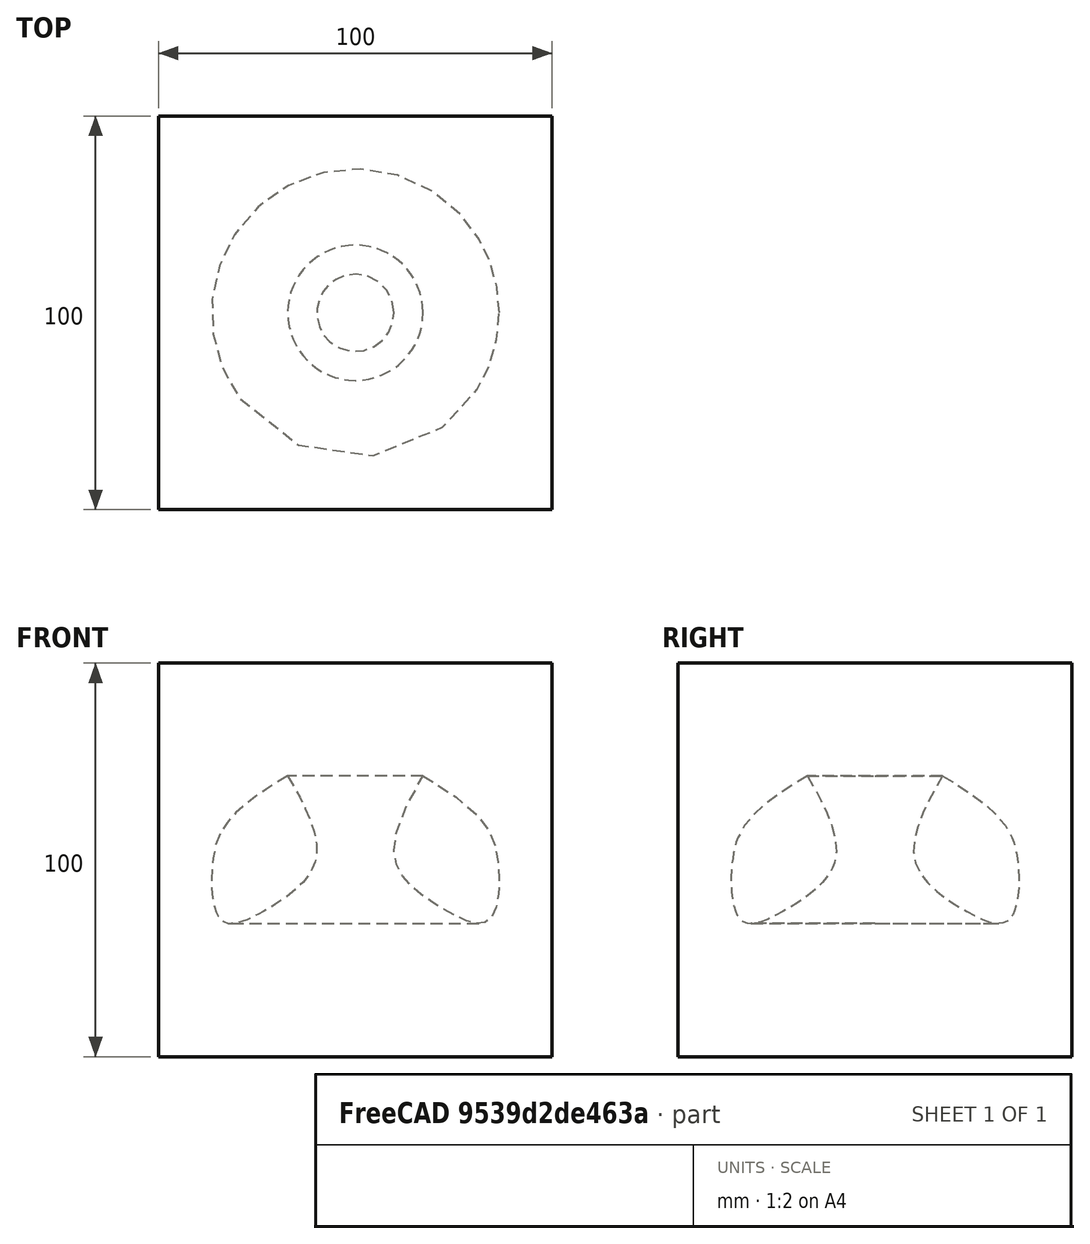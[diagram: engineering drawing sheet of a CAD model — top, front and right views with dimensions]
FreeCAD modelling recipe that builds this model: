
FCSTD DOCUMENT  (FreeCAD 1.0R39109 (Git))
Label: revolveSingleEdge-Bspline
License: All rights reserved
LicenseURL: http://en.wikipedia.org/wiki/All_rights_reserved
objects: App::DocumentObjectGroupPython×1248, App::Part×2, Part::FeaturePython×1, Sketcher::SketchObject×1, Part::Revolution×1
note: 4 computed .brp shape members not serialized (recipe doc carries the construction recipe); baked Part::Feature solids carry a one-line shape summary decoded from their .brp

FEATURE [App::DocumentObjectGroupPython] HALFPI  # scripted group (container) (typed FeaturePython)
  name = HALFPI
  value = pi/2.
FEATURE [App::DocumentObjectGroupPython] PI  # scripted group (container) (typed FeaturePython)
  name = PI
  value = 1.*pi
FEATURE [App::DocumentObjectGroupPython] TWOPI  # scripted group (container) (typed FeaturePython)
  name = TWOPI
  value = 2.*pi
FEATURE [App::DocumentObjectGroupPython] Constants  # scripted group (container) (typed FeaturePython)
  Group = -> [HALFPI,PI,TWOPI]
FEATURE [App::DocumentObjectGroupPython] Variables  # scripted group (container) (typed FeaturePython)
FEATURE [App::DocumentObjectGroupPython] Quantities  # scripted group (container) (typed FeaturePython)
FEATURE [App::DocumentObjectGroupPython] Isotopes  # scripted group (container) (typed FeaturePython)
FEATURE [App::DocumentObjectGroupPython] Elements  # scripted group (container) (typed FeaturePython)
FEATURE [App::DocumentObjectGroupPython] G4Isotopes  # scripted group (container) (typed FeaturePython)
FEATURE [App::DocumentObjectGroupPython] H_element  # scripted group (container) (typed FeaturePython)
  Z = 1
  atom_value = 1.008
  formula = H
  name = H_element
FEATURE [App::DocumentObjectGroupPython] He_element  # scripted group (container) (typed FeaturePython)
  Z = 2
  atom_value = 4.0026
  formula = He
  name = He_element
FEATURE [App::DocumentObjectGroupPython] Li_element  # scripted group (container) (typed FeaturePython)
  Z = 3
  atom_value = 6.94
  formula = Li
  name = Li_element
FEATURE [App::DocumentObjectGroupPython] Be_element  # scripted group (container) (typed FeaturePython)
  Z = 4
  atom_value = 9.01218
  formula = Be
  name = Be_element
FEATURE [App::DocumentObjectGroupPython] B_element  # scripted group (container) (typed FeaturePython)
  Z = 5
  atom_value = 10.81
  formula = B
  name = B_element
FEATURE [App::DocumentObjectGroupPython] C_element  # scripted group (container) (typed FeaturePython)
  Z = 6
  atom_value = 12.011
  formula = C
  name = C_element
FEATURE [App::DocumentObjectGroupPython] N_element  # scripted group (container) (typed FeaturePython)
  Z = 7
  atom_value = 14.007
  formula = N
  name = N_element
FEATURE [App::DocumentObjectGroupPython] O_element  # scripted group (container) (typed FeaturePython)
  Z = 8
  atom_value = 15.999
  formula = O
  name = O_element
FEATURE [App::DocumentObjectGroupPython] F_element  # scripted group (container) (typed FeaturePython)
  Z = 9
  atom_value = 18.9984
  formula = F
  name = F_element
FEATURE [App::DocumentObjectGroupPython] Ne_element  # scripted group (container) (typed FeaturePython)
  Z = 10
  atom_value = 20.1797
  formula = Ne
  name = Ne_element
FEATURE [App::DocumentObjectGroupPython] Na_element  # scripted group (container) (typed FeaturePython)
  Z = 11
  atom_value = 22.9898
  formula = Na
  name = Na_element
FEATURE [App::DocumentObjectGroupPython] Mg_element  # scripted group (container) (typed FeaturePython)
  Z = 12
  atom_value = 24.305
  formula = Mg
  name = Mg_element
FEATURE [App::DocumentObjectGroupPython] Al_element  # scripted group (container) (typed FeaturePython)
  Z = 13
  atom_value = 26.9815
  formula = Al
  name = Al_element
FEATURE [App::DocumentObjectGroupPython] Si_element  # scripted group (container) (typed FeaturePython)
  Z = 14
  atom_value = 28.085
  formula = Si
  name = Si_element
FEATURE [App::DocumentObjectGroupPython] P_element  # scripted group (container) (typed FeaturePython)
  Z = 15
  atom_value = 30.9738
  formula = P
  name = P_element
FEATURE [App::DocumentObjectGroupPython] S_element  # scripted group (container) (typed FeaturePython)
  Z = 16
  atom_value = 32.06
  formula = S
  name = S_element
FEATURE [App::DocumentObjectGroupPython] Cl_element  # scripted group (container) (typed FeaturePython)
  Z = 17
  atom_value = 35.45
  formula = Cl
  name = Cl_element
FEATURE [App::DocumentObjectGroupPython] Ar_element  # scripted group (container) (typed FeaturePython)
  Z = 18
  atom_value = 39.95
  formula = Ar
  name = Ar_element
FEATURE [App::DocumentObjectGroupPython] K_element  # scripted group (container) (typed FeaturePython)
  Z = 19
  atom_value = 39.0983
  formula = K
  name = K_element
FEATURE [App::DocumentObjectGroupPython] Ca_element  # scripted group (container) (typed FeaturePython)
  Z = 20
  atom_value = 40.078
  formula = Ca
  name = Ca_element
FEATURE [App::DocumentObjectGroupPython] Sc_element  # scripted group (container) (typed FeaturePython)
  Z = 21
  atom_value = 44.9559
  formula = Sc
  name = Sc_element
FEATURE [App::DocumentObjectGroupPython] Ti_element  # scripted group (container) (typed FeaturePython)
  Z = 22
  atom_value = 47.867
  formula = Ti
  name = Ti_element
FEATURE [App::DocumentObjectGroupPython] V_element  # scripted group (container) (typed FeaturePython)
  Z = 23
  atom_value = 50.9415
  formula = V
  name = V_element
FEATURE [App::DocumentObjectGroupPython] Cr_element  # scripted group (container) (typed FeaturePython)
  Z = 24
  atom_value = 51.9961
  formula = Cr
  name = Cr_element
FEATURE [App::DocumentObjectGroupPython] Mn_element  # scripted group (container) (typed FeaturePython)
  Z = 25
  atom_value = 54.938
  formula = Mn
  name = Mn_element
FEATURE [App::DocumentObjectGroupPython] Fe_element  # scripted group (container) (typed FeaturePython)
  Z = 26
  atom_value = 55.845
  formula = Fe
  name = Fe_element
FEATURE [App::DocumentObjectGroupPython] Co_element  # scripted group (container) (typed FeaturePython)
  Z = 27
  atom_value = 58.9332
  formula = Co
  name = Co_element
FEATURE [App::DocumentObjectGroupPython] Ni_element  # scripted group (container) (typed FeaturePython)
  Z = 28
  atom_value = 58.6934
  formula = Ni
  name = Ni_element
FEATURE [App::DocumentObjectGroupPython] Cu_element  # scripted group (container) (typed FeaturePython)
  Z = 29
  atom_value = 63.546
  formula = Cu
  name = Cu_element
FEATURE [App::DocumentObjectGroupPython] Zn_element  # scripted group (container) (typed FeaturePython)
  Z = 30
  atom_value = 65.38
  formula = Zn
  name = Zn_element
FEATURE [App::DocumentObjectGroupPython] Ga_element  # scripted group (container) (typed FeaturePython)
  Z = 31
  atom_value = 69.723
  formula = Ga
  name = Ga_element
FEATURE [App::DocumentObjectGroupPython] Ge_element  # scripted group (container) (typed FeaturePython)
  Z = 32
  atom_value = 72.63
  formula = Ge
  name = Ge_element
FEATURE [App::DocumentObjectGroupPython] As_element  # scripted group (container) (typed FeaturePython)
  Z = 33
  atom_value = 74.9216
  formula = As
  name = As_element
FEATURE [App::DocumentObjectGroupPython] Se_element  # scripted group (container) (typed FeaturePython)
  Z = 34
  atom_value = 78.971
  formula = Se
  name = Se_element
FEATURE [App::DocumentObjectGroupPython] Br_element  # scripted group (container) (typed FeaturePython)
  Z = 35
  atom_value = 79.904
  formula = Br
  name = Br_element
FEATURE [App::DocumentObjectGroupPython] Kr_element  # scripted group (container) (typed FeaturePython)
  Z = 36
  atom_value = 83.798
  formula = Kr
  name = Kr_element
FEATURE [App::DocumentObjectGroupPython] Rb_element  # scripted group (container) (typed FeaturePython)
  Z = 37
  atom_value = 85.4678
  formula = Rb
  name = Rb_element
FEATURE [App::DocumentObjectGroupPython] Sr_element  # scripted group (container) (typed FeaturePython)
  Z = 38
  atom_value = 87.62
  formula = Sr
  name = Sr_element
FEATURE [App::DocumentObjectGroupPython] Y_element  # scripted group (container) (typed FeaturePython)
  Z = 39
  atom_value = 88.9058
  formula = Y
  name = Y_element
FEATURE [App::DocumentObjectGroupPython] Zr_element  # scripted group (container) (typed FeaturePython)
  Z = 40
  atom_value = 91.224
  formula = Zr
  name = Zr_element
FEATURE [App::DocumentObjectGroupPython] Nb_element  # scripted group (container) (typed FeaturePython)
  Z = 41
  atom_value = 92.9064
  formula = Nb
  name = Nb_element
FEATURE [App::DocumentObjectGroupPython] Mo_element  # scripted group (container) (typed FeaturePython)
  Z = 42
  atom_value = 95.95
  formula = Mo
  name = Mo_element
FEATURE [App::DocumentObjectGroupPython] Tc_element  # scripted group (container) (typed FeaturePython)
  Z = 43
  atom_value = 97
  formula = Tc
  name = Tc_element
FEATURE [App::DocumentObjectGroupPython] Ru_element  # scripted group (container) (typed FeaturePython)
  Z = 44
  atom_value = 101.07
  formula = Ru
  name = Ru_element
FEATURE [App::DocumentObjectGroupPython] Rh_element  # scripted group (container) (typed FeaturePython)
  Z = 45
  atom_value = 102.905
  formula = Rh
  name = Rh_element
FEATURE [App::DocumentObjectGroupPython] Pd_element  # scripted group (container) (typed FeaturePython)
  Z = 46
  atom_value = 106.42
  formula = Pd
  name = Pd_element
FEATURE [App::DocumentObjectGroupPython] Ag_element  # scripted group (container) (typed FeaturePython)
  Z = 47
  atom_value = 107.868
  formula = Ag
  name = Ag_element
FEATURE [App::DocumentObjectGroupPython] Cd_element  # scripted group (container) (typed FeaturePython)
  Z = 48
  atom_value = 112.414
  formula = Cd
  name = Cd_element
FEATURE [App::DocumentObjectGroupPython] In_element  # scripted group (container) (typed FeaturePython)
  Z = 49
  atom_value = 114.818
  formula = In
  name = In_element
FEATURE [App::DocumentObjectGroupPython] Sn_element  # scripted group (container) (typed FeaturePython)
  Z = 50
  atom_value = 118.71
  formula = Sn
  name = Sn_element
FEATURE [App::DocumentObjectGroupPython] Sb_element  # scripted group (container) (typed FeaturePython)
  Z = 51
  atom_value = 121.76
  formula = Sb
  name = Sb_element
FEATURE [App::DocumentObjectGroupPython] Te_element  # scripted group (container) (typed FeaturePython)
  Z = 52
  atom_value = 127.6
  formula = Te
  name = Te_element
FEATURE [App::DocumentObjectGroupPython] I_element  # scripted group (container) (typed FeaturePython)
  Z = 53
  atom_value = 126.904
  formula = I
  name = I_element
FEATURE [App::DocumentObjectGroupPython] Xe_element  # scripted group (container) (typed FeaturePython)
  Z = 54
  atom_value = 131.293
  formula = Xe
  name = Xe_element
FEATURE [App::DocumentObjectGroupPython] Cs_element  # scripted group (container) (typed FeaturePython)
  Z = 55
  atom_value = 132.905
  formula = Cs
  name = Cs_element
FEATURE [App::DocumentObjectGroupPython] Ba_element  # scripted group (container) (typed FeaturePython)
  Z = 56
  atom_value = 137.327
  formula = Ba
  name = Ba_element
FEATURE [App::DocumentObjectGroupPython] La_element  # scripted group (container) (typed FeaturePython)
  Z = 57
  atom_value = 138.905
  formula = La
  name = La_element
FEATURE [App::DocumentObjectGroupPython] Ce_element  # scripted group (container) (typed FeaturePython)
  Z = 58
  atom_value = 140.116
  formula = Ce
  name = Ce_element
FEATURE [App::DocumentObjectGroupPython] Pr_element  # scripted group (container) (typed FeaturePython)
  Z = 59
  atom_value = 140.908
  formula = Pr
  name = Pr_element
FEATURE [App::DocumentObjectGroupPython] Nd_element  # scripted group (container) (typed FeaturePython)
  Z = 60
  atom_value = 144.242
  formula = Nd
  name = Nd_element
FEATURE [App::DocumentObjectGroupPython] Pm_element  # scripted group (container) (typed FeaturePython)
  Z = 61
  atom_value = 145
  formula = Pm
  name = Pm_element
FEATURE [App::DocumentObjectGroupPython] Sm_element  # scripted group (container) (typed FeaturePython)
  Z = 62
  atom_value = 150.36
  formula = Sm
  name = Sm_element
FEATURE [App::DocumentObjectGroupPython] Eu_element  # scripted group (container) (typed FeaturePython)
  Z = 63
  atom_value = 151.964
  formula = Eu
  name = Eu_element
FEATURE [App::DocumentObjectGroupPython] Gd_element  # scripted group (container) (typed FeaturePython)
  Z = 64
  atom_value = 157.25
  formula = Gd
  name = Gd_element
FEATURE [App::DocumentObjectGroupPython] Tb_element  # scripted group (container) (typed FeaturePython)
  Z = 65
  atom_value = 158.925
  formula = Tb
  name = Tb_element
FEATURE [App::DocumentObjectGroupPython] Dy_element  # scripted group (container) (typed FeaturePython)
  Z = 66
  atom_value = 162.5
  formula = Dy
  name = Dy_element
FEATURE [App::DocumentObjectGroupPython] Ho_element  # scripted group (container) (typed FeaturePython)
  Z = 67
  atom_value = 164.93
  formula = Ho
  name = Ho_element
FEATURE [App::DocumentObjectGroupPython] Er_element  # scripted group (container) (typed FeaturePython)
  Z = 68
  atom_value = 167.259
  formula = Er
  name = Er_element
FEATURE [App::DocumentObjectGroupPython] Tm_element  # scripted group (container) (typed FeaturePython)
  Z = 69
  atom_value = 168.934
  formula = Tm
  name = Tm_element
FEATURE [App::DocumentObjectGroupPython] Yb_element  # scripted group (container) (typed FeaturePython)
  Z = 70
  atom_value = 173.045
  formula = Yb
  name = Yb_element
FEATURE [App::DocumentObjectGroupPython] Lu_element  # scripted group (container) (typed FeaturePython)
  Z = 71
  atom_value = 174.967
  formula = Lu
  name = Lu_element
FEATURE [App::DocumentObjectGroupPython] Hf_element  # scripted group (container) (typed FeaturePython)
  Z = 72
  atom_value = 178.49
  formula = Hf
  name = Hf_element
FEATURE [App::DocumentObjectGroupPython] Ta_element  # scripted group (container) (typed FeaturePython)
  Z = 73
  atom_value = 180.948
  formula = Ta
  name = Ta_element
FEATURE [App::DocumentObjectGroupPython] W_element  # scripted group (container) (typed FeaturePython)
  Z = 74
  atom_value = 183.84
  formula = W
  name = W_element
FEATURE [App::DocumentObjectGroupPython] Re_element  # scripted group (container) (typed FeaturePython)
  Z = 75
  atom_value = 186.207
  formula = Re
  name = Re_element
FEATURE [App::DocumentObjectGroupPython] Os_element  # scripted group (container) (typed FeaturePython)
  Z = 76
  atom_value = 190.23
  formula = Os
  name = Os_element
FEATURE [App::DocumentObjectGroupPython] Ir_element  # scripted group (container) (typed FeaturePython)
  Z = 77
  atom_value = 192.217
  formula = Ir
  name = Ir_element
FEATURE [App::DocumentObjectGroupPython] Pt_element  # scripted group (container) (typed FeaturePython)
  Z = 78
  atom_value = 195.084
  formula = Pt
  name = Pt_element
FEATURE [App::DocumentObjectGroupPython] Au_element  # scripted group (container) (typed FeaturePython)
  Z = 79
  atom_value = 196.967
  formula = Au
  name = Au_element
FEATURE [App::DocumentObjectGroupPython] Hg_element  # scripted group (container) (typed FeaturePython)
  Z = 80
  atom_value = 200.592
  formula = Hg
  name = Hg_element
FEATURE [App::DocumentObjectGroupPython] Tl_element  # scripted group (container) (typed FeaturePython)
  Z = 81
  atom_value = 204.38
  formula = Tl
  name = Tl_element
FEATURE [App::DocumentObjectGroupPython] Pb_element  # scripted group (container) (typed FeaturePython)
  Z = 82
  atom_value = 207.2
  formula = Pb
  name = Pb_element
FEATURE [App::DocumentObjectGroupPython] Bi_element  # scripted group (container) (typed FeaturePython)
  Z = 83
  atom_value = 208.98
  formula = Bi
  name = Bi_element
FEATURE [App::DocumentObjectGroupPython] Po_element  # scripted group (container) (typed FeaturePython)
  Z = 84
  atom_value = 209
  formula = Po
  name = Po_element
FEATURE [App::DocumentObjectGroupPython] At_element  # scripted group (container) (typed FeaturePython)
  Z = 85
  atom_value = 210
  formula = At
  name = At_element
FEATURE [App::DocumentObjectGroupPython] Rn_element  # scripted group (container) (typed FeaturePython)
  Z = 86
  atom_value = 222
  formula = Rn
  name = Rn_element
FEATURE [App::DocumentObjectGroupPython] Fr_element  # scripted group (container) (typed FeaturePython)
  Z = 87
  atom_value = 223
  formula = Fr
  name = Fr_element
FEATURE [App::DocumentObjectGroupPython] Ra_element  # scripted group (container) (typed FeaturePython)
  Z = 88
  atom_value = 226
  formula = Ra
  name = Ra_element
FEATURE [App::DocumentObjectGroupPython] Ac_element  # scripted group (container) (typed FeaturePython)
  Z = 89
  atom_value = 227
  formula = Ac
  name = Ac_element
FEATURE [App::DocumentObjectGroupPython] Th_element  # scripted group (container) (typed FeaturePython)
  Z = 90
  atom_value = 232.038
  formula = Th
  name = Th_element
FEATURE [App::DocumentObjectGroupPython] Pa_element  # scripted group (container) (typed FeaturePython)
  Z = 91
  atom_value = 231.036
  formula = Pa
  name = Pa_element
FEATURE [App::DocumentObjectGroupPython] U_element  # scripted group (container) (typed FeaturePython)
  Z = 92
  atom_value = 238.029
  formula = U
  name = U_element
FEATURE [App::DocumentObjectGroupPython] Np_element  # scripted group (container) (typed FeaturePython)
  Z = 93
  atom_value = 237
  formula = Np
  name = Np_element
FEATURE [App::DocumentObjectGroupPython] Pu_element  # scripted group (container) (typed FeaturePython)
  Z = 94
  atom_value = 244
  formula = Pu
  name = Pu_element
FEATURE [App::DocumentObjectGroupPython] Am_element  # scripted group (container) (typed FeaturePython)
  Z = 95
  atom_value = 243
  formula = Am
  name = Am_element
FEATURE [App::DocumentObjectGroupPython] Cm_element  # scripted group (container) (typed FeaturePython)
  Z = 96
  atom_value = 247
  formula = Cm
  name = Cm_element
FEATURE [App::DocumentObjectGroupPython] Bk_element  # scripted group (container) (typed FeaturePython)
  Z = 97
  atom_value = 247
  formula = Bk
  name = Bk_element
FEATURE [App::DocumentObjectGroupPython] Cf_element  # scripted group (container) (typed FeaturePython)
  Z = 98
  atom_value = 251
  formula = Cf
  name = Cf_element
FEATURE [App::DocumentObjectGroupPython] G4Elements  # scripted group (container) (typed FeaturePython)
  Group = -> [H_element,He_element,Li_element,Be_element,B_element,C_element,N_element,O_element,F_element,Ne_element,Na_element,Mg_element,Al_element,Si_element,P_element,S_element,Cl_element,Ar_element,K_element,Ca_element,Sc_element,Ti_element,V_element,Cr_element,Mn_element,Fe_element,Co_element,Ni_element,Cu_element,Zn_element,Ga_element,Ge_element,As_element,Se_element,Br_element,Kr_element,Rb_element,+61 more]
FEATURE [App::DocumentObjectGroupPython] H_element001  label="H_element : 0.101"  # scripted group (container) (typed FeaturePython)
  n = 0.101327
FEATURE [App::DocumentObjectGroupPython] C_element001  label="C_element : 0.775"  # scripted group (container) (typed FeaturePython)
  n = 0.7755
FEATURE [App::DocumentObjectGroupPython] N_element001  label="N_element : 0.035"  # scripted group (container) (typed FeaturePython)
  n = 0.035057
FEATURE [App::DocumentObjectGroupPython] O_element001  label="O_element : 0.052"  # scripted group (container) (typed FeaturePython)
  n = 0.0523159
FEATURE [App::DocumentObjectGroupPython] F_element001  label="F_element : 0.017"  # scripted group (container) (typed FeaturePython)
  n = 0.017422
FEATURE [App::DocumentObjectGroupPython] Ca_element001  label="Ca_element : 0.018"  # scripted group (container) (typed FeaturePython)
  n = 0.018378
FEATURE [App::DocumentObjectGroupPython] G4_A_150_TISSUE  label="G4_A-150_TISSUE"  # scripted group (container) (typed FeaturePython)
  Dunit = g/cm3
  Dvalue = 1.127
  Group = -> [H_element001,C_element001,N_element001,O_element001,F_element001,Ca_element001]
  conduct = 2
  density = 1
  expand = 3
  formula = G4_A-150_TISSUE
  name = G4_A-150_TISSUE
  specific = 4
FEATURE [App::DocumentObjectGroupPython] C_element002  label="C_element : 3"  # scripted group (container) (typed FeaturePython)
  n = 3
  ref = C_element
FEATURE [App::DocumentObjectGroupPython] H_element002  label="H_element : 6"  # scripted group (container) (typed FeaturePython)
  n = 6
  ref = H_element
FEATURE [App::DocumentObjectGroupPython] O_element002  label="O_element : 1"  # scripted group (container) (typed FeaturePython)
  n = 1
  ref = O_element
FEATURE [App::DocumentObjectGroupPython] G4_ACETONE  # scripted group (container) (typed FeaturePython)
  Dunit = g/cm3
  Dvalue = 0.7899
  Group = -> [C_element002,H_element002,O_element002]
  conduct = 2
  density = 1
  expand = 3
  formula = G4_ACETONE
  name = G4_ACETONE
  specific = 4
FEATURE [App::DocumentObjectGroupPython] C_element003  label="C_element : 2"  # scripted group (container) (typed FeaturePython)
  n = 2
  ref = C_element
FEATURE [App::DocumentObjectGroupPython] H_element003  label="H_element : 2"  # scripted group (container) (typed FeaturePython)
  n = 2
  ref = H_element
FEATURE [App::DocumentObjectGroupPython] G4_ACETYLENE  # scripted group (container) (typed FeaturePython)
  Dunit = g/cm3
  Dvalue = 0.0010967
  Group = -> [C_element003,H_element003]
  conduct = 2
  density = 1
  expand = 3
  formula = G4_ACETYLENE
  name = G4_ACETYLENE
  specific = 4
FEATURE [App::DocumentObjectGroupPython] C_element004  label="C_element : 5"  # scripted group (container) (typed FeaturePython)
  n = 5
  ref = C_element
FEATURE [App::DocumentObjectGroupPython] H_element004  label="H_element : 5"  # scripted group (container) (typed FeaturePython)
  n = 5
  ref = H_element
FEATURE [App::DocumentObjectGroupPython] N_element002  label="N_element : 5"  # scripted group (container) (typed FeaturePython)
  n = 5
  ref = N_element
FEATURE [App::DocumentObjectGroupPython] G4_ADENINE  # scripted group (container) (typed FeaturePython)
  Dunit = g/cm3
  Dvalue = 1.6
  Group = -> [C_element004,H_element004,N_element002]
  conduct = 2
  density = 1
  expand = 3
  formula = G4_ADENINE
  name = G4_ADENINE
  specific = 4
FEATURE [App::DocumentObjectGroupPython] H_element005  label="H_element : 0.114"  # scripted group (container) (typed FeaturePython)
  n = 0.114
FEATURE [App::DocumentObjectGroupPython] C_element005  label="C_element : 0.598"  # scripted group (container) (typed FeaturePython)
  n = 0.598
FEATURE [App::DocumentObjectGroupPython] N_element003  label="N_element : 0.007"  # scripted group (container) (typed FeaturePython)
  n = 0.007
FEATURE [App::DocumentObjectGroupPython] O_element003  label="O_element : 0.278"  # scripted group (container) (typed FeaturePython)
  n = 0.278
FEATURE [App::DocumentObjectGroupPython] Na_element001  label="Na_element : 0.001"  # scripted group (container) (typed FeaturePython)
  n = 0.001
FEATURE [App::DocumentObjectGroupPython] S_element001  label="S_element : 0.001"  # scripted group (container) (typed FeaturePython)
  n = 0.001
FEATURE [App::DocumentObjectGroupPython] Cl_element001  label="Cl_element : 0.001"  # scripted group (container) (typed FeaturePython)
  n = 0.001
FEATURE [App::DocumentObjectGroupPython] G4_ADIPOSE_TISSUE_ICRP  # scripted group (container) (typed FeaturePython)
  Dunit = g/cm3
  Dvalue = 0.95
  Group = -> [H_element005,C_element005,N_element003,O_element003,Na_element001,S_element001,Cl_element001]
  conduct = 2
  density = 1
  expand = 3
  formula = G4_ADIPOSE_TISSUE_ICRP
  name = G4_ADIPOSE_TISSUE_ICRP
  specific = 4
FEATURE [App::DocumentObjectGroupPython] C_element006  label="C_element : 0.000"  # scripted group (container) (typed FeaturePython)
  n = 0.000124
FEATURE [App::DocumentObjectGroupPython] N_element004  label="N_element : 0.755"  # scripted group (container) (typed FeaturePython)
  n = 0.755268
FEATURE [App::DocumentObjectGroupPython] O_element004  label="O_element : 0.232"  # scripted group (container) (typed FeaturePython)
  n = 0.231781
FEATURE [App::DocumentObjectGroupPython] Ar_element001  label="Ar_element : 0.013"  # scripted group (container) (typed FeaturePython)
  n = 0.012827
FEATURE [App::DocumentObjectGroupPython] G4_AIR  # scripted group (container) (typed FeaturePython)
  Dunit = g/cm3
  Dvalue = 0.00120479
  Group = -> [C_element006,N_element004,O_element004,Ar_element001]
  conduct = 2
  density = 1
  expand = 3
  formula = G4_AIR
  name = G4_AIR
  specific = 4
FEATURE [App::DocumentObjectGroupPython] C_element007  label="C_element : 006"  # scripted group (container) (typed FeaturePython)
  n = 3
  ref = C_element
FEATURE [App::DocumentObjectGroupPython] H_element006  label="H_element : 7"  # scripted group (container) (typed FeaturePython)
  n = 7
  ref = H_element
FEATURE [App::DocumentObjectGroupPython] N_element005  label="N_element : 1"  # scripted group (container) (typed FeaturePython)
  n = 1
  ref = N_element
FEATURE [App::DocumentObjectGroupPython] O_element005  label="O_element : 2"  # scripted group (container) (typed FeaturePython)
  n = 2
  ref = O_element
FEATURE [App::DocumentObjectGroupPython] G4_ALANINE  # scripted group (container) (typed FeaturePython)
  Dunit = g/cm3
  Dvalue = 1.42
  Group = -> [C_element007,H_element006,N_element005,O_element005]
  conduct = 2
  density = 1
  expand = 3
  formula = G4_ALANINE
  name = G4_ALANINE
  specific = 4
FEATURE [App::DocumentObjectGroupPython] Al_element001  label="Al_element : 2"  # scripted group (container) (typed FeaturePython)
  n = 2
  ref = Al_element
FEATURE [App::DocumentObjectGroupPython] O_element006  label="O_element : 3"  # scripted group (container) (typed FeaturePython)
  n = 3
  ref = O_element
FEATURE [App::DocumentObjectGroupPython] G4_ALUMINUM_OXIDE  # scripted group (container) (typed FeaturePython)
  Dunit = g/cm3
  Dvalue = 3.97
  Group = -> [Al_element001,O_element006]
  conduct = 2
  density = 1
  expand = 3
  formula = G4_ALUMINUM_OXIDE
  name = G4_ALUMINUM_OXIDE
  specific = 4
FEATURE [App::DocumentObjectGroupPython] H_element007  label="H_element : 0.106"  # scripted group (container) (typed FeaturePython)
  n = 0.10593
FEATURE [App::DocumentObjectGroupPython] C_element008  label="C_element : 0.789"  # scripted group (container) (typed FeaturePython)
  n = 0.788974
FEATURE [App::DocumentObjectGroupPython] O_element007  label="O_element : 0.105"  # scripted group (container) (typed FeaturePython)
  n = 0.105096
FEATURE [App::DocumentObjectGroupPython] G4_AMBER  # scripted group (container) (typed FeaturePython)
  Dunit = g/cm3
  Dvalue = 1.1
  Group = -> [H_element007,C_element008,O_element007]
  conduct = 2
  density = 1
  expand = 3
  formula = G4_AMBER
  name = G4_AMBER
  specific = 4
FEATURE [App::DocumentObjectGroupPython] N_element006  label="N_element : 006"  # scripted group (container) (typed FeaturePython)
  n = 1
  ref = N_element
FEATURE [App::DocumentObjectGroupPython] H_element008  label="H_element : 3"  # scripted group (container) (typed FeaturePython)
  n = 3
  ref = H_element
FEATURE [App::DocumentObjectGroupPython] G4_AMMONIA  # scripted group (container) (typed FeaturePython)
  Dunit = g/cm3
  Dvalue = 0.000826019
  Group = -> [N_element006,H_element008]
  conduct = 2
  density = 1
  expand = 3
  formula = G4_AMMONIA
  name = G4_AMMONIA
  specific = 4
FEATURE [App::DocumentObjectGroupPython] C_element009  label="C_element : 6"  # scripted group (container) (typed FeaturePython)
  n = 6
  ref = C_element
FEATURE [App::DocumentObjectGroupPython] H_element009  label="H_element : 008"  # scripted group (container) (typed FeaturePython)
  n = 7
  ref = H_element
FEATURE [App::DocumentObjectGroupPython] N_element007  label="N_element : 007"  # scripted group (container) (typed FeaturePython)
  n = 1
  ref = N_element
FEATURE [App::DocumentObjectGroupPython] G4_ANILINE  # scripted group (container) (typed FeaturePython)
  Dunit = g/cm3
  Dvalue = 1.0235
  Group = -> [C_element009,H_element009,N_element007]
  conduct = 2
  density = 1
  expand = 3
  formula = G4_ANILINE
  name = G4_ANILINE
  specific = 4
FEATURE [App::DocumentObjectGroupPython] C_element010  label="C_element : 14"  # scripted group (container) (typed FeaturePython)
  n = 14
  ref = C_element
FEATURE [App::DocumentObjectGroupPython] H_element010  label="H_element : 10"  # scripted group (container) (typed FeaturePython)
  n = 10
  ref = H_element
FEATURE [App::DocumentObjectGroupPython] G4_ANTHRACENE  # scripted group (container) (typed FeaturePython)
  Dunit = g/cm3
  Dvalue = 1.283
  Group = -> [C_element010,H_element010]
  conduct = 2
  density = 1
  expand = 3
  formula = G4_ANTHRACENE
  name = G4_ANTHRACENE
  specific = 4
FEATURE [App::DocumentObjectGroupPython] H_element011  label="H_element : 0.065"  # scripted group (container) (typed FeaturePython)
  n = 0.0654709
FEATURE [App::DocumentObjectGroupPython] C_element011  label="C_element : 0.537"  # scripted group (container) (typed FeaturePython)
  n = 0.536944
FEATURE [App::DocumentObjectGroupPython] N_element008  label="N_element : 0.021"  # scripted group (container) (typed FeaturePython)
  n = 0.0215
FEATURE [App::DocumentObjectGroupPython] O_element008  label="O_element : 0.032"  # scripted group (container) (typed FeaturePython)
  n = 0.032085
FEATURE [App::DocumentObjectGroupPython] F_element002  label="F_element : 0.167"  # scripted group (container) (typed FeaturePython)
  n = 0.167411
FEATURE [App::DocumentObjectGroupPython] Ca_element002  label="Ca_element : 0.177"  # scripted group (container) (typed FeaturePython)
  n = 0.176589
FEATURE [App::DocumentObjectGroupPython] G4_B_100_BONE  label="G4_B-100_BONE"  # scripted group (container) (typed FeaturePython)
  Dunit = g/cm3
  Dvalue = 1.45
  Group = -> [H_element011,C_element011,N_element008,O_element008,F_element002,Ca_element002]
  conduct = 2
  density = 1
  expand = 3
  formula = G4_B-100_BONE
  name = G4_B-100_BONE
  specific = 4
FEATURE [App::DocumentObjectGroupPython] H_element012  label="H_element : 0.057"  # scripted group (container) (typed FeaturePython)
  n = 0.057441
FEATURE [App::DocumentObjectGroupPython] C_element012  label="C_element : 0.790"  # scripted group (container) (typed FeaturePython)
  n = 0.774591
FEATURE [App::DocumentObjectGroupPython] O_element009  label="O_element : 0.168"  # scripted group (container) (typed FeaturePython)
  n = 0.167968
FEATURE [App::DocumentObjectGroupPython] G4_BAKELITE  # scripted group (container) (typed FeaturePython)
  Dunit = g/cm3
  Dvalue = 1.25
  Group = -> [H_element012,C_element012,O_element009]
  conduct = 2
  density = 1
  expand = 3
  formula = G4_BAKELITE
  name = G4_BAKELITE
  specific = 4
FEATURE [App::DocumentObjectGroupPython] Ba_element001  label="Ba_element : 1"  # scripted group (container) (typed FeaturePython)
  n = 1
  ref = Ba_element
FEATURE [App::DocumentObjectGroupPython] F_element003  label="F_element : 2"  # scripted group (container) (typed FeaturePython)
  n = 2
  ref = F_element
FEATURE [App::DocumentObjectGroupPython] G4_BARIUM_FLUORIDE  # scripted group (container) (typed FeaturePython)
  Dunit = g/cm3
  Dvalue = 4.89
  Group = -> [Ba_element001,F_element003]
  conduct = 2
  density = 1
  expand = 3
  formula = G4_BARIUM_FLUORIDE
  name = G4_BARIUM_FLUORIDE
  specific = 4
FEATURE [App::DocumentObjectGroupPython] Ba_element002  label="Ba_element : 002"  # scripted group (container) (typed FeaturePython)
  n = 1
  ref = Ba_element
FEATURE [App::DocumentObjectGroupPython] S_element002  label="S_element : 1"  # scripted group (container) (typed FeaturePython)
  n = 1
  ref = S_element
FEATURE [App::DocumentObjectGroupPython] O_element010  label="O_element : 4"  # scripted group (container) (typed FeaturePython)
  n = 4
  ref = O_element
FEATURE [App::DocumentObjectGroupPython] G4_BARIUM_SULFATE  # scripted group (container) (typed FeaturePython)
  Dunit = g/cm3
  Dvalue = 4.5
  Group = -> [Ba_element002,S_element002,O_element010]
  conduct = 2
  density = 1
  expand = 3
  formula = G4_BARIUM_SULFATE
  name = G4_BARIUM_SULFATE
  specific = 4
FEATURE [App::DocumentObjectGroupPython] C_element013  label="C_element : 007"  # scripted group (container) (typed FeaturePython)
  n = 6
  ref = C_element
FEATURE [App::DocumentObjectGroupPython] H_element013  label="H_element : 009"  # scripted group (container) (typed FeaturePython)
  n = 6
  ref = H_element
FEATURE [App::DocumentObjectGroupPython] G4_BENZENE  # scripted group (container) (typed FeaturePython)
  Dunit = g/cm3
  Dvalue = 0.87865
  Group = -> [C_element013,H_element013]
  conduct = 2
  density = 1
  expand = 3
  formula = G4_BENZENE
  name = G4_BENZENE
  specific = 4
FEATURE [App::DocumentObjectGroupPython] Be_element001  label="Be_element : 1"  # scripted group (container) (typed FeaturePython)
  n = 1
  ref = Be_element
FEATURE [App::DocumentObjectGroupPython] O_element011  label="O_element : 005"  # scripted group (container) (typed FeaturePython)
  n = 1
  ref = O_element
FEATURE [App::DocumentObjectGroupPython] G4_BERYLLIUM_OXIDE  # scripted group (container) (typed FeaturePython)
  Dunit = g/cm3
  Dvalue = 3.01
  Group = -> [Be_element001,O_element011]
  conduct = 2
  density = 1
  expand = 3
  formula = G4_BERYLLIUM_OXIDE
  name = G4_BERYLLIUM_OXIDE
  specific = 4
FEATURE [App::DocumentObjectGroupPython] Bi_element001  label="Bi_element : 4"  # scripted group (container) (typed FeaturePython)
  n = 4
  ref = Bi_element
FEATURE [App::DocumentObjectGroupPython] Ge_element001  label="Ge_element : 3"  # scripted group (container) (typed FeaturePython)
  n = 3
  ref = Ge_element
FEATURE [App::DocumentObjectGroupPython] O_element012  label="O_element : 12"  # scripted group (container) (typed FeaturePython)
  n = 12
  ref = O_element
FEATURE [App::DocumentObjectGroupPython] G4_BGO  # scripted group (container) (typed FeaturePython)
  Dunit = g/cm3
  Dvalue = 7.13
  Group = -> [Bi_element001,Ge_element001,O_element012]
  conduct = 2
  density = 1
  expand = 3
  formula = G4_BGO
  name = G4_BGO
  specific = 4
FEATURE [App::DocumentObjectGroupPython] H_element014  label="H_element : 0.102"  # scripted group (container) (typed FeaturePython)
  n = 0.102
FEATURE [App::DocumentObjectGroupPython] C_element014  label="C_element : 0.110"  # scripted group (container) (typed FeaturePython)
  n = 0.11
FEATURE [App::DocumentObjectGroupPython] N_element009  label="N_element : 0.033"  # scripted group (container) (typed FeaturePython)
  n = 0.033
FEATURE [App::DocumentObjectGroupPython] O_element013  label="O_element : 0.745"  # scripted group (container) (typed FeaturePython)
  n = 0.745
FEATURE [App::DocumentObjectGroupPython] Na_element002  label="Na_element : 0.002"  # scripted group (container) (typed FeaturePython)
  n = 0.001
FEATURE [App::DocumentObjectGroupPython] P_element001  label="P_element : 0.001"  # scripted group (container) (typed FeaturePython)
  n = 0.001
FEATURE [App::DocumentObjectGroupPython] S_element003  label="S_element : 0.002"  # scripted group (container) (typed FeaturePython)
  n = 0.002
FEATURE [App::DocumentObjectGroupPython] Cl_element002  label="Cl_element : 0.003"  # scripted group (container) (typed FeaturePython)
  n = 0.003
FEATURE [App::DocumentObjectGroupPython] K_element001  label="K_element : 0.002"  # scripted group (container) (typed FeaturePython)
  n = 0.002
FEATURE [App::DocumentObjectGroupPython] Fe_element001  label="Fe_element : 0.001"  # scripted group (container) (typed FeaturePython)
  n = 0.001
FEATURE [App::DocumentObjectGroupPython] G4_BLOOD_ICRP  # scripted group (container) (typed FeaturePython)
  Dunit = g/cm3
  Dvalue = 1.06
  Group = -> [H_element014,C_element014,N_element009,O_element013,Na_element002,P_element001,S_element003,Cl_element002,K_element001,Fe_element001]
  conduct = 2
  density = 1
  expand = 3
  formula = G4_BLOOD_ICRP
  name = G4_BLOOD_ICRP
  specific = 4
FEATURE [App::DocumentObjectGroupPython] H_element015  label="H_element : 0.064"  # scripted group (container) (typed FeaturePython)
  n = 0.064
FEATURE [App::DocumentObjectGroupPython] C_element015  label="C_element : 0.278"  # scripted group (container) (typed FeaturePython)
  n = 0.278
FEATURE [App::DocumentObjectGroupPython] N_element010  label="N_element : 0.027"  # scripted group (container) (typed FeaturePython)
  n = 0.027
FEATURE [App::DocumentObjectGroupPython] O_element014  label="O_element : 0.410"  # scripted group (container) (typed FeaturePython)
  n = 0.41
FEATURE [App::DocumentObjectGroupPython] Mg_element001  label="Mg_element : 0.002"  # scripted group (container) (typed FeaturePython)
  n = 0.002
FEATURE [App::DocumentObjectGroupPython] P_element002  label="P_element : 0.070"  # scripted group (container) (typed FeaturePython)
  n = 0.07
FEATURE [App::DocumentObjectGroupPython] S_element004  label="S_element : 0.003"  # scripted group (container) (typed FeaturePython)
  n = 0.002
FEATURE [App::DocumentObjectGroupPython] Ca_element003  label="Ca_element : 0.147"  # scripted group (container) (typed FeaturePython)
  n = 0.147
FEATURE [App::DocumentObjectGroupPython] G4_BONE_COMPACT_ICRU  # scripted group (container) (typed FeaturePython)
  Dunit = g/cm3
  Dvalue = 1.85
  Group = -> [H_element015,C_element015,N_element010,O_element014,Mg_element001,P_element002,S_element004,Ca_element003]
  conduct = 2
  density = 1
  expand = 3
  formula = G4_BONE_COMPACT_ICRU
  name = G4_BONE_COMPACT_ICRU
  specific = 4
FEATURE [App::DocumentObjectGroupPython] H_element016  label="H_element : 0.034"  # scripted group (container) (typed FeaturePython)
  n = 0.034
FEATURE [App::DocumentObjectGroupPython] C_element016  label="C_element : 0.155"  # scripted group (container) (typed FeaturePython)
  n = 0.155
FEATURE [App::DocumentObjectGroupPython] N_element011  label="N_element : 0.042"  # scripted group (container) (typed FeaturePython)
  n = 0.042
FEATURE [App::DocumentObjectGroupPython] O_element015  label="O_element : 0.435"  # scripted group (container) (typed FeaturePython)
  n = 0.435
FEATURE [App::DocumentObjectGroupPython] Na_element003  label="Na_element : 0.003"  # scripted group (container) (typed FeaturePython)
  n = 0.001
FEATURE [App::DocumentObjectGroupPython] Mg_element002  label="Mg_element : 0.003"  # scripted group (container) (typed FeaturePython)
  n = 0.002
FEATURE [App::DocumentObjectGroupPython] P_element003  label="P_element : 0.103"  # scripted group (container) (typed FeaturePython)
  n = 0.103
FEATURE [App::DocumentObjectGroupPython] S_element005  label="S_element : 0.004"  # scripted group (container) (typed FeaturePython)
  n = 0.003
FEATURE [App::DocumentObjectGroupPython] Ca_element004  label="Ca_element : 0.225"  # scripted group (container) (typed FeaturePython)
  n = 0.225
FEATURE [App::DocumentObjectGroupPython] G4_BONE_CORTICAL_ICRP  # scripted group (container) (typed FeaturePython)
  Dunit = g/cm3
  Dvalue = 1.92
  Group = -> [H_element016,C_element016,N_element011,O_element015,Na_element003,Mg_element002,P_element003,S_element005,Ca_element004]
  conduct = 2
  density = 1
  expand = 3
  formula = G4_BONE_CORTICAL_ICRP
  name = G4_BONE_CORTICAL_ICRP
  specific = 4
FEATURE [App::DocumentObjectGroupPython] B_element001  label="B_element : 4"  # scripted group (container) (typed FeaturePython)
  n = 4
  ref = B_element
FEATURE [App::DocumentObjectGroupPython] C_element017  label="C_element : 1"  # scripted group (container) (typed FeaturePython)
  n = 1
  ref = C_element
FEATURE [App::DocumentObjectGroupPython] G4_BORON_CARBIDE  # scripted group (container) (typed FeaturePython)
  Dunit = g/cm3
  Dvalue = 2.52
  Group = -> [B_element001,C_element017]
  conduct = 2
  density = 1
  expand = 3
  formula = G4_BORON_CARBIDE
  name = G4_BORON_CARBIDE
  specific = 4
FEATURE [App::DocumentObjectGroupPython] B_element002  label="B_element : 2"  # scripted group (container) (typed FeaturePython)
  n = 2
  ref = B_element
FEATURE [App::DocumentObjectGroupPython] O_element016  label="O_element : 006"  # scripted group (container) (typed FeaturePython)
  n = 3
  ref = O_element
FEATURE [App::DocumentObjectGroupPython] G4_BORON_OXIDE  # scripted group (container) (typed FeaturePython)
  Dunit = g/cm3
  Dvalue = 1.812
  Group = -> [B_element002,O_element016]
  conduct = 2
  density = 1
  expand = 3
  formula = G4_BORON_OXIDE
  name = G4_BORON_OXIDE
  specific = 4
FEATURE [App::DocumentObjectGroupPython] H_element017  label="H_element : 0.107"  # scripted group (container) (typed FeaturePython)
  n = 0.107
FEATURE [App::DocumentObjectGroupPython] C_element018  label="C_element : 0.145"  # scripted group (container) (typed FeaturePython)
  n = 0.145
FEATURE [App::DocumentObjectGroupPython] N_element012  label="N_element : 0.022"  # scripted group (container) (typed FeaturePython)
  n = 0.022
FEATURE [App::DocumentObjectGroupPython] O_element017  label="O_element : 0.712"  # scripted group (container) (typed FeaturePython)
  n = 0.712
FEATURE [App::DocumentObjectGroupPython] Na_element004  label="Na_element : 0.004"  # scripted group (container) (typed FeaturePython)
  n = 0.002
FEATURE [App::DocumentObjectGroupPython] P_element004  label="P_element : 0.004"  # scripted group (container) (typed FeaturePython)
  n = 0.004
FEATURE [App::DocumentObjectGroupPython] S_element006  label="S_element : 0.005"  # scripted group (container) (typed FeaturePython)
  n = 0.002
FEATURE [App::DocumentObjectGroupPython] Cl_element003  label="Cl_element : 0.004"  # scripted group (container) (typed FeaturePython)
  n = 0.003
FEATURE [App::DocumentObjectGroupPython] K_element002  label="K_element : 0.003"  # scripted group (container) (typed FeaturePython)
  n = 0.003
FEATURE [App::DocumentObjectGroupPython] G4_BRAIN_ICRP  # scripted group (container) (typed FeaturePython)
  Dunit = g/cm3
  Dvalue = 1.04
  Group = -> [H_element017,C_element018,N_element012,O_element017,Na_element004,P_element004,S_element006,Cl_element003,K_element002]
  conduct = 2
  density = 1
  expand = 3
  formula = G4_BRAIN_ICRP
  name = G4_BRAIN_ICRP
  specific = 4
FEATURE [App::DocumentObjectGroupPython] C_element019  label="C_element : 4"  # scripted group (container) (typed FeaturePython)
  n = 4
  ref = C_element
FEATURE [App::DocumentObjectGroupPython] H_element018  label="H_element : 010"  # scripted group (container) (typed FeaturePython)
  n = 10
  ref = H_element
FEATURE [App::DocumentObjectGroupPython] G4_BUTANE  # scripted group (container) (typed FeaturePython)
  Dunit = g/cm3
  Dvalue = 0.00249343
  Group = -> [C_element019,H_element018]
  conduct = 2
  density = 1
  expand = 3
  formula = G4_BUTANE
  name = G4_BUTANE
  specific = 4
FEATURE [App::DocumentObjectGroupPython] C_element020  label="C_element : 008"  # scripted group (container) (typed FeaturePython)
  n = 4
  ref = C_element
FEATURE [App::DocumentObjectGroupPython] H_element019  label="H_element : 011"  # scripted group (container) (typed FeaturePython)
  n = 10
  ref = H_element
FEATURE [App::DocumentObjectGroupPython] O_element018  label="O_element : 007"  # scripted group (container) (typed FeaturePython)
  n = 1
  ref = O_element
FEATURE [App::DocumentObjectGroupPython] G4_N_BUTYL_ALCOHOL  label="G4_N-BUTYL_ALCOHOL"  # scripted group (container) (typed FeaturePython)
  Dunit = g/cm3
  Dvalue = 0.8098
  Group = -> [C_element020,H_element019,O_element018]
  conduct = 2
  density = 1
  expand = 3
  formula = G4_N-BUTYL_ALCOHOL
  name = G4_N-BUTYL_ALCOHOL
  specific = 4
FEATURE [App::DocumentObjectGroupPython] H_element020  label="H_element : 0.025"  # scripted group (container) (typed FeaturePython)
  n = 0.02468
FEATURE [App::DocumentObjectGroupPython] C_element021  label="C_element : 0.502"  # scripted group (container) (typed FeaturePython)
  n = 0.501611
FEATURE [App::DocumentObjectGroupPython] O_element019  label="O_element : 0.005"  # scripted group (container) (typed FeaturePython)
  n = 0.004527
FEATURE [App::DocumentObjectGroupPython] F_element004  label="F_element : 0.465"  # scripted group (container) (typed FeaturePython)
  n = 0.465209
FEATURE [App::DocumentObjectGroupPython] Si_element001  label="Si_element : 0.004"  # scripted group (container) (typed FeaturePython)
  n = 0.003973
FEATURE [App::DocumentObjectGroupPython] G4_C_552  label="G4_C-552"  # scripted group (container) (typed FeaturePython)
  Dunit = g/cm3
  Dvalue = 1.76
  Group = -> [H_element020,C_element021,O_element019,F_element004,Si_element001]
  conduct = 2
  density = 1
  expand = 3
  formula = G4_C-552
  name = G4_C-552
  specific = 4
FEATURE [App::DocumentObjectGroupPython] Cd_element001  label="Cd_element : 1"  # scripted group (container) (typed FeaturePython)
  n = 1
  ref = Cd_element
FEATURE [App::DocumentObjectGroupPython] Te_element001  label="Te_element : 1"  # scripted group (container) (typed FeaturePython)
  n = 1
  ref = Te_element
FEATURE [App::DocumentObjectGroupPython] G4_CADMIUM_TELLURIDE  # scripted group (container) (typed FeaturePython)
  Dunit = g/cm3
  Dvalue = 6.2
  Group = -> [Cd_element001,Te_element001]
  conduct = 2
  density = 1
  expand = 3
  formula = G4_CADMIUM_TELLURIDE
  name = G4_CADMIUM_TELLURIDE
  specific = 4
FEATURE [App::DocumentObjectGroupPython] Cd_element002  label="Cd_element : 002"  # scripted group (container) (typed FeaturePython)
  n = 1
  ref = Cd_element
FEATURE [App::DocumentObjectGroupPython] W_element001  label="W_element : 1"  # scripted group (container) (typed FeaturePython)
  n = 1
  ref = W_element
FEATURE [App::DocumentObjectGroupPython] O_element020  label="O_element : 008"  # scripted group (container) (typed FeaturePython)
  n = 4
  ref = O_element
FEATURE [App::DocumentObjectGroupPython] G4_CADMIUM_TUNGSTATE  # scripted group (container) (typed FeaturePython)
  Dunit = g/cm3
  Dvalue = 7.9
  Group = -> [Cd_element002,W_element001,O_element020]
  conduct = 2
  density = 1
  expand = 3
  formula = G4_CADMIUM_TUNGSTATE
  name = G4_CADMIUM_TUNGSTATE
  specific = 4
FEATURE [App::DocumentObjectGroupPython] Ca_element005  label="Ca_element : 1"  # scripted group (container) (typed FeaturePython)
  n = 1
  ref = Ca_element
FEATURE [App::DocumentObjectGroupPython] C_element022  label="C_element : 009"  # scripted group (container) (typed FeaturePython)
  n = 1
  ref = C_element
FEATURE [App::DocumentObjectGroupPython] O_element021  label="O_element : 009"  # scripted group (container) (typed FeaturePython)
  n = 3
  ref = O_element
FEATURE [App::DocumentObjectGroupPython] G4_CALCIUM_CARBONATE  # scripted group (container) (typed FeaturePython)
  Dunit = g/cm3
  Dvalue = 2.8
  Group = -> [Ca_element005,C_element022,O_element021]
  conduct = 2
  density = 1
  expand = 3
  formula = G4_CALCIUM_CARBONATE
  name = G4_CALCIUM_CARBONATE
  specific = 4
FEATURE [App::DocumentObjectGroupPython] Ca_element006  label="Ca_element : 002"  # scripted group (container) (typed FeaturePython)
  n = 1
  ref = Ca_element
FEATURE [App::DocumentObjectGroupPython] F_element005  label="F_element : 003"  # scripted group (container) (typed FeaturePython)
  n = 2
  ref = F_element
FEATURE [App::DocumentObjectGroupPython] G4_CALCIUM_FLUORIDE  # scripted group (container) (typed FeaturePython)
  Dunit = g/cm3
  Dvalue = 3.18
  Group = -> [Ca_element006,F_element005]
  conduct = 2
  density = 1
  expand = 3
  formula = G4_CALCIUM_FLUORIDE
  name = G4_CALCIUM_FLUORIDE
  specific = 4
FEATURE [App::DocumentObjectGroupPython] Ca_element007  label="Ca_element : 003"  # scripted group (container) (typed FeaturePython)
  n = 1
  ref = Ca_element
FEATURE [App::DocumentObjectGroupPython] O_element022  label="O_element : 010"  # scripted group (container) (typed FeaturePython)
  n = 1
  ref = O_element
FEATURE [App::DocumentObjectGroupPython] G4_CALCIUM_OXIDE  # scripted group (container) (typed FeaturePython)
  Dunit = g/cm3
  Dvalue = 3.3
  Group = -> [Ca_element007,O_element022]
  conduct = 2
  density = 1
  expand = 3
  formula = G4_CALCIUM_OXIDE
  name = G4_CALCIUM_OXIDE
  specific = 4
FEATURE [App::DocumentObjectGroupPython] Ca_element008  label="Ca_element : 004"  # scripted group (container) (typed FeaturePython)
  n = 1
  ref = Ca_element
FEATURE [App::DocumentObjectGroupPython] S_element007  label="S_element : 002"  # scripted group (container) (typed FeaturePython)
  n = 1
  ref = S_element
FEATURE [App::DocumentObjectGroupPython] O_element023  label="O_element : 011"  # scripted group (container) (typed FeaturePython)
  n = 4
  ref = O_element
FEATURE [App::DocumentObjectGroupPython] G4_CALCIUM_SULFATE  # scripted group (container) (typed FeaturePython)
  Dunit = g/cm3
  Dvalue = 2.96
  Group = -> [Ca_element008,S_element007,O_element023]
  conduct = 2
  density = 1
  expand = 3
  formula = G4_CALCIUM_SULFATE
  name = G4_CALCIUM_SULFATE
  specific = 4
FEATURE [App::DocumentObjectGroupPython] Ca_element009  label="Ca_element : 005"  # scripted group (container) (typed FeaturePython)
  n = 1
  ref = Ca_element
FEATURE [App::DocumentObjectGroupPython] W_element002  label="W_element : 002"  # scripted group (container) (typed FeaturePython)
  n = 1
  ref = W_element
FEATURE [App::DocumentObjectGroupPython] O_element024  label="O_element : 012"  # scripted group (container) (typed FeaturePython)
  n = 4
  ref = O_element
FEATURE [App::DocumentObjectGroupPython] G4_CALCIUM_TUNGSTATE  # scripted group (container) (typed FeaturePython)
  Dunit = g/cm3
  Dvalue = 6.062
  Group = -> [Ca_element009,W_element002,O_element024]
  conduct = 2
  density = 1
  expand = 3
  formula = G4_CALCIUM_TUNGSTATE
  name = G4_CALCIUM_TUNGSTATE
  specific = 4
FEATURE [App::DocumentObjectGroupPython] C_element023  label="C_element : 010"  # scripted group (container) (typed FeaturePython)
  n = 1
  ref = C_element
FEATURE [App::DocumentObjectGroupPython] O_element025  label="O_element : 013"  # scripted group (container) (typed FeaturePython)
  n = 2
  ref = O_element
FEATURE [App::DocumentObjectGroupPython] G4_CARBON_DIOXIDE  # scripted group (container) (typed FeaturePython)
  Dunit = g/cm3
  Dvalue = 0.00184212
  Group = -> [C_element023,O_element025]
  conduct = 2
  density = 1
  expand = 3
  formula = G4_CARBON_DIOXIDE
  name = G4_CARBON_DIOXIDE
  specific = 4
FEATURE [App::DocumentObjectGroupPython] C_element024  label="C_element : 011"  # scripted group (container) (typed FeaturePython)
  n = 1
  ref = C_element
FEATURE [App::DocumentObjectGroupPython] Cl_element004  label="Cl_element : 4"  # scripted group (container) (typed FeaturePython)
  n = 4
  ref = Cl_element
FEATURE [App::DocumentObjectGroupPython] G4_CARBON_TETRACHLORIDE  # scripted group (container) (typed FeaturePython)
  Dunit = g/cm3
  Dvalue = 1.594
  Group = -> [C_element024,Cl_element004]
  conduct = 2
  density = 1
  expand = 3
  formula = G4_CARBON_TETRACHLORIDE
  name = G4_CARBON_TETRACHLORIDE
  specific = 4
FEATURE [App::DocumentObjectGroupPython] C_element025  label="C_element : 012"  # scripted group (container) (typed FeaturePython)
  n = 6
  ref = C_element
FEATURE [App::DocumentObjectGroupPython] H_element021  label="H_element : 012"  # scripted group (container) (typed FeaturePython)
  n = 10
  ref = H_element
FEATURE [App::DocumentObjectGroupPython] O_element026  label="O_element : 5"  # scripted group (container) (typed FeaturePython)
  n = 5
  ref = O_element
FEATURE [App::DocumentObjectGroupPython] G4_CELLULOSE_CELLOPHANE  # scripted group (container) (typed FeaturePython)
  Dunit = g/cm3
  Dvalue = 1.42
  Group = -> [C_element025,H_element021,O_element026]
  conduct = 2
  density = 1
  expand = 3
  formula = G4_CELLULOSE_CELLOPHANE
  name = G4_CELLULOSE_CELLOPHANE
  specific = 4
FEATURE [App::DocumentObjectGroupPython] H_element022  label="H_element : 0.067"  # scripted group (container) (typed FeaturePython)
  n = 0.067125
FEATURE [App::DocumentObjectGroupPython] C_element026  label="C_element : 0.545"  # scripted group (container) (typed FeaturePython)
  n = 0.545403
FEATURE [App::DocumentObjectGroupPython] O_element027  label="O_element : 0.387"  # scripted group (container) (typed FeaturePython)
  n = 0.387472
FEATURE [App::DocumentObjectGroupPython] G4_CELLULOSE_BUTYRATE  # scripted group (container) (typed FeaturePython)
  Dunit = g/cm3
  Dvalue = 1.2
  Group = -> [H_element022,C_element026,O_element027]
  conduct = 2
  density = 1
  expand = 3
  formula = G4_CELLULOSE_BUTYRATE
  name = G4_CELLULOSE_BUTYRATE
  specific = 4
FEATURE [App::DocumentObjectGroupPython] H_element023  label="H_element : 0.029"  # scripted group (container) (typed FeaturePython)
  n = 0.029216
FEATURE [App::DocumentObjectGroupPython] C_element027  label="C_element : 0.271"  # scripted group (container) (typed FeaturePython)
  n = 0.271296
FEATURE [App::DocumentObjectGroupPython] N_element013  label="N_element : 0.121"  # scripted group (container) (typed FeaturePython)
  n = 0.121276
FEATURE [App::DocumentObjectGroupPython] O_element028  label="O_element : 0.578"  # scripted group (container) (typed FeaturePython)
  n = 0.578212
FEATURE [App::DocumentObjectGroupPython] G4_CELLULOSE_NITRATE  # scripted group (container) (typed FeaturePython)
  Dunit = g/cm3
  Dvalue = 1.49
  Group = -> [H_element023,C_element027,N_element013,O_element028]
  conduct = 2
  density = 1
  expand = 3
  formula = G4_CELLULOSE_NITRATE
  name = G4_CELLULOSE_NITRATE
  specific = 4
FEATURE [App::DocumentObjectGroupPython] H_element024  label="H_element : 0.108"  # scripted group (container) (typed FeaturePython)
  n = 0.107596
FEATURE [App::DocumentObjectGroupPython] N_element014  label="N_element : 0.001"  # scripted group (container) (typed FeaturePython)
  n = 0.0008
FEATURE [App::DocumentObjectGroupPython] O_element029  label="O_element : 0.875"  # scripted group (container) (typed FeaturePython)
  n = 0.874976
FEATURE [App::DocumentObjectGroupPython] S_element008  label="S_element : 0.015"  # scripted group (container) (typed FeaturePython)
  n = 0.014627
FEATURE [App::DocumentObjectGroupPython] Ce_element001  label="Ce_element : 0.002"  # scripted group (container) (typed FeaturePython)
  n = 0.002001
FEATURE [App::DocumentObjectGroupPython] G4_CERIC_SULFATE  # scripted group (container) (typed FeaturePython)
  Dunit = g/cm3
  Dvalue = 1.03
  Group = -> [H_element024,N_element014,O_element029,S_element008,Ce_element001]
  conduct = 2
  density = 1
  expand = 3
  formula = G4_CERIC_SULFATE
  name = G4_CERIC_SULFATE
  specific = 4
FEATURE [App::DocumentObjectGroupPython] Cs_element001  label="Cs_element : 1"  # scripted group (container) (typed FeaturePython)
  n = 1
  ref = Cs_element
FEATURE [App::DocumentObjectGroupPython] F_element006  label="F_element : 1"  # scripted group (container) (typed FeaturePython)
  n = 1
  ref = F_element
FEATURE [App::DocumentObjectGroupPython] G4_CESIUM_FLUORIDE  # scripted group (container) (typed FeaturePython)
  Dunit = g/cm3
  Dvalue = 4.115
  Group = -> [Cs_element001,F_element006]
  conduct = 2
  density = 1
  expand = 3
  formula = G4_CESIUM_FLUORIDE
  name = G4_CESIUM_FLUORIDE
  specific = 4
FEATURE [App::DocumentObjectGroupPython] Cs_element002  label="Cs_element : 002"  # scripted group (container) (typed FeaturePython)
  n = 1
  ref = Cs_element
FEATURE [App::DocumentObjectGroupPython] I_element001  label="I_element : 1"  # scripted group (container) (typed FeaturePython)
  n = 1
  ref = I_element
FEATURE [App::DocumentObjectGroupPython] G4_CESIUM_IODIDE  # scripted group (container) (typed FeaturePython)
  Dunit = g/cm3
  Dvalue = 4.51
  Group = -> [Cs_element002,I_element001]
  conduct = 2
  density = 1
  expand = 3
  formula = G4_CESIUM_IODIDE
  name = G4_CESIUM_IODIDE
  specific = 4
FEATURE [App::DocumentObjectGroupPython] C_element028  label="C_element : 013"  # scripted group (container) (typed FeaturePython)
  n = 6
  ref = C_element
FEATURE [App::DocumentObjectGroupPython] H_element025  label="H_element : 013"  # scripted group (container) (typed FeaturePython)
  n = 5
  ref = H_element
FEATURE [App::DocumentObjectGroupPython] Cl_element005  label="Cl_element : 1"  # scripted group (container) (typed FeaturePython)
  n = 1
  ref = Cl_element
FEATURE [App::DocumentObjectGroupPython] G4_CHLOROBENZENE  # scripted group (container) (typed FeaturePython)
  Dunit = g/cm3
  Dvalue = 1.1058
  Group = -> [C_element028,H_element025,Cl_element005]
  conduct = 2
  density = 1
  expand = 3
  formula = G4_CHLOROBENZENE
  name = G4_CHLOROBENZENE
  specific = 4
FEATURE [App::DocumentObjectGroupPython] C_element029  label="C_element : 014"  # scripted group (container) (typed FeaturePython)
  n = 1
  ref = C_element
FEATURE [App::DocumentObjectGroupPython] H_element026  label="H_element : 1"  # scripted group (container) (typed FeaturePython)
  n = 1
  ref = H_element
FEATURE [App::DocumentObjectGroupPython] Cl_element006  label="Cl_element : 3"  # scripted group (container) (typed FeaturePython)
  n = 3
  ref = Cl_element
FEATURE [App::DocumentObjectGroupPython] G4_CHLOROFORM  # scripted group (container) (typed FeaturePython)
  Dunit = g/cm3
  Dvalue = 1.4832
  Group = -> [C_element029,H_element026,Cl_element006]
  conduct = 2
  density = 1
  expand = 3
  formula = G4_CHLOROFORM
  name = G4_CHLOROFORM
  specific = 4
FEATURE [App::DocumentObjectGroupPython] H_element027  label="H_element : 0.010"  # scripted group (container) (typed FeaturePython)
  n = 0.01
FEATURE [App::DocumentObjectGroupPython] C_element030  label="C_element : 0.001"  # scripted group (container) (typed FeaturePython)
  n = 0.001
FEATURE [App::DocumentObjectGroupPython] O_element030  label="O_element : 0.529"  # scripted group (container) (typed FeaturePython)
  n = 0.529107
FEATURE [App::DocumentObjectGroupPython] Na_element005  label="Na_element : 0.016"  # scripted group (container) (typed FeaturePython)
  n = 0.016
FEATURE [App::DocumentObjectGroupPython] Mg_element003  label="Mg_element : 0.004"  # scripted group (container) (typed FeaturePython)
  n = 0.002
FEATURE [App::DocumentObjectGroupPython] Al_element002  label="Al_element : 0.034"  # scripted group (container) (typed FeaturePython)
  n = 0.033872
FEATURE [App::DocumentObjectGroupPython] Si_element002  label="Si_element : 0.337"  # scripted group (container) (typed FeaturePython)
  n = 0.337021
FEATURE [App::DocumentObjectGroupPython] K_element003  label="K_element : 0.013"  # scripted group (container) (typed FeaturePython)
  n = 0.013
FEATURE [App::DocumentObjectGroupPython] Ca_element010  label="Ca_element : 0.044"  # scripted group (container) (typed FeaturePython)
  n = 0.044
FEATURE [App::DocumentObjectGroupPython] Fe_element002  label="Fe_element : 0.014"  # scripted group (container) (typed FeaturePython)
  n = 0.014
FEATURE [App::DocumentObjectGroupPython] G4_CONCRETE  # scripted group (container) (typed FeaturePython)
  Dunit = g/cm3
  Dvalue = 2.3
  Group = -> [H_element027,C_element030,O_element030,Na_element005,Mg_element003,Al_element002,Si_element002,K_element003,Ca_element010,Fe_element002]
  conduct = 2
  density = 1
  expand = 3
  formula = G4_CONCRETE
  name = G4_CONCRETE
  specific = 4
FEATURE [App::DocumentObjectGroupPython] C_element031  label="C_element : 015"  # scripted group (container) (typed FeaturePython)
  n = 6
  ref = C_element
FEATURE [App::DocumentObjectGroupPython] H_element028  label="H_element : 12"  # scripted group (container) (typed FeaturePython)
  n = 12
  ref = H_element
FEATURE [App::DocumentObjectGroupPython] G4_CYCLOHEXANE  # scripted group (container) (typed FeaturePython)
  Dunit = g/cm3
  Dvalue = 0.779
  Group = -> [C_element031,H_element028]
  conduct = 2
  density = 1
  expand = 3
  formula = G4_CYCLOHEXANE
  name = G4_CYCLOHEXANE
  specific = 4
FEATURE [App::DocumentObjectGroupPython] C_element032  label="C_element : 016"  # scripted group (container) (typed FeaturePython)
  n = 6
  ref = C_element
FEATURE [App::DocumentObjectGroupPython] H_element029  label="H_element : 4"  # scripted group (container) (typed FeaturePython)
  n = 4
  ref = H_element
FEATURE [App::DocumentObjectGroupPython] Cl_element007  label="Cl_element : 2"  # scripted group (container) (typed FeaturePython)
  n = 2
  ref = Cl_element
FEATURE [App::DocumentObjectGroupPython] G4_1_2_DICHLOROBENZENE  label="G4_1.2-DICHLOROBENZENE"  # scripted group (container) (typed FeaturePython)
  Dunit = g/cm3
  Dvalue = 1.3048
  Group = -> [C_element032,H_element029,Cl_element007]
  conduct = 2
  density = 1
  expand = 3
  formula = G4_1.2-DICHLOROBENZENE
  name = G4_1.2-DICHLOROBENZENE
  specific = 4
FEATURE [App::DocumentObjectGroupPython] C_element033  label="C_element : 017"  # scripted group (container) (typed FeaturePython)
  n = 4
  ref = C_element
FEATURE [App::DocumentObjectGroupPython] H_element030  label="H_element : 8"  # scripted group (container) (typed FeaturePython)
  n = 8
  ref = H_element
FEATURE [App::DocumentObjectGroupPython] O_element031  label="O_element : 014"  # scripted group (container) (typed FeaturePython)
  n = 1
  ref = O_element
FEATURE [App::DocumentObjectGroupPython] Cl_element008  label="Cl_element : 005"  # scripted group (container) (typed FeaturePython)
  n = 2
  ref = Cl_element
FEATURE [App::DocumentObjectGroupPython] G4_DICHLORODIETHYL_ETHER  # scripted group (container) (typed FeaturePython)
  Dunit = g/cm3
  Dvalue = 1.2199
  Group = -> [C_element033,H_element030,O_element031,Cl_element008]
  conduct = 2
  density = 1
  expand = 3
  formula = G4_DICHLORODIETHYL_ETHER
  name = G4_DICHLORODIETHYL_ETHER
  specific = 4
FEATURE [App::DocumentObjectGroupPython] C_element034  label="C_element : 018"  # scripted group (container) (typed FeaturePython)
  n = 2
  ref = C_element
FEATURE [App::DocumentObjectGroupPython] H_element031  label="H_element : 014"  # scripted group (container) (typed FeaturePython)
  n = 4
  ref = H_element
FEATURE [App::DocumentObjectGroupPython] Cl_element009  label="Cl_element : 006"  # scripted group (container) (typed FeaturePython)
  n = 2
  ref = Cl_element
FEATURE [App::DocumentObjectGroupPython] G4_1_2_DICHLOROETHANE  label="G4_1.2-DICHLOROETHANE"  # scripted group (container) (typed FeaturePython)
  Dunit = g/cm3
  Dvalue = 1.2351
  Group = -> [C_element034,H_element031,Cl_element009]
  conduct = 2
  density = 1
  expand = 3
  formula = G4_1.2-DICHLOROETHANE
  name = G4_1.2-DICHLOROETHANE
  specific = 4
FEATURE [App::DocumentObjectGroupPython] C_element035  label="C_element : 019"  # scripted group (container) (typed FeaturePython)
  n = 4
  ref = C_element
FEATURE [App::DocumentObjectGroupPython] H_element032  label="H_element : 015"  # scripted group (container) (typed FeaturePython)
  n = 10
  ref = H_element
FEATURE [App::DocumentObjectGroupPython] O_element032  label="O_element : 015"  # scripted group (container) (typed FeaturePython)
  n = 1
  ref = O_element
FEATURE [App::DocumentObjectGroupPython] G4_DIETHYL_ETHER  # scripted group (container) (typed FeaturePython)
  Dunit = g/cm3
  Dvalue = 0.71378
  Group = -> [C_element035,H_element032,O_element032]
  conduct = 2
  density = 1
  expand = 3
  formula = G4_DIETHYL_ETHER
  name = G4_DIETHYL_ETHER
  specific = 4
FEATURE [App::DocumentObjectGroupPython] C_element036  label="C_element : 020"  # scripted group (container) (typed FeaturePython)
  n = 3
  ref = C_element
FEATURE [App::DocumentObjectGroupPython] H_element033  label="H_element : 016"  # scripted group (container) (typed FeaturePython)
  n = 7
  ref = H_element
FEATURE [App::DocumentObjectGroupPython] N_element015  label="N_element : 008"  # scripted group (container) (typed FeaturePython)
  n = 1
  ref = N_element
FEATURE [App::DocumentObjectGroupPython] O_element033  label="O_element : 016"  # scripted group (container) (typed FeaturePython)
  n = 1
  ref = O_element
FEATURE [App::DocumentObjectGroupPython] G4_N_N_DIMETHYL_FORMAMIDE  label="G4_N.N-DIMETHYL_FORMAMIDE"  # scripted group (container) (typed FeaturePython)
  Dunit = g/cm3
  Dvalue = 0.9487
  Group = -> [C_element036,H_element033,N_element015,O_element033]
  conduct = 2
  density = 1
  expand = 3
  formula = G4_N.N-DIMETHYL_FORMAMIDE
  name = G4_N.N-DIMETHYL_FORMAMIDE
  specific = 4
FEATURE [App::DocumentObjectGroupPython] C_element037  label="C_element : 021"  # scripted group (container) (typed FeaturePython)
  n = 2
  ref = C_element
FEATURE [App::DocumentObjectGroupPython] H_element034  label="H_element : 017"  # scripted group (container) (typed FeaturePython)
  n = 6
  ref = H_element
FEATURE [App::DocumentObjectGroupPython] O_element034  label="O_element : 017"  # scripted group (container) (typed FeaturePython)
  n = 1
  ref = O_element
FEATURE [App::DocumentObjectGroupPython] S_element009  label="S_element : 003"  # scripted group (container) (typed FeaturePython)
  n = 1
  ref = S_element
FEATURE [App::DocumentObjectGroupPython] G4_DIMETHYL_SULFOXIDE  # scripted group (container) (typed FeaturePython)
  Dunit = g/cm3
  Dvalue = 1.1014
  Group = -> [C_element037,H_element034,O_element034,S_element009]
  conduct = 2
  density = 1
  expand = 3
  formula = G4_DIMETHYL_SULFOXIDE
  name = G4_DIMETHYL_SULFOXIDE
  specific = 4
FEATURE [App::DocumentObjectGroupPython] C_element038  label="C_element : 022"  # scripted group (container) (typed FeaturePython)
  n = 2
  ref = C_element
FEATURE [App::DocumentObjectGroupPython] H_element035  label="H_element : 018"  # scripted group (container) (typed FeaturePython)
  n = 6
  ref = H_element
FEATURE [App::DocumentObjectGroupPython] G4_ETHANE  # scripted group (container) (typed FeaturePython)
  Dunit = g/cm3
  Dvalue = 0.00125324
  Group = -> [C_element038,H_element035]
  conduct = 2
  density = 1
  expand = 3
  formula = G4_ETHANE
  name = G4_ETHANE
  specific = 4
FEATURE [App::DocumentObjectGroupPython] C_element039  label="C_element : 023"  # scripted group (container) (typed FeaturePython)
  n = 2
  ref = C_element
FEATURE [App::DocumentObjectGroupPython] H_element036  label="H_element : 019"  # scripted group (container) (typed FeaturePython)
  n = 6
  ref = H_element
FEATURE [App::DocumentObjectGroupPython] O_element035  label="O_element : 018"  # scripted group (container) (typed FeaturePython)
  n = 1
  ref = O_element
FEATURE [App::DocumentObjectGroupPython] G4_ETHYL_ALCOHOL  # scripted group (container) (typed FeaturePython)
  Dunit = g/cm3
  Dvalue = 0.7893
  Group = -> [C_element039,H_element036,O_element035]
  conduct = 2
  density = 1
  expand = 3
  formula = G4_ETHYL_ALCOHOL
  name = G4_ETHYL_ALCOHOL
  specific = 4
FEATURE [App::DocumentObjectGroupPython] H_element037  label="H_element : 0.090"  # scripted group (container) (typed FeaturePython)
  n = 0.090027
FEATURE [App::DocumentObjectGroupPython] C_element040  label="C_element : 0.585"  # scripted group (container) (typed FeaturePython)
  n = 0.585182
FEATURE [App::DocumentObjectGroupPython] O_element036  label="O_element : 0.325"  # scripted group (container) (typed FeaturePython)
  n = 0.324791
FEATURE [App::DocumentObjectGroupPython] G4_ETHYL_CELLULOSE  # scripted group (container) (typed FeaturePython)
  Dunit = g/cm3
  Dvalue = 1.13
  Group = -> [H_element037,C_element040,O_element036]
  conduct = 2
  density = 1
  expand = 3
  formula = G4_ETHYL_CELLULOSE
  name = G4_ETHYL_CELLULOSE
  specific = 4
FEATURE [App::DocumentObjectGroupPython] C_element041  label="C_element : 024"  # scripted group (container) (typed FeaturePython)
  n = 2
  ref = C_element
FEATURE [App::DocumentObjectGroupPython] H_element038  label="H_element : 020"  # scripted group (container) (typed FeaturePython)
  n = 4
  ref = H_element
FEATURE [App::DocumentObjectGroupPython] G4_ETHYLENE  # scripted group (container) (typed FeaturePython)
  Dunit = g/cm3
  Dvalue = 0.00117497
  Group = -> [C_element041,H_element038]
  conduct = 2
  density = 1
  expand = 3
  formula = G4_ETHYLENE
  name = G4_ETHYLENE
  specific = 4
FEATURE [App::DocumentObjectGroupPython] H_element039  label="H_element : 0.096"  # scripted group (container) (typed FeaturePython)
  n = 0.096
FEATURE [App::DocumentObjectGroupPython] C_element042  label="C_element : 0.195"  # scripted group (container) (typed FeaturePython)
  n = 0.195
FEATURE [App::DocumentObjectGroupPython] N_element016  label="N_element : 0.057"  # scripted group (container) (typed FeaturePython)
  n = 0.057
FEATURE [App::DocumentObjectGroupPython] O_element037  label="O_element : 0.646"  # scripted group (container) (typed FeaturePython)
  n = 0.646
FEATURE [App::DocumentObjectGroupPython] Na_element006  label="Na_element : 0.017"  # scripted group (container) (typed FeaturePython)
  n = 0.001
FEATURE [App::DocumentObjectGroupPython] P_element005  label="P_element : 0.104"  # scripted group (container) (typed FeaturePython)
  n = 0.001
FEATURE [App::DocumentObjectGroupPython] S_element010  label="S_element : 0.016"  # scripted group (container) (typed FeaturePython)
  n = 0.003
FEATURE [App::DocumentObjectGroupPython] Cl_element010  label="Cl_element : 0.005"  # scripted group (container) (typed FeaturePython)
  n = 0.001
FEATURE [App::DocumentObjectGroupPython] G4_EYE_LENS_ICRP  # scripted group (container) (typed FeaturePython)
  Dunit = g/cm3
  Dvalue = 1.07
  Group = -> [H_element039,C_element042,N_element016,O_element037,Na_element006,P_element005,S_element010,Cl_element010]
  conduct = 2
  density = 1
  expand = 3
  formula = G4_EYE_LENS_ICRP
  name = G4_EYE_LENS_ICRP
  specific = 4
FEATURE [App::DocumentObjectGroupPython] Fe_element003  label="Fe_element : 2"  # scripted group (container) (typed FeaturePython)
  n = 2
  ref = Fe_element
FEATURE [App::DocumentObjectGroupPython] O_element038  label="O_element : 019"  # scripted group (container) (typed FeaturePython)
  n = 3
  ref = O_element
FEATURE [App::DocumentObjectGroupPython] G4_FERRIC_OXIDE  # scripted group (container) (typed FeaturePython)
  Dunit = g/cm3
  Dvalue = 5.2
  Group = -> [Fe_element003,O_element038]
  conduct = 2
  density = 1
  expand = 3
  formula = G4_FERRIC_OXIDE
  name = G4_FERRIC_OXIDE
  specific = 4
FEATURE [App::DocumentObjectGroupPython] Fe_element004  label="Fe_element : 1"  # scripted group (container) (typed FeaturePython)
  n = 1
  ref = Fe_element
FEATURE [App::DocumentObjectGroupPython] B_element003  label="B_element : 1"  # scripted group (container) (typed FeaturePython)
  n = 1
  ref = B_element
FEATURE [App::DocumentObjectGroupPython] G4_FERROBORIDE  # scripted group (container) (typed FeaturePython)
  Dunit = g/cm3
  Dvalue = 7.15
  Group = -> [Fe_element004,B_element003]
  conduct = 2
  density = 1
  expand = 3
  formula = G4_FERROBORIDE
  name = G4_FERROBORIDE
  specific = 4
FEATURE [App::DocumentObjectGroupPython] Fe_element005  label="Fe_element : 003"  # scripted group (container) (typed FeaturePython)
  n = 1
  ref = Fe_element
FEATURE [App::DocumentObjectGroupPython] O_element039  label="O_element : 020"  # scripted group (container) (typed FeaturePython)
  n = 1
  ref = O_element
FEATURE [App::DocumentObjectGroupPython] G4_FERROUS_OXIDE  # scripted group (container) (typed FeaturePython)
  Dunit = g/cm3
  Dvalue = 5.7
  Group = -> [Fe_element005,O_element039]
  conduct = 2
  density = 1
  expand = 3
  formula = G4_FERROUS_OXIDE
  name = G4_FERROUS_OXIDE
  specific = 4
FEATURE [App::DocumentObjectGroupPython] H_element040  label="H_element : 0.115"  # scripted group (container) (typed FeaturePython)
  n = 0.108259
FEATURE [App::DocumentObjectGroupPython] N_element017  label="N_element : 0.000"  # scripted group (container) (typed FeaturePython)
  n = 2.7e-05
FEATURE [App::DocumentObjectGroupPython] O_element040  label="O_element : 0.879"  # scripted group (container) (typed FeaturePython)
  n = 0.878636
FEATURE [App::DocumentObjectGroupPython] Na_element007  label="Na_element : 0.000"  # scripted group (container) (typed FeaturePython)
  n = 2.2e-05
FEATURE [App::DocumentObjectGroupPython] S_element011  label="S_element : 0.013"  # scripted group (container) (typed FeaturePython)
  n = 0.012968
FEATURE [App::DocumentObjectGroupPython] Cl_element011  label="Cl_element : 0.000"  # scripted group (container) (typed FeaturePython)
  n = 3.4e-05
FEATURE [App::DocumentObjectGroupPython] Fe_element006  label="Fe_element : 0.000"  # scripted group (container) (typed FeaturePython)
  n = 5.4e-05
FEATURE [App::DocumentObjectGroupPython] G4_FERROUS_SULFATE  # scripted group (container) (typed FeaturePython)
  Dunit = g/cm3
  Dvalue = 1.024
  Group = -> [H_element040,N_element017,O_element040,Na_element007,S_element011,Cl_element011,Fe_element006]
  conduct = 2
  density = 1
  expand = 3
  formula = G4_FERROUS_SULFATE
  name = G4_FERROUS_SULFATE
  specific = 4
FEATURE [App::DocumentObjectGroupPython] C_element043  label="C_element : 0.099"  # scripted group (container) (typed FeaturePython)
  n = 0.099335
FEATURE [App::DocumentObjectGroupPython] F_element007  label="F_element : 0.314"  # scripted group (container) (typed FeaturePython)
  n = 0.314247
FEATURE [App::DocumentObjectGroupPython] Cl_element012  label="Cl_element : 0.586"  # scripted group (container) (typed FeaturePython)
  n = 0.586418
FEATURE [App::DocumentObjectGroupPython] G4_FREON_12  label="G4_FREON-12"  # scripted group (container) (typed FeaturePython)
  Dunit = g/cm3
  Dvalue = 1.12
  Group = -> [C_element043,F_element007,Cl_element012]
  conduct = 2
  density = 1
  expand = 3
  formula = G4_FREON-12
  name = G4_FREON-12
  specific = 4
FEATURE [App::DocumentObjectGroupPython] C_element044  label="C_element : 0.057"  # scripted group (container) (typed FeaturePython)
  n = 0.057245
FEATURE [App::DocumentObjectGroupPython] F_element008  label="F_element : 0.181"  # scripted group (container) (typed FeaturePython)
  n = 0.181096
FEATURE [App::DocumentObjectGroupPython] Br_element001  label="Br_element : 0.762"  # scripted group (container) (typed FeaturePython)
  n = 0.761659
FEATURE [App::DocumentObjectGroupPython] G4_FREON_12B2  label="G4_FREON-12B2"  # scripted group (container) (typed FeaturePython)
  Dunit = g/cm3
  Dvalue = 1.8
  Group = -> [C_element044,F_element008,Br_element001]
  conduct = 2
  density = 1
  expand = 3
  formula = G4_FREON-12B2
  name = G4_FREON-12B2
  specific = 4
FEATURE [App::DocumentObjectGroupPython] C_element045  label="C_element : 0.115"  # scripted group (container) (typed FeaturePython)
  n = 0.114983
FEATURE [App::DocumentObjectGroupPython] F_element009  label="F_element : 0.546"  # scripted group (container) (typed FeaturePython)
  n = 0.545621
FEATURE [App::DocumentObjectGroupPython] Cl_element013  label="Cl_element : 0.339"  # scripted group (container) (typed FeaturePython)
  n = 0.339396
FEATURE [App::DocumentObjectGroupPython] G4_FREON_13  label="G4_FREON-13"  # scripted group (container) (typed FeaturePython)
  Dunit = g/cm3
  Dvalue = 0.95
  Group = -> [C_element045,F_element009,Cl_element013]
  conduct = 2
  density = 1
  expand = 3
  formula = G4_FREON-13
  name = G4_FREON-13
  specific = 4
FEATURE [App::DocumentObjectGroupPython] C_element046  label="C_element : 025"  # scripted group (container) (typed FeaturePython)
  n = 1
  ref = C_element
FEATURE [App::DocumentObjectGroupPython] F_element010  label="F_element : 3"  # scripted group (container) (typed FeaturePython)
  n = 3
  ref = F_element
FEATURE [App::DocumentObjectGroupPython] Br_element002  label="Br_element : 1"  # scripted group (container) (typed FeaturePython)
  n = 1
  ref = Br_element
FEATURE [App::DocumentObjectGroupPython] G4_FREON_13B1  label="G4_FREON-13B1"  # scripted group (container) (typed FeaturePython)
  Dunit = g/cm3
  Dvalue = 1.5
  Group = -> [C_element046,F_element010,Br_element002]
  conduct = 2
  density = 1
  expand = 3
  formula = G4_FREON-13B1
  name = G4_FREON-13B1
  specific = 4
FEATURE [App::DocumentObjectGroupPython] C_element047  label="C_element : 0.061"  # scripted group (container) (typed FeaturePython)
  n = 0.061309
FEATURE [App::DocumentObjectGroupPython] F_element011  label="F_element : 0.291"  # scripted group (container) (typed FeaturePython)
  n = 0.290924
FEATURE [App::DocumentObjectGroupPython] I_element002  label="I_element : 0.648"  # scripted group (container) (typed FeaturePython)
  n = 0.647767
FEATURE [App::DocumentObjectGroupPython] G4_FREON_13I1  label="G4_FREON-13I1"  # scripted group (container) (typed FeaturePython)
  Dunit = g/cm3
  Dvalue = 1.8
  Group = -> [C_element047,F_element011,I_element002]
  conduct = 2
  density = 1
  expand = 3
  formula = G4_FREON-13I1
  name = G4_FREON-13I1
  specific = 4
FEATURE [App::DocumentObjectGroupPython] Gd_element001  label="Gd_element : 2"  # scripted group (container) (typed FeaturePython)
  n = 2
  ref = Gd_element
FEATURE [App::DocumentObjectGroupPython] O_element041  label="O_element : 021"  # scripted group (container) (typed FeaturePython)
  n = 2
  ref = O_element
FEATURE [App::DocumentObjectGroupPython] S_element012  label="S_element : 004"  # scripted group (container) (typed FeaturePython)
  n = 1
  ref = S_element
FEATURE [App::DocumentObjectGroupPython] G4_GADOLINIUM_OXYSULFIDE  # scripted group (container) (typed FeaturePython)
  Dunit = g/cm3
  Dvalue = 7.44
  Group = -> [Gd_element001,O_element041,S_element012]
  conduct = 2
  density = 1
  expand = 3
  formula = G4_GADOLINIUM_OXYSULFIDE
  name = G4_GADOLINIUM_OXYSULFIDE
  specific = 4
FEATURE [App::DocumentObjectGroupPython] Ga_element001  label="Ga_element : 1"  # scripted group (container) (typed FeaturePython)
  n = 1
  ref = Ga_element
FEATURE [App::DocumentObjectGroupPython] As_element001  label="As_element : 1"  # scripted group (container) (typed FeaturePython)
  n = 1
  ref = As_element
FEATURE [App::DocumentObjectGroupPython] G4_GALLIUM_ARSENIDE  # scripted group (container) (typed FeaturePython)
  Dunit = g/cm3
  Dvalue = 5.31
  Group = -> [Ga_element001,As_element001]
  conduct = 2
  density = 1
  expand = 3
  formula = G4_GALLIUM_ARSENIDE
  name = G4_GALLIUM_ARSENIDE
  specific = 4
FEATURE [App::DocumentObjectGroupPython] H_element041  label="H_element : 0.081"  # scripted group (container) (typed FeaturePython)
  n = 0.08118
FEATURE [App::DocumentObjectGroupPython] C_element048  label="C_element : 0.416"  # scripted group (container) (typed FeaturePython)
  n = 0.41606
FEATURE [App::DocumentObjectGroupPython] N_element018  label="N_element : 0.111"  # scripted group (container) (typed FeaturePython)
  n = 0.11124
FEATURE [App::DocumentObjectGroupPython] O_element042  label="O_element : 0.381"  # scripted group (container) (typed FeaturePython)
  n = 0.38064
FEATURE [App::DocumentObjectGroupPython] S_element013  label="S_element : 0.011"  # scripted group (container) (typed FeaturePython)
  n = 0.01088
FEATURE [App::DocumentObjectGroupPython] G4_GEL_PHOTO_EMULSION  # scripted group (container) (typed FeaturePython)
  Dunit = g/cm3
  Dvalue = 1.2914
  Group = -> [H_element041,C_element048,N_element018,O_element042,S_element013]
  conduct = 2
  density = 1
  expand = 3
  formula = G4_GEL_PHOTO_EMULSION
  name = G4_GEL_PHOTO_EMULSION
  specific = 4
FEATURE [App::DocumentObjectGroupPython] B_element004  label="B_element : 0.040"  # scripted group (container) (typed FeaturePython)
  n = 0.0400639
FEATURE [App::DocumentObjectGroupPython] O_element043  label="O_element : 0.540"  # scripted group (container) (typed FeaturePython)
  n = 0.539561
FEATURE [App::DocumentObjectGroupPython] Na_element008  label="Na_element : 0.028"  # scripted group (container) (typed FeaturePython)
  n = 0.0281909
FEATURE [App::DocumentObjectGroupPython] Al_element003  label="Al_element : 0.012"  # scripted group (container) (typed FeaturePython)
  n = 0.011644
FEATURE [App::DocumentObjectGroupPython] Si_element003  label="Si_element : 0.377"  # scripted group (container) (typed FeaturePython)
  n = 0.377219
FEATURE [App::DocumentObjectGroupPython] K_element004  label="K_element : 0.014"  # scripted group (container) (typed FeaturePython)
  n = 0.00332099
FEATURE [App::DocumentObjectGroupPython] G4_Pyrex_Glass  # scripted group (container) (typed FeaturePython)
  Dunit = g/cm3
  Dvalue = 2.23
  Group = -> [B_element004,O_element043,Na_element008,Al_element003,Si_element003,K_element004]
  conduct = 2
  density = 1
  expand = 3
  formula = G4_Pyrex_Glass
  name = G4_Pyrex_Glass
  specific = 4
FEATURE [App::DocumentObjectGroupPython] O_element044  label="O_element : 0.156"  # scripted group (container) (typed FeaturePython)
  n = 0.156453
FEATURE [App::DocumentObjectGroupPython] Si_element004  label="Si_element : 0.081"  # scripted group (container) (typed FeaturePython)
  n = 0.080866
FEATURE [App::DocumentObjectGroupPython] Ti_element001  label="Ti_element : 0.008"  # scripted group (container) (typed FeaturePython)
  n = 0.008092
FEATURE [App::DocumentObjectGroupPython] As_element002  label="As_element : 0.003"  # scripted group (container) (typed FeaturePython)
  n = 0.002651
FEATURE [App::DocumentObjectGroupPython] Pb_element001  label="Pb_element : 0.752"  # scripted group (container) (typed FeaturePython)
  n = 0.751938
FEATURE [App::DocumentObjectGroupPython] G4_GLASS_LEAD  # scripted group (container) (typed FeaturePython)
  Dunit = g/cm3
  Dvalue = 6.22
  Group = -> [O_element044,Si_element004,Ti_element001,As_element002,Pb_element001]
  conduct = 2
  density = 1
  expand = 3
  formula = G4_GLASS_LEAD
  name = G4_GLASS_LEAD
  specific = 4
FEATURE [App::DocumentObjectGroupPython] O_element045  label="O_element : 0.460"  # scripted group (container) (typed FeaturePython)
  n = 0.4598
FEATURE [App::DocumentObjectGroupPython] Na_element009  label="Na_element : 0.096"  # scripted group (container) (typed FeaturePython)
  n = 0.0964411
FEATURE [App::DocumentObjectGroupPython] Si_element005  label="Si_element : 0.378"  # scripted group (container) (typed FeaturePython)
  n = 0.336553
FEATURE [App::DocumentObjectGroupPython] Ca_element011  label="Ca_element : 0.107"  # scripted group (container) (typed FeaturePython)
  n = 0.107205
FEATURE [App::DocumentObjectGroupPython] G4_GLASS_PLATE  # scripted group (container) (typed FeaturePython)
  Dunit = g/cm3
  Dvalue = 2.4
  Group = -> [O_element045,Na_element009,Si_element005,Ca_element011]
  conduct = 2
  density = 1
  expand = 3
  formula = G4_GLASS_PLATE
  name = G4_GLASS_PLATE
  specific = 4
FEATURE [App::DocumentObjectGroupPython] C_element049  label="C_element : 026"  # scripted group (container) (typed FeaturePython)
  n = 5
  ref = C_element
FEATURE [App::DocumentObjectGroupPython] H_element042  label="H_element : 021"  # scripted group (container) (typed FeaturePython)
  n = 10
  ref = H_element
FEATURE [App::DocumentObjectGroupPython] N_element019  label="N_element : 2"  # scripted group (container) (typed FeaturePython)
  n = 2
  ref = N_element
FEATURE [App::DocumentObjectGroupPython] O_element046  label="O_element : 022"  # scripted group (container) (typed FeaturePython)
  n = 3
  ref = O_element
FEATURE [App::DocumentObjectGroupPython] G4_GLUTAMINE  # scripted group (container) (typed FeaturePython)
  Dunit = g/cm3
  Dvalue = 1.46
  Group = -> [C_element049,H_element042,N_element019,O_element046]
  conduct = 2
  density = 1
  expand = 3
  formula = G4_GLUTAMINE
  name = G4_GLUTAMINE
  specific = 4
FEATURE [App::DocumentObjectGroupPython] C_element050  label="C_element : 027"  # scripted group (container) (typed FeaturePython)
  n = 3
  ref = C_element
FEATURE [App::DocumentObjectGroupPython] H_element043  label="H_element : 022"  # scripted group (container) (typed FeaturePython)
  n = 8
  ref = H_element
FEATURE [App::DocumentObjectGroupPython] O_element047  label="O_element : 023"  # scripted group (container) (typed FeaturePython)
  n = 3
  ref = O_element
FEATURE [App::DocumentObjectGroupPython] G4_GLYCEROL  # scripted group (container) (typed FeaturePython)
  Dunit = g/cm3
  Dvalue = 1.2613
  Group = -> [C_element050,H_element043,O_element047]
  conduct = 2
  density = 1
  expand = 3
  formula = G4_GLYCEROL
  name = G4_GLYCEROL
  specific = 4
FEATURE [App::DocumentObjectGroupPython] C_element051  label="C_element : 028"  # scripted group (container) (typed FeaturePython)
  n = 5
  ref = C_element
FEATURE [App::DocumentObjectGroupPython] H_element044  label="H_element : 023"  # scripted group (container) (typed FeaturePython)
  n = 5
  ref = H_element
FEATURE [App::DocumentObjectGroupPython] N_element020  label="N_element : 009"  # scripted group (container) (typed FeaturePython)
  n = 5
  ref = N_element
FEATURE [App::DocumentObjectGroupPython] O_element048  label="O_element : 024"  # scripted group (container) (typed FeaturePython)
  n = 1
  ref = O_element
FEATURE [App::DocumentObjectGroupPython] G4_GUANINE  # scripted group (container) (typed FeaturePython)
  Dunit = g/cm3
  Dvalue = 2.2
  Group = -> [C_element051,H_element044,N_element020,O_element048]
  conduct = 2
  density = 1
  expand = 3
  formula = G4_GUANINE
  name = G4_GUANINE
  specific = 4
FEATURE [App::DocumentObjectGroupPython] Ca_element012  label="Ca_element : 006"  # scripted group (container) (typed FeaturePython)
  n = 1
  ref = Ca_element
FEATURE [App::DocumentObjectGroupPython] S_element014  label="S_element : 005"  # scripted group (container) (typed FeaturePython)
  n = 1
  ref = S_element
FEATURE [App::DocumentObjectGroupPython] O_element049  label="O_element : 6"  # scripted group (container) (typed FeaturePython)
  n = 6
  ref = O_element
FEATURE [App::DocumentObjectGroupPython] H_element045  label="H_element : 024"  # scripted group (container) (typed FeaturePython)
  n = 4
  ref = H_element
FEATURE [App::DocumentObjectGroupPython] G4_GYPSUM  # scripted group (container) (typed FeaturePython)
  Dunit = g/cm3
  Dvalue = 2.32
  Group = -> [Ca_element012,S_element014,O_element049,H_element045]
  conduct = 2
  density = 1
  expand = 3
  formula = G4_GYPSUM
  name = G4_GYPSUM
  specific = 4
FEATURE [App::DocumentObjectGroupPython] C_element052  label="C_element : 7"  # scripted group (container) (typed FeaturePython)
  n = 7
  ref = C_element
FEATURE [App::DocumentObjectGroupPython] H_element046  label="H_element : 16"  # scripted group (container) (typed FeaturePython)
  n = 16
  ref = H_element
FEATURE [App::DocumentObjectGroupPython] G4_N_HEPTANE  label="G4_N-HEPTANE"  # scripted group (container) (typed FeaturePython)
  Dunit = g/cm3
  Dvalue = 0.68376
  Group = -> [C_element052,H_element046]
  conduct = 2
  density = 1
  expand = 3
  formula = G4_N-HEPTANE
  name = G4_N-HEPTANE
  specific = 4
FEATURE [App::DocumentObjectGroupPython] C_element053  label="C_element : 029"  # scripted group (container) (typed FeaturePython)
  n = 6
  ref = C_element
FEATURE [App::DocumentObjectGroupPython] H_element047  label="H_element : 14"  # scripted group (container) (typed FeaturePython)
  n = 14
  ref = H_element
FEATURE [App::DocumentObjectGroupPython] G4_N_HEXANE  label="G4_N-HEXANE"  # scripted group (container) (typed FeaturePython)
  Dunit = g/cm3
  Dvalue = 0.6603
  Group = -> [C_element053,H_element047]
  conduct = 2
  density = 1
  expand = 3
  formula = G4_N-HEXANE
  name = G4_N-HEXANE
  specific = 4
FEATURE [App::DocumentObjectGroupPython] C_element054  label="C_element : 22"  # scripted group (container) (typed FeaturePython)
  n = 22
  ref = C_element
FEATURE [App::DocumentObjectGroupPython] H_element048  label="H_element : 025"  # scripted group (container) (typed FeaturePython)
  n = 10
  ref = H_element
FEATURE [App::DocumentObjectGroupPython] N_element021  label="N_element : 010"  # scripted group (container) (typed FeaturePython)
  n = 2
  ref = N_element
FEATURE [App::DocumentObjectGroupPython] O_element050  label="O_element : 025"  # scripted group (container) (typed FeaturePython)
  n = 5
  ref = O_element
FEATURE [App::DocumentObjectGroupPython] G4_KAPTON  # scripted group (container) (typed FeaturePython)
  Dunit = g/cm3
  Dvalue = 1.42
  Group = -> [C_element054,H_element048,N_element021,O_element050]
  conduct = 2
  density = 1
  expand = 3
  formula = G4_KAPTON
  name = G4_KAPTON
  specific = 4
FEATURE [App::DocumentObjectGroupPython] La_element001  label="La_element : 1"  # scripted group (container) (typed FeaturePython)
  n = 1
  ref = La_element
FEATURE [App::DocumentObjectGroupPython] Br_element003  label="Br_element : 002"  # scripted group (container) (typed FeaturePython)
  n = 1
  ref = Br_element
FEATURE [App::DocumentObjectGroupPython] O_element051  label="O_element : 026"  # scripted group (container) (typed FeaturePython)
  n = 1
  ref = O_element
FEATURE [App::DocumentObjectGroupPython] G4_LANTHANUM_OXYBROMIDE  # scripted group (container) (typed FeaturePython)
  Dunit = g/cm3
  Dvalue = 6.28
  Group = -> [La_element001,Br_element003,O_element051]
  conduct = 2
  density = 1
  expand = 3
  formula = G4_LANTHANUM_OXYBROMIDE
  name = G4_LANTHANUM_OXYBROMIDE
  specific = 4
FEATURE [App::DocumentObjectGroupPython] La_element002  label="La_element : 2"  # scripted group (container) (typed FeaturePython)
  n = 2
  ref = La_element
FEATURE [App::DocumentObjectGroupPython] O_element052  label="O_element : 027"  # scripted group (container) (typed FeaturePython)
  n = 2
  ref = O_element
FEATURE [App::DocumentObjectGroupPython] S_element015  label="S_element : 006"  # scripted group (container) (typed FeaturePython)
  n = 1
  ref = S_element
FEATURE [App::DocumentObjectGroupPython] G4_LANTHANUM_OXYSULFIDE  # scripted group (container) (typed FeaturePython)
  Dunit = g/cm3
  Dvalue = 5.86
  Group = -> [La_element002,O_element052,S_element015]
  conduct = 2
  density = 1
  expand = 3
  formula = G4_LANTHANUM_OXYSULFIDE
  name = G4_LANTHANUM_OXYSULFIDE
  specific = 4
FEATURE [App::DocumentObjectGroupPython] O_element053  label="O_element : 0.072"  # scripted group (container) (typed FeaturePython)
  n = 0.071682
FEATURE [App::DocumentObjectGroupPython] Pb_element002  label="Pb_element : 0.928"  # scripted group (container) (typed FeaturePython)
  n = 0.928318
FEATURE [App::DocumentObjectGroupPython] G4_LEAD_OXIDE  # scripted group (container) (typed FeaturePython)
  Dunit = g/cm3
  Dvalue = 9.53
  Group = -> [O_element053,Pb_element002]
  conduct = 2
  density = 1
  expand = 3
  formula = G4_LEAD_OXIDE
  name = G4_LEAD_OXIDE
  specific = 4
FEATURE [App::DocumentObjectGroupPython] Li_element001  label="Li_element : 1"  # scripted group (container) (typed FeaturePython)
  n = 1
  ref = Li_element
FEATURE [App::DocumentObjectGroupPython] N_element022  label="N_element : 011"  # scripted group (container) (typed FeaturePython)
  n = 1
  ref = N_element
FEATURE [App::DocumentObjectGroupPython] H_element049  label="H_element : 026"  # scripted group (container) (typed FeaturePython)
  n = 2
  ref = H_element
FEATURE [App::DocumentObjectGroupPython] G4_LITHIUM_AMIDE  # scripted group (container) (typed FeaturePython)
  Dunit = g/cm3
  Dvalue = 1.178
  Group = -> [Li_element001,N_element022,H_element049]
  conduct = 2
  density = 1
  expand = 3
  formula = G4_LITHIUM_AMIDE
  name = G4_LITHIUM_AMIDE
  specific = 4
FEATURE [App::DocumentObjectGroupPython] Li_element002  label="Li_element : 2"  # scripted group (container) (typed FeaturePython)
  n = 2
  ref = Li_element
FEATURE [App::DocumentObjectGroupPython] C_element055  label="C_element : 030"  # scripted group (container) (typed FeaturePython)
  n = 1
  ref = C_element
FEATURE [App::DocumentObjectGroupPython] O_element054  label="O_element : 028"  # scripted group (container) (typed FeaturePython)
  n = 3
  ref = O_element
FEATURE [App::DocumentObjectGroupPython] G4_LITHIUM_CARBONATE  # scripted group (container) (typed FeaturePython)
  Dunit = g/cm3
  Dvalue = 2.11
  Group = -> [Li_element002,C_element055,O_element054]
  conduct = 2
  density = 1
  expand = 3
  formula = G4_LITHIUM_CARBONATE
  name = G4_LITHIUM_CARBONATE
  specific = 4
FEATURE [App::DocumentObjectGroupPython] Li_element003  label="Li_element : 003"  # scripted group (container) (typed FeaturePython)
  n = 1
  ref = Li_element
FEATURE [App::DocumentObjectGroupPython] F_element012  label="F_element : 004"  # scripted group (container) (typed FeaturePython)
  n = 1
  ref = F_element
FEATURE [App::DocumentObjectGroupPython] G4_LITHIUM_FLUORIDE  # scripted group (container) (typed FeaturePython)
  Dunit = g/cm3
  Dvalue = 2.635
  Group = -> [Li_element003,F_element012]
  conduct = 2
  density = 1
  expand = 3
  formula = G4_LITHIUM_FLUORIDE
  name = G4_LITHIUM_FLUORIDE
  specific = 4
FEATURE [App::DocumentObjectGroupPython] Li_element004  label="Li_element : 004"  # scripted group (container) (typed FeaturePython)
  n = 1
  ref = Li_element
FEATURE [App::DocumentObjectGroupPython] H_element050  label="H_element : 027"  # scripted group (container) (typed FeaturePython)
  n = 1
  ref = H_element
FEATURE [App::DocumentObjectGroupPython] G4_LITHIUM_HYDRIDE  # scripted group (container) (typed FeaturePython)
  Dunit = g/cm3
  Dvalue = 0.82
  Group = -> [Li_element004,H_element050]
  conduct = 2
  density = 1
  expand = 3
  formula = G4_LITHIUM_HYDRIDE
  name = G4_LITHIUM_HYDRIDE
  specific = 4
FEATURE [App::DocumentObjectGroupPython] Li_element005  label="Li_element : 005"  # scripted group (container) (typed FeaturePython)
  n = 1
  ref = Li_element
FEATURE [App::DocumentObjectGroupPython] I_element003  label="I_element : 002"  # scripted group (container) (typed FeaturePython)
  n = 1
  ref = I_element
FEATURE [App::DocumentObjectGroupPython] G4_LITHIUM_IODIDE  # scripted group (container) (typed FeaturePython)
  Dunit = g/cm3
  Dvalue = 3.494
  Group = -> [Li_element005,I_element003]
  conduct = 2
  density = 1
  expand = 3
  formula = G4_LITHIUM_IODIDE
  name = G4_LITHIUM_IODIDE
  specific = 4
FEATURE [App::DocumentObjectGroupPython] Li_element006  label="Li_element : 006"  # scripted group (container) (typed FeaturePython)
  n = 2
  ref = Li_element
FEATURE [App::DocumentObjectGroupPython] O_element055  label="O_element : 029"  # scripted group (container) (typed FeaturePython)
  n = 1
  ref = O_element
FEATURE [App::DocumentObjectGroupPython] G4_LITHIUM_OXIDE  # scripted group (container) (typed FeaturePython)
  Dunit = g/cm3
  Dvalue = 2.013
  Group = -> [Li_element006,O_element055]
  conduct = 2
  density = 1
  expand = 3
  formula = G4_LITHIUM_OXIDE
  name = G4_LITHIUM_OXIDE
  specific = 4
FEATURE [App::DocumentObjectGroupPython] Li_element007  label="Li_element : 007"  # scripted group (container) (typed FeaturePython)
  n = 2
  ref = Li_element
FEATURE [App::DocumentObjectGroupPython] B_element005  label="B_element : 005"  # scripted group (container) (typed FeaturePython)
  n = 4
  ref = B_element
FEATURE [App::DocumentObjectGroupPython] O_element056  label="O_element : 7"  # scripted group (container) (typed FeaturePython)
  n = 7
  ref = O_element
FEATURE [App::DocumentObjectGroupPython] G4_LITHIUM_TETRABORATE  # scripted group (container) (typed FeaturePython)
  Dunit = g/cm3
  Dvalue = 2.44
  Group = -> [Li_element007,B_element005,O_element056]
  conduct = 2
  density = 1
  expand = 3
  formula = G4_LITHIUM_TETRABORATE
  name = G4_LITHIUM_TETRABORATE
  specific = 4
FEATURE [App::DocumentObjectGroupPython] H_element051  label="H_element : 0.105"  # scripted group (container) (typed FeaturePython)
  n = 0.105
FEATURE [App::DocumentObjectGroupPython] C_element056  label="C_element : 0.083"  # scripted group (container) (typed FeaturePython)
  n = 0.083
FEATURE [App::DocumentObjectGroupPython] N_element023  label="N_element : 0.023"  # scripted group (container) (typed FeaturePython)
  n = 0.023
FEATURE [App::DocumentObjectGroupPython] O_element057  label="O_element : 0.779"  # scripted group (container) (typed FeaturePython)
  n = 0.779
FEATURE [App::DocumentObjectGroupPython] Na_element010  label="Na_element : 0.097"  # scripted group (container) (typed FeaturePython)
  n = 0.002
FEATURE [App::DocumentObjectGroupPython] P_element006  label="P_element : 0.105"  # scripted group (container) (typed FeaturePython)
  n = 0.001
FEATURE [App::DocumentObjectGroupPython] S_element016  label="S_element : 0.017"  # scripted group (container) (typed FeaturePython)
  n = 0.002
FEATURE [App::DocumentObjectGroupPython] Cl_element014  label="Cl_element : 0.587"  # scripted group (container) (typed FeaturePython)
  n = 0.003
FEATURE [App::DocumentObjectGroupPython] K_element005  label="K_element : 0.015"  # scripted group (container) (typed FeaturePython)
  n = 0.002
FEATURE [App::DocumentObjectGroupPython] G4_LUNG_ICRP  # scripted group (container) (typed FeaturePython)
  Dunit = g/cm3
  Dvalue = 1.04
  Group = -> [H_element051,C_element056,N_element023,O_element057,Na_element010,P_element006,S_element016,Cl_element014,K_element005]
  conduct = 2
  density = 1
  expand = 3
  formula = G4_LUNG_ICRP
  name = G4_LUNG_ICRP
  specific = 4
FEATURE [App::DocumentObjectGroupPython] H_element052  label="H_element : 0.116"  # scripted group (container) (typed FeaturePython)
  n = 0.114318
FEATURE [App::DocumentObjectGroupPython] C_element057  label="C_element : 0.656"  # scripted group (container) (typed FeaturePython)
  n = 0.655824
FEATURE [App::DocumentObjectGroupPython] O_element058  label="O_element : 0.092"  # scripted group (container) (typed FeaturePython)
  n = 0.0921831
FEATURE [App::DocumentObjectGroupPython] Mg_element004  label="Mg_element : 0.135"  # scripted group (container) (typed FeaturePython)
  n = 0.134792
FEATURE [App::DocumentObjectGroupPython] Ca_element013  label="Ca_element : 0.003"  # scripted group (container) (typed FeaturePython)
  n = 0.002883
FEATURE [App::DocumentObjectGroupPython] G4_M3_WAX  # scripted group (container) (typed FeaturePython)
  Dunit = g/cm3
  Dvalue = 1.05
  Group = -> [H_element052,C_element057,O_element058,Mg_element004,Ca_element013]
  conduct = 2
  density = 1
  expand = 3
  formula = G4_M3_WAX
  name = G4_M3_WAX
  specific = 4
FEATURE [App::DocumentObjectGroupPython] Mg_element005  label="Mg_element : 1"  # scripted group (container) (typed FeaturePython)
  n = 1
  ref = Mg_element
FEATURE [App::DocumentObjectGroupPython] C_element058  label="C_element : 031"  # scripted group (container) (typed FeaturePython)
  n = 1
  ref = C_element
FEATURE [App::DocumentObjectGroupPython] O_element059  label="O_element : 030"  # scripted group (container) (typed FeaturePython)
  n = 3
  ref = O_element
FEATURE [App::DocumentObjectGroupPython] G4_MAGNESIUM_CARBONATE  # scripted group (container) (typed FeaturePython)
  Dunit = g/cm3
  Dvalue = 2.958
  Group = -> [Mg_element005,C_element058,O_element059]
  conduct = 2
  density = 1
  expand = 3
  formula = G4_MAGNESIUM_CARBONATE
  name = G4_MAGNESIUM_CARBONATE
  specific = 4
FEATURE [App::DocumentObjectGroupPython] Mg_element006  label="Mg_element : 002"  # scripted group (container) (typed FeaturePython)
  n = 1
  ref = Mg_element
FEATURE [App::DocumentObjectGroupPython] F_element013  label="F_element : 005"  # scripted group (container) (typed FeaturePython)
  n = 2
  ref = F_element
FEATURE [App::DocumentObjectGroupPython] G4_MAGNESIUM_FLUORIDE  # scripted group (container) (typed FeaturePython)
  Dunit = g/cm3
  Dvalue = 3
  Group = -> [Mg_element006,F_element013]
  conduct = 2
  density = 1
  expand = 3
  formula = G4_MAGNESIUM_FLUORIDE
  name = G4_MAGNESIUM_FLUORIDE
  specific = 4
FEATURE [App::DocumentObjectGroupPython] Mg_element007  label="Mg_element : 003"  # scripted group (container) (typed FeaturePython)
  n = 1
  ref = Mg_element
FEATURE [App::DocumentObjectGroupPython] O_element060  label="O_element : 031"  # scripted group (container) (typed FeaturePython)
  n = 1
  ref = O_element
FEATURE [App::DocumentObjectGroupPython] G4_MAGNESIUM_OXIDE  # scripted group (container) (typed FeaturePython)
  Dunit = g/cm3
  Dvalue = 3.58
  Group = -> [Mg_element007,O_element060]
  conduct = 2
  density = 1
  expand = 3
  formula = G4_MAGNESIUM_OXIDE
  name = G4_MAGNESIUM_OXIDE
  specific = 4
FEATURE [App::DocumentObjectGroupPython] Mg_element008  label="Mg_element : 004"  # scripted group (container) (typed FeaturePython)
  n = 1
  ref = Mg_element
FEATURE [App::DocumentObjectGroupPython] B_element006  label="B_element : 006"  # scripted group (container) (typed FeaturePython)
  n = 4
  ref = B_element
FEATURE [App::DocumentObjectGroupPython] O_element061  label="O_element : 032"  # scripted group (container) (typed FeaturePython)
  n = 7
  ref = O_element
FEATURE [App::DocumentObjectGroupPython] G4_MAGNESIUM_TETRABORATE  # scripted group (container) (typed FeaturePython)
  Dunit = g/cm3
  Dvalue = 2.53
  Group = -> [Mg_element008,B_element006,O_element061]
  conduct = 2
  density = 1
  expand = 3
  formula = G4_MAGNESIUM_TETRABORATE
  name = G4_MAGNESIUM_TETRABORATE
  specific = 4
FEATURE [App::DocumentObjectGroupPython] Hg_element001  label="Hg_element : 1"  # scripted group (container) (typed FeaturePython)
  n = 1
  ref = Hg_element
FEATURE [App::DocumentObjectGroupPython] I_element004  label="I_element : 2"  # scripted group (container) (typed FeaturePython)
  n = 2
  ref = I_element
FEATURE [App::DocumentObjectGroupPython] G4_MERCURIC_IODIDE  # scripted group (container) (typed FeaturePython)
  Dunit = g/cm3
  Dvalue = 6.36
  Group = -> [Hg_element001,I_element004]
  conduct = 2
  density = 1
  expand = 3
  formula = G4_MERCURIC_IODIDE
  name = G4_MERCURIC_IODIDE
  specific = 4
FEATURE [App::DocumentObjectGroupPython] C_element059  label="C_element : 032"  # scripted group (container) (typed FeaturePython)
  n = 1
  ref = C_element
FEATURE [App::DocumentObjectGroupPython] H_element053  label="H_element : 028"  # scripted group (container) (typed FeaturePython)
  n = 4
  ref = H_element
FEATURE [App::DocumentObjectGroupPython] G4_METHANE  # scripted group (container) (typed FeaturePython)
  Dunit = g/cm3
  Dvalue = 0.000667151
  Group = -> [C_element059,H_element053]
  conduct = 2
  density = 1
  expand = 3
  formula = G4_METHANE
  name = G4_METHANE
  specific = 4
FEATURE [App::DocumentObjectGroupPython] C_element060  label="C_element : 033"  # scripted group (container) (typed FeaturePython)
  n = 1
  ref = C_element
FEATURE [App::DocumentObjectGroupPython] H_element054  label="H_element : 029"  # scripted group (container) (typed FeaturePython)
  n = 4
  ref = H_element
FEATURE [App::DocumentObjectGroupPython] O_element062  label="O_element : 033"  # scripted group (container) (typed FeaturePython)
  n = 1
  ref = O_element
FEATURE [App::DocumentObjectGroupPython] G4_METHANOL  # scripted group (container) (typed FeaturePython)
  Dunit = g/cm3
  Dvalue = 0.7914
  Group = -> [C_element060,H_element054,O_element062]
  conduct = 2
  density = 1
  expand = 3
  formula = G4_METHANOL
  name = G4_METHANOL
  specific = 4
FEATURE [App::DocumentObjectGroupPython] H_element055  label="H_element : 0.134"  # scripted group (container) (typed FeaturePython)
  n = 0.13404
FEATURE [App::DocumentObjectGroupPython] C_element061  label="C_element : 0.778"  # scripted group (container) (typed FeaturePython)
  n = 0.77796
FEATURE [App::DocumentObjectGroupPython] O_element063  label="O_element : 0.035"  # scripted group (container) (typed FeaturePython)
  n = 0.03502
FEATURE [App::DocumentObjectGroupPython] Mg_element009  label="Mg_element : 0.039"  # scripted group (container) (typed FeaturePython)
  n = 0.038594
FEATURE [App::DocumentObjectGroupPython] Ti_element002  label="Ti_element : 0.014"  # scripted group (container) (typed FeaturePython)
  n = 0.014386
FEATURE [App::DocumentObjectGroupPython] G4_MIX_D_WAX  # scripted group (container) (typed FeaturePython)
  Dunit = g/cm3
  Dvalue = 0.99
  Group = -> [H_element055,C_element061,O_element063,Mg_element009,Ti_element002]
  conduct = 2
  density = 1
  expand = 3
  formula = G4_MIX_D_WAX
  name = G4_MIX_D_WAX
  specific = 4
FEATURE [App::DocumentObjectGroupPython] H_element056  label="H_element : 0.135"  # scripted group (container) (typed FeaturePython)
  n = 0.081192
FEATURE [App::DocumentObjectGroupPython] C_element062  label="C_element : 0.583"  # scripted group (container) (typed FeaturePython)
  n = 0.583442
FEATURE [App::DocumentObjectGroupPython] N_element024  label="N_element : 0.018"  # scripted group (container) (typed FeaturePython)
  n = 0.017798
FEATURE [App::DocumentObjectGroupPython] O_element064  label="O_element : 0.186"  # scripted group (container) (typed FeaturePython)
  n = 0.186381
FEATURE [App::DocumentObjectGroupPython] Mg_element010  label="Mg_element : 0.130"  # scripted group (container) (typed FeaturePython)
  n = 0.130287
FEATURE [App::DocumentObjectGroupPython] Cl_element015  label="Cl_element : 0.588"  # scripted group (container) (typed FeaturePython)
  n = 0.0009
FEATURE [App::DocumentObjectGroupPython] G4_MS20_TISSUE  # scripted group (container) (typed FeaturePython)
  Dunit = g/cm3
  Dvalue = 1
  Group = -> [H_element056,C_element062,N_element024,O_element064,Mg_element010,Cl_element015]
  conduct = 2
  density = 1
  expand = 3
  formula = G4_MS20_TISSUE
  name = G4_MS20_TISSUE
  specific = 4
FEATURE [App::DocumentObjectGroupPython] H_element057  label="H_element : 0.136"  # scripted group (container) (typed FeaturePython)
  n = 0.102
FEATURE [App::DocumentObjectGroupPython] C_element063  label="C_element : 0.143"  # scripted group (container) (typed FeaturePython)
  n = 0.143
FEATURE [App::DocumentObjectGroupPython] N_element025  label="N_element : 0.034"  # scripted group (container) (typed FeaturePython)
  n = 0.034
FEATURE [App::DocumentObjectGroupPython] O_element065  label="O_element : 0.710"  # scripted group (container) (typed FeaturePython)
  n = 0.71
FEATURE [App::DocumentObjectGroupPython] Na_element011  label="Na_element : 0.098"  # scripted group (container) (typed FeaturePython)
  n = 0.001
FEATURE [App::DocumentObjectGroupPython] P_element007  label="P_element : 0.002"  # scripted group (container) (typed FeaturePython)
  n = 0.002
FEATURE [App::DocumentObjectGroupPython] S_element017  label="S_element : 0.018"  # scripted group (container) (typed FeaturePython)
  n = 0.003
FEATURE [App::DocumentObjectGroupPython] Cl_element016  label="Cl_element : 0.589"  # scripted group (container) (typed FeaturePython)
  n = 0.001
FEATURE [App::DocumentObjectGroupPython] K_element006  label="K_element : 0.004"  # scripted group (container) (typed FeaturePython)
  n = 0.004
FEATURE [App::DocumentObjectGroupPython] G4_MUSCLE_SKELETAL_ICRP  # scripted group (container) (typed FeaturePython)
  Dunit = g/cm3
  Dvalue = 1.05
  Group = -> [H_element057,C_element063,N_element025,O_element065,Na_element011,P_element007,S_element017,Cl_element016,K_element006]
  conduct = 2
  density = 1
  expand = 3
  formula = G4_MUSCLE_SKELETAL_ICRP
  name = G4_MUSCLE_SKELETAL_ICRP
  specific = 4
FEATURE [App::DocumentObjectGroupPython] H_element058  label="H_element : 0.137"  # scripted group (container) (typed FeaturePython)
  n = 0.102102
FEATURE [App::DocumentObjectGroupPython] C_element064  label="C_element : 0.123"  # scripted group (container) (typed FeaturePython)
  n = 0.123123
FEATURE [App::DocumentObjectGroupPython] N_element026  label="N_element : 0.756"  # scripted group (container) (typed FeaturePython)
  n = 0.035035
FEATURE [App::DocumentObjectGroupPython] O_element066  label="O_element : 0.730"  # scripted group (container) (typed FeaturePython)
  n = 0.72973
FEATURE [App::DocumentObjectGroupPython] Na_element012  label="Na_element : 0.099"  # scripted group (container) (typed FeaturePython)
  n = 0.001001
FEATURE [App::DocumentObjectGroupPython] P_element008  label="P_element : 0.106"  # scripted group (container) (typed FeaturePython)
  n = 0.002002
FEATURE [App::DocumentObjectGroupPython] S_element018  label="S_element : 0.019"  # scripted group (container) (typed FeaturePython)
  n = 0.004004
FEATURE [App::DocumentObjectGroupPython] K_element007  label="K_element : 0.016"  # scripted group (container) (typed FeaturePython)
  n = 0.003003
FEATURE [App::DocumentObjectGroupPython] G4_MUSCLE_STRIATED_ICRU  # scripted group (container) (typed FeaturePython)
  Dunit = g/cm3
  Dvalue = 1.04
  Group = -> [H_element058,C_element064,N_element026,O_element066,Na_element012,P_element008,S_element018,K_element007]
  conduct = 2
  density = 1
  expand = 3
  formula = G4_MUSCLE_STRIATED_ICRU
  name = G4_MUSCLE_STRIATED_ICRU
  specific = 4
FEATURE [App::DocumentObjectGroupPython] H_element059  label="H_element : 0.098"  # scripted group (container) (typed FeaturePython)
  n = 0.0982341
FEATURE [App::DocumentObjectGroupPython] C_element065  label="C_element : 0.156"  # scripted group (container) (typed FeaturePython)
  n = 0.156214
FEATURE [App::DocumentObjectGroupPython] N_element027  label="N_element : 0.757"  # scripted group (container) (typed FeaturePython)
  n = 0.035451
FEATURE [App::DocumentObjectGroupPython] O_element067  label="O_element : 0.880"  # scripted group (container) (typed FeaturePython)
  n = 0.710101
FEATURE [App::DocumentObjectGroupPython] G4_MUSCLE_WITH_SUCROSE  # scripted group (container) (typed FeaturePython)
  Dunit = g/cm3
  Dvalue = 1.11
  Group = -> [H_element059,C_element065,N_element027,O_element067]
  conduct = 2
  density = 1
  expand = 3
  formula = G4_MUSCLE_WITH_SUCROSE
  name = G4_MUSCLE_WITH_SUCROSE
  specific = 4
FEATURE [App::DocumentObjectGroupPython] H_element060  label="H_element : 0.138"  # scripted group (container) (typed FeaturePython)
  n = 0.101969
FEATURE [App::DocumentObjectGroupPython] C_element066  label="C_element : 0.120"  # scripted group (container) (typed FeaturePython)
  n = 0.120058
FEATURE [App::DocumentObjectGroupPython] N_element028  label="N_element : 0.758"  # scripted group (container) (typed FeaturePython)
  n = 0.035451
FEATURE [App::DocumentObjectGroupPython] O_element068  label="O_element : 0.743"  # scripted group (container) (typed FeaturePython)
  n = 0.742522
FEATURE [App::DocumentObjectGroupPython] G4_MUSCLE_WITHOUT_SUCROSE  # scripted group (container) (typed FeaturePython)
  Dunit = g/cm3
  Dvalue = 1.07
  Group = -> [H_element060,C_element066,N_element028,O_element068]
  conduct = 2
  density = 1
  expand = 3
  formula = G4_MUSCLE_WITHOUT_SUCROSE
  name = G4_MUSCLE_WITHOUT_SUCROSE
  specific = 4
FEATURE [App::DocumentObjectGroupPython] C_element067  label="C_element : 10"  # scripted group (container) (typed FeaturePython)
  n = 10
  ref = C_element
FEATURE [App::DocumentObjectGroupPython] H_element061  label="H_element : 030"  # scripted group (container) (typed FeaturePython)
  n = 8
  ref = H_element
FEATURE [App::DocumentObjectGroupPython] G4_NAPHTHALENE  # scripted group (container) (typed FeaturePython)
  Dunit = g/cm3
  Dvalue = 1.145
  Group = -> [C_element067,H_element061]
  conduct = 2
  density = 1
  expand = 3
  formula = G4_NAPHTHALENE
  name = G4_NAPHTHALENE
  specific = 4
FEATURE [App::DocumentObjectGroupPython] C_element068  label="C_element : 034"  # scripted group (container) (typed FeaturePython)
  n = 6
  ref = C_element
FEATURE [App::DocumentObjectGroupPython] H_element062  label="H_element : 031"  # scripted group (container) (typed FeaturePython)
  n = 5
  ref = H_element
FEATURE [App::DocumentObjectGroupPython] N_element029  label="N_element : 012"  # scripted group (container) (typed FeaturePython)
  n = 1
  ref = N_element
FEATURE [App::DocumentObjectGroupPython] O_element069  label="O_element : 034"  # scripted group (container) (typed FeaturePython)
  n = 2
  ref = O_element
FEATURE [App::DocumentObjectGroupPython] G4_NITROBENZENE  # scripted group (container) (typed FeaturePython)
  Dunit = g/cm3
  Dvalue = 1.19867
  Group = -> [C_element068,H_element062,N_element029,O_element069]
  conduct = 2
  density = 1
  expand = 3
  formula = G4_NITROBENZENE
  name = G4_NITROBENZENE
  specific = 4
FEATURE [App::DocumentObjectGroupPython] N_element030  label="N_element : 013"  # scripted group (container) (typed FeaturePython)
  n = 2
  ref = N_element
FEATURE [App::DocumentObjectGroupPython] O_element070  label="O_element : 035"  # scripted group (container) (typed FeaturePython)
  n = 1
  ref = O_element
FEATURE [App::DocumentObjectGroupPython] G4_NITROUS_OXIDE  # scripted group (container) (typed FeaturePython)
  Dunit = g/cm3
  Dvalue = 0.00183094
  Group = -> [N_element030,O_element070]
  conduct = 2
  density = 1
  expand = 3
  formula = G4_NITROUS_OXIDE
  name = G4_NITROUS_OXIDE
  specific = 4
FEATURE [App::DocumentObjectGroupPython] H_element063  label="H_element : 0.104"  # scripted group (container) (typed FeaturePython)
  n = 0.103509
FEATURE [App::DocumentObjectGroupPython] C_element069  label="C_element : 0.648"  # scripted group (container) (typed FeaturePython)
  n = 0.648416
FEATURE [App::DocumentObjectGroupPython] N_element031  label="N_element : 0.100"  # scripted group (container) (typed FeaturePython)
  n = 0.0995361
FEATURE [App::DocumentObjectGroupPython] O_element071  label="O_element : 0.149"  # scripted group (container) (typed FeaturePython)
  n = 0.148539
FEATURE [App::DocumentObjectGroupPython] G4_NYLON_8062  label="G4_NYLON-8062"  # scripted group (container) (typed FeaturePython)
  Dunit = g/cm3
  Dvalue = 1.08
  Group = -> [H_element063,C_element069,N_element031,O_element071]
  conduct = 2
  density = 1
  expand = 3
  formula = G4_NYLON-8062
  name = G4_NYLON-8062
  specific = 4
FEATURE [App::DocumentObjectGroupPython] C_element070  label="C_element : 035"  # scripted group (container) (typed FeaturePython)
  n = 6
  ref = C_element
FEATURE [App::DocumentObjectGroupPython] H_element064  label="H_element : 11"  # scripted group (container) (typed FeaturePython)
  n = 11
  ref = H_element
FEATURE [App::DocumentObjectGroupPython] N_element032  label="N_element : 014"  # scripted group (container) (typed FeaturePython)
  n = 1
  ref = N_element
FEATURE [App::DocumentObjectGroupPython] O_element072  label="O_element : 036"  # scripted group (container) (typed FeaturePython)
  n = 1
  ref = O_element
FEATURE [App::DocumentObjectGroupPython] G4_NYLON_6_6  label="G4_NYLON-6-6"  # scripted group (container) (typed FeaturePython)
  Dunit = g/cm3
  Dvalue = 1.14
  Group = -> [C_element070,H_element064,N_element032,O_element072]
  conduct = 2
  density = 1
  expand = 3
  formula = G4_NYLON-6-6
  name = G4_NYLON-6-6
  specific = 4
FEATURE [App::DocumentObjectGroupPython] H_element065  label="H_element : 0.139"  # scripted group (container) (typed FeaturePython)
  n = 0.107062
FEATURE [App::DocumentObjectGroupPython] C_element071  label="C_element : 0.680"  # scripted group (container) (typed FeaturePython)
  n = 0.680449
FEATURE [App::DocumentObjectGroupPython] N_element033  label="N_element : 0.099"  # scripted group (container) (typed FeaturePython)
  n = 0.099189
FEATURE [App::DocumentObjectGroupPython] O_element073  label="O_element : 0.113"  # scripted group (container) (typed FeaturePython)
  n = 0.1133
FEATURE [App::DocumentObjectGroupPython] G4_NYLON_6_10  label="G4_NYLON-6-10"  # scripted group (container) (typed FeaturePython)
  Dunit = g/cm3
  Dvalue = 1.14
  Group = -> [H_element065,C_element071,N_element033,O_element073]
  conduct = 2
  density = 1
  expand = 3
  formula = G4_NYLON-6-10
  name = G4_NYLON-6-10
  specific = 4
FEATURE [App::DocumentObjectGroupPython] H_element066  label="H_element : 0.140"  # scripted group (container) (typed FeaturePython)
  n = 0.115476
FEATURE [App::DocumentObjectGroupPython] C_element072  label="C_element : 0.721"  # scripted group (container) (typed FeaturePython)
  n = 0.720818
FEATURE [App::DocumentObjectGroupPython] N_element034  label="N_element : 0.076"  # scripted group (container) (typed FeaturePython)
  n = 0.0764169
FEATURE [App::DocumentObjectGroupPython] O_element074  label="O_element : 0.087"  # scripted group (container) (typed FeaturePython)
  n = 0.0872889
FEATURE [App::DocumentObjectGroupPython] G4_NYLON_11_RILSAN  label="G4_NYLON-11_RILSAN"  # scripted group (container) (typed FeaturePython)
  Dunit = g/cm3
  Dvalue = 1.425
  Group = -> [H_element066,C_element072,N_element034,O_element074]
  conduct = 2
  density = 1
  expand = 3
  formula = G4_NYLON-11_RILSAN
  name = G4_NYLON-11_RILSAN
  specific = 4
FEATURE [App::DocumentObjectGroupPython] C_element073  label="C_element : 8"  # scripted group (container) (typed FeaturePython)
  n = 8
  ref = C_element
FEATURE [App::DocumentObjectGroupPython] H_element067  label="H_element : 18"  # scripted group (container) (typed FeaturePython)
  n = 18
  ref = H_element
FEATURE [App::DocumentObjectGroupPython] G4_OCTANE  # scripted group (container) (typed FeaturePython)
  Dunit = g/cm3
  Dvalue = 0.7026
  Group = -> [C_element073,H_element067]
  conduct = 2
  density = 1
  expand = 3
  formula = G4_OCTANE
  name = G4_OCTANE
  specific = 4
FEATURE [App::DocumentObjectGroupPython] C_element074  label="C_element : 25"  # scripted group (container) (typed FeaturePython)
  n = 25
  ref = C_element
FEATURE [App::DocumentObjectGroupPython] H_element068  label="H_element : 52"  # scripted group (container) (typed FeaturePython)
  n = 52
  ref = H_element
FEATURE [App::DocumentObjectGroupPython] G4_PARAFFIN  # scripted group (container) (typed FeaturePython)
  Dunit = g/cm3
  Dvalue = 0.93
  Group = -> [C_element074,H_element068]
  conduct = 2
  density = 1
  expand = 3
  formula = G4_PARAFFIN
  name = G4_PARAFFIN
  specific = 4
FEATURE [App::DocumentObjectGroupPython] C_element075  label="C_element : 036"  # scripted group (container) (typed FeaturePython)
  n = 5
  ref = C_element
FEATURE [App::DocumentObjectGroupPython] H_element069  label="H_element : 032"  # scripted group (container) (typed FeaturePython)
  n = 12
  ref = H_element
FEATURE [App::DocumentObjectGroupPython] G4_N_PENTANE  label="G4_N-PENTANE"  # scripted group (container) (typed FeaturePython)
  Dunit = g/cm3
  Dvalue = 0.6262
  Group = -> [C_element075,H_element069]
  conduct = 2
  density = 1
  expand = 3
  formula = G4_N-PENTANE
  name = G4_N-PENTANE
  specific = 4
FEATURE [App::DocumentObjectGroupPython] H_element070  label="H_element : 0.014"  # scripted group (container) (typed FeaturePython)
  n = 0.0141
FEATURE [App::DocumentObjectGroupPython] C_element076  label="C_element : 0.072"  # scripted group (container) (typed FeaturePython)
  n = 0.072261
FEATURE [App::DocumentObjectGroupPython] N_element035  label="N_element : 0.019"  # scripted group (container) (typed FeaturePython)
  n = 0.01932
FEATURE [App::DocumentObjectGroupPython] O_element075  label="O_element : 0.066"  # scripted group (container) (typed FeaturePython)
  n = 0.066101
FEATURE [App::DocumentObjectGroupPython] S_element019  label="S_element : 0.020"  # scripted group (container) (typed FeaturePython)
  n = 0.00189
FEATURE [App::DocumentObjectGroupPython] Br_element004  label="Br_element : 0.349"  # scripted group (container) (typed FeaturePython)
  n = 0.349103
FEATURE [App::DocumentObjectGroupPython] Ag_element001  label="Ag_element : 0.474"  # scripted group (container) (typed FeaturePython)
  n = 0.474105
FEATURE [App::DocumentObjectGroupPython] I_element005  label="I_element : 0.003"  # scripted group (container) (typed FeaturePython)
  n = 0.00312
FEATURE [App::DocumentObjectGroupPython] G4_PHOTO_EMULSION  # scripted group (container) (typed FeaturePython)
  Dunit = g/cm3
  Dvalue = 3.815
  Group = -> [H_element070,C_element076,N_element035,O_element075,S_element019,Br_element004,Ag_element001,I_element005]
  conduct = 2
  density = 1
  expand = 3
  formula = G4_PHOTO_EMULSION
  name = G4_PHOTO_EMULSION
  specific = 4
FEATURE [App::DocumentObjectGroupPython] C_element077  label="C_element : 9"  # scripted group (container) (typed FeaturePython)
  n = 9
  ref = C_element
FEATURE [App::DocumentObjectGroupPython] H_element071  label="H_element : 033"  # scripted group (container) (typed FeaturePython)
  n = 10
  ref = H_element
FEATURE [App::DocumentObjectGroupPython] G4_PLASTIC_SC_VINYLTOLUENE  # scripted group (container) (typed FeaturePython)
  Dunit = g/cm3
  Dvalue = 1.032
  Group = -> [C_element077,H_element071]
  conduct = 2
  density = 1
  expand = 3
  formula = G4_PLASTIC_SC_VINYLTOLUENE
  name = G4_PLASTIC_SC_VINYLTOLUENE
  specific = 4
FEATURE [App::DocumentObjectGroupPython] Pu_element001  label="Pu_element : 1"  # scripted group (container) (typed FeaturePython)
  n = 1
  ref = Pu_element
FEATURE [App::DocumentObjectGroupPython] O_element076  label="O_element : 037"  # scripted group (container) (typed FeaturePython)
  n = 2
  ref = O_element
FEATURE [App::DocumentObjectGroupPython] G4_PLUTONIUM_DIOXIDE  # scripted group (container) (typed FeaturePython)
  Dunit = g/cm3
  Dvalue = 11.46
  Group = -> [Pu_element001,O_element076]
  conduct = 2
  density = 1
  expand = 3
  formula = G4_PLUTONIUM_DIOXIDE
  name = G4_PLUTONIUM_DIOXIDE
  specific = 4
FEATURE [App::DocumentObjectGroupPython] C_element078  label="C_element : 037"  # scripted group (container) (typed FeaturePython)
  n = 3
  ref = C_element
FEATURE [App::DocumentObjectGroupPython] H_element072  label="H_element : 034"  # scripted group (container) (typed FeaturePython)
  n = 3
  ref = H_element
FEATURE [App::DocumentObjectGroupPython] N_element036  label="N_element : 015"  # scripted group (container) (typed FeaturePython)
  n = 1
  ref = N_element
FEATURE [App::DocumentObjectGroupPython] G4_POLYACRYLONITRILE  # scripted group (container) (typed FeaturePython)
  Dunit = g/cm3
  Dvalue = 1.17
  Group = -> [C_element078,H_element072,N_element036]
  conduct = 2
  density = 1
  expand = 3
  formula = G4_POLYACRYLONITRILE
  name = G4_POLYACRYLONITRILE
  specific = 4
FEATURE [App::DocumentObjectGroupPython] C_element079  label="C_element : 16"  # scripted group (container) (typed FeaturePython)
  n = 16
  ref = C_element
FEATURE [App::DocumentObjectGroupPython] H_element073  label="H_element : 035"  # scripted group (container) (typed FeaturePython)
  n = 14
  ref = H_element
FEATURE [App::DocumentObjectGroupPython] O_element077  label="O_element : 038"  # scripted group (container) (typed FeaturePython)
  n = 3
  ref = O_element
FEATURE [App::DocumentObjectGroupPython] G4_POLYCARBONATE  # scripted group (container) (typed FeaturePython)
  Dunit = g/cm3
  Dvalue = 1.2
  Group = -> [C_element079,H_element073,O_element077]
  conduct = 2
  density = 1
  expand = 3
  formula = G4_POLYCARBONATE
  name = G4_POLYCARBONATE
  specific = 4
FEATURE [App::DocumentObjectGroupPython] C_element080  label="C_element : 038"  # scripted group (container) (typed FeaturePython)
  n = 8
  ref = C_element
FEATURE [App::DocumentObjectGroupPython] H_element074  label="H_element : 036"  # scripted group (container) (typed FeaturePython)
  n = 7
  ref = H_element
FEATURE [App::DocumentObjectGroupPython] Cl_element017  label="Cl_element : 007"  # scripted group (container) (typed FeaturePython)
  n = 1
  ref = Cl_element
FEATURE [App::DocumentObjectGroupPython] G4_POLYCHLOROSTYRENE  # scripted group (container) (typed FeaturePython)
  Dunit = g/cm3
  Dvalue = 1.3
  Group = -> [C_element080,H_element074,Cl_element017]
  conduct = 2
  density = 1
  expand = 3
  formula = G4_POLYCHLOROSTYRENE
  name = G4_POLYCHLOROSTYRENE
  specific = 4
FEATURE [App::DocumentObjectGroupPython] C_element081  label="C_element : 039"  # scripted group (container) (typed FeaturePython)
  n = 1
  ref = C_element
FEATURE [App::DocumentObjectGroupPython] H_element075  label="H_element : 037"  # scripted group (container) (typed FeaturePython)
  n = 2
  ref = H_element
FEATURE [App::DocumentObjectGroupPython] G4_POLYETHYLENE  # scripted group (container) (typed FeaturePython)
  Dunit = g/cm3
  Dvalue = 0.94
  Group = -> [C_element081,H_element075]
  conduct = 2
  density = 1
  expand = 3
  formula = G4_POLYETHYLENE
  name = G4_POLYETHYLENE
  specific = 4
FEATURE [App::DocumentObjectGroupPython] C_element082  label="C_element : 040"  # scripted group (container) (typed FeaturePython)
  n = 10
  ref = C_element
FEATURE [App::DocumentObjectGroupPython] H_element076  label="H_element : 038"  # scripted group (container) (typed FeaturePython)
  n = 8
  ref = H_element
FEATURE [App::DocumentObjectGroupPython] O_element078  label="O_element : 039"  # scripted group (container) (typed FeaturePython)
  n = 4
  ref = O_element
FEATURE [App::DocumentObjectGroupPython] G4_MYLAR  # scripted group (container) (typed FeaturePython)
  Dunit = g/cm3
  Dvalue = 1.4
  Group = -> [C_element082,H_element076,O_element078]
  conduct = 2
  density = 1
  expand = 3
  formula = G4_MYLAR
  name = G4_MYLAR
  specific = 4
FEATURE [App::DocumentObjectGroupPython] C_element083  label="C_element : 041"  # scripted group (container) (typed FeaturePython)
  n = 5
  ref = C_element
FEATURE [App::DocumentObjectGroupPython] H_element077  label="H_element : 039"  # scripted group (container) (typed FeaturePython)
  n = 8
  ref = H_element
FEATURE [App::DocumentObjectGroupPython] O_element079  label="O_element : 040"  # scripted group (container) (typed FeaturePython)
  n = 2
  ref = O_element
FEATURE [App::DocumentObjectGroupPython] G4_PLEXIGLASS  # scripted group (container) (typed FeaturePython)
  Dunit = g/cm3
  Dvalue = 1.19
  Group = -> [C_element083,H_element077,O_element079]
  conduct = 2
  density = 1
  expand = 3
  formula = G4_PLEXIGLASS
  name = G4_PLEXIGLASS
  specific = 4
FEATURE [App::DocumentObjectGroupPython] C_element084  label="C_element : 042"  # scripted group (container) (typed FeaturePython)
  n = 1
  ref = C_element
FEATURE [App::DocumentObjectGroupPython] H_element078  label="H_element : 040"  # scripted group (container) (typed FeaturePython)
  n = 2
  ref = H_element
FEATURE [App::DocumentObjectGroupPython] O_element080  label="O_element : 041"  # scripted group (container) (typed FeaturePython)
  n = 1
  ref = O_element
FEATURE [App::DocumentObjectGroupPython] G4_POLYOXYMETHYLENE  # scripted group (container) (typed FeaturePython)
  Dunit = g/cm3
  Dvalue = 1.425
  Group = -> [C_element084,H_element078,O_element080]
  conduct = 2
  density = 1
  expand = 3
  formula = G4_POLYOXYMETHYLENE
  name = G4_POLYOXYMETHYLENE
  specific = 4
FEATURE [App::DocumentObjectGroupPython] C_element085  label="C_element : 043"  # scripted group (container) (typed FeaturePython)
  n = 2
  ref = C_element
FEATURE [App::DocumentObjectGroupPython] H_element079  label="H_element : 041"  # scripted group (container) (typed FeaturePython)
  n = 4
  ref = H_element
FEATURE [App::DocumentObjectGroupPython] G4_POLYPROPYLENE  # scripted group (container) (typed FeaturePython)
  Dunit = g/cm3
  Dvalue = 0.9
  Group = -> [C_element085,H_element079]
  conduct = 2
  density = 1
  expand = 3
  formula = G4_POLYPROPYLENE
  name = G4_POLYPROPYLENE
  specific = 4
FEATURE [App::DocumentObjectGroupPython] C_element086  label="C_element : 044"  # scripted group (container) (typed FeaturePython)
  n = 8
  ref = C_element
FEATURE [App::DocumentObjectGroupPython] H_element080  label="H_element : 042"  # scripted group (container) (typed FeaturePython)
  n = 8
  ref = H_element
FEATURE [App::DocumentObjectGroupPython] G4_POLYSTYRENE  # scripted group (container) (typed FeaturePython)
  Dunit = g/cm3
  Dvalue = 1.06
  Group = -> [C_element086,H_element080]
  conduct = 2
  density = 1
  expand = 3
  formula = G4_POLYSTYRENE
  name = G4_POLYSTYRENE
  specific = 4
FEATURE [App::DocumentObjectGroupPython] C_element087  label="C_element : 045"  # scripted group (container) (typed FeaturePython)
  n = 2
  ref = C_element
FEATURE [App::DocumentObjectGroupPython] F_element014  label="F_element : 4"  # scripted group (container) (typed FeaturePython)
  n = 4
  ref = F_element
FEATURE [App::DocumentObjectGroupPython] G4_TEFLON  # scripted group (container) (typed FeaturePython)
  Dunit = g/cm3
  Dvalue = 2.2
  Group = -> [C_element087,F_element014]
  conduct = 2
  density = 1
  expand = 3
  formula = G4_TEFLON
  name = G4_TEFLON
  specific = 4
FEATURE [App::DocumentObjectGroupPython] C_element088  label="C_element : 046"  # scripted group (container) (typed FeaturePython)
  n = 2
  ref = C_element
FEATURE [App::DocumentObjectGroupPython] F_element015  label="F_element : 006"  # scripted group (container) (typed FeaturePython)
  n = 3
  ref = F_element
FEATURE [App::DocumentObjectGroupPython] Cl_element018  label="Cl_element : 008"  # scripted group (container) (typed FeaturePython)
  n = 1
  ref = Cl_element
FEATURE [App::DocumentObjectGroupPython] G4_POLYTRIFLUOROCHLOROETHYLENE  # scripted group (container) (typed FeaturePython)
  Dunit = g/cm3
  Dvalue = 2.1
  Group = -> [C_element088,F_element015,Cl_element018]
  conduct = 2
  density = 1
  expand = 3
  formula = G4_POLYTRIFLUOROCHLOROETHYLENE
  name = G4_POLYTRIFLUOROCHLOROETHYLENE
  specific = 4
FEATURE [App::DocumentObjectGroupPython] C_element089  label="C_element : 047"  # scripted group (container) (typed FeaturePython)
  n = 4
  ref = C_element
FEATURE [App::DocumentObjectGroupPython] H_element081  label="H_element : 043"  # scripted group (container) (typed FeaturePython)
  n = 6
  ref = H_element
FEATURE [App::DocumentObjectGroupPython] O_element081  label="O_element : 042"  # scripted group (container) (typed FeaturePython)
  n = 2
  ref = O_element
FEATURE [App::DocumentObjectGroupPython] G4_POLYVINYL_ACETATE  # scripted group (container) (typed FeaturePython)
  Dunit = g/cm3
  Dvalue = 1.19
  Group = -> [C_element089,H_element081,O_element081]
  conduct = 2
  density = 1
  expand = 3
  formula = G4_POLYVINYL_ACETATE
  name = G4_POLYVINYL_ACETATE
  specific = 4
FEATURE [App::DocumentObjectGroupPython] C_element090  label="C_element : 048"  # scripted group (container) (typed FeaturePython)
  n = 2
  ref = C_element
FEATURE [App::DocumentObjectGroupPython] H_element082  label="H_element : 044"  # scripted group (container) (typed FeaturePython)
  n = 4
  ref = H_element
FEATURE [App::DocumentObjectGroupPython] O_element082  label="O_element : 043"  # scripted group (container) (typed FeaturePython)
  n = 1
  ref = O_element
FEATURE [App::DocumentObjectGroupPython] G4_POLYVINYL_ALCOHOL  # scripted group (container) (typed FeaturePython)
  Dunit = g/cm3
  Dvalue = 1.3
  Group = -> [C_element090,H_element082,O_element082]
  conduct = 2
  density = 1
  expand = 3
  formula = G4_POLYVINYL_ALCOHOL
  name = G4_POLYVINYL_ALCOHOL
  specific = 4
FEATURE [App::DocumentObjectGroupPython] C_element091  label="C_element : 049"  # scripted group (container) (typed FeaturePython)
  n = 8
  ref = C_element
FEATURE [App::DocumentObjectGroupPython] H_element083  label="H_element : 045"  # scripted group (container) (typed FeaturePython)
  n = 14
  ref = H_element
FEATURE [App::DocumentObjectGroupPython] O_element083  label="O_element : 044"  # scripted group (container) (typed FeaturePython)
  n = 2
  ref = O_element
FEATURE [App::DocumentObjectGroupPython] G4_POLYVINYL_BUTYRAL  # scripted group (container) (typed FeaturePython)
  Dunit = g/cm3
  Dvalue = 1.12
  Group = -> [C_element091,H_element083,O_element083]
  conduct = 2
  density = 1
  expand = 3
  formula = G4_POLYVINYL_BUTYRAL
  name = G4_POLYVINYL_BUTYRAL
  specific = 4
FEATURE [App::DocumentObjectGroupPython] C_element092  label="C_element : 050"  # scripted group (container) (typed FeaturePython)
  n = 2
  ref = C_element
FEATURE [App::DocumentObjectGroupPython] H_element084  label="H_element : 046"  # scripted group (container) (typed FeaturePython)
  n = 3
  ref = H_element
FEATURE [App::DocumentObjectGroupPython] Cl_element019  label="Cl_element : 009"  # scripted group (container) (typed FeaturePython)
  n = 1
  ref = Cl_element
FEATURE [App::DocumentObjectGroupPython] G4_POLYVINYL_CHLORIDE  # scripted group (container) (typed FeaturePython)
  Dunit = g/cm3
  Dvalue = 1.3
  Group = -> [C_element092,H_element084,Cl_element019]
  conduct = 2
  density = 1
  expand = 3
  formula = G4_POLYVINYL_CHLORIDE
  name = G4_POLYVINYL_CHLORIDE
  specific = 4
FEATURE [App::DocumentObjectGroupPython] C_element093  label="C_element : 051"  # scripted group (container) (typed FeaturePython)
  n = 2
  ref = C_element
FEATURE [App::DocumentObjectGroupPython] H_element085  label="H_element : 047"  # scripted group (container) (typed FeaturePython)
  n = 2
  ref = H_element
FEATURE [App::DocumentObjectGroupPython] Cl_element020  label="Cl_element : 010"  # scripted group (container) (typed FeaturePython)
  n = 2
  ref = Cl_element
FEATURE [App::DocumentObjectGroupPython] G4_POLYVINYLIDENE_CHLORIDE  # scripted group (container) (typed FeaturePython)
  Dunit = g/cm3
  Dvalue = 1.7
  Group = -> [C_element093,H_element085,Cl_element020]
  conduct = 2
  density = 1
  expand = 3
  formula = G4_POLYVINYLIDENE_CHLORIDE
  name = G4_POLYVINYLIDENE_CHLORIDE
  specific = 4
FEATURE [App::DocumentObjectGroupPython] C_element094  label="C_element : 052"  # scripted group (container) (typed FeaturePython)
  n = 2
  ref = C_element
FEATURE [App::DocumentObjectGroupPython] H_element086  label="H_element : 048"  # scripted group (container) (typed FeaturePython)
  n = 2
  ref = H_element
FEATURE [App::DocumentObjectGroupPython] F_element016  label="F_element : 007"  # scripted group (container) (typed FeaturePython)
  n = 2
  ref = F_element
FEATURE [App::DocumentObjectGroupPython] G4_POLYVINYLIDENE_FLUORIDE  # scripted group (container) (typed FeaturePython)
  Dunit = g/cm3
  Dvalue = 1.76
  Group = -> [C_element094,H_element086,F_element016]
  conduct = 2
  density = 1
  expand = 3
  formula = G4_POLYVINYLIDENE_FLUORIDE
  name = G4_POLYVINYLIDENE_FLUORIDE
  specific = 4
FEATURE [App::DocumentObjectGroupPython] C_element095  label="C_element : 053"  # scripted group (container) (typed FeaturePython)
  n = 6
  ref = C_element
FEATURE [App::DocumentObjectGroupPython] H_element087  label="H_element : 9"  # scripted group (container) (typed FeaturePython)
  n = 9
  ref = H_element
FEATURE [App::DocumentObjectGroupPython] N_element037  label="N_element : 016"  # scripted group (container) (typed FeaturePython)
  n = 1
  ref = N_element
FEATURE [App::DocumentObjectGroupPython] O_element084  label="O_element : 045"  # scripted group (container) (typed FeaturePython)
  n = 1
  ref = O_element
FEATURE [App::DocumentObjectGroupPython] G4_POLYVINYL_PYRROLIDONE  # scripted group (container) (typed FeaturePython)
  Dunit = g/cm3
  Dvalue = 1.25
  Group = -> [C_element095,H_element087,N_element037,O_element084]
  conduct = 2
  density = 1
  expand = 3
  formula = G4_POLYVINYL_PYRROLIDONE
  name = G4_POLYVINYL_PYRROLIDONE
  specific = 4
FEATURE [App::DocumentObjectGroupPython] K_element008  label="K_element : 1"  # scripted group (container) (typed FeaturePython)
  n = 1
  ref = K_element
FEATURE [App::DocumentObjectGroupPython] I_element006  label="I_element : 003"  # scripted group (container) (typed FeaturePython)
  n = 1
  ref = I_element
FEATURE [App::DocumentObjectGroupPython] G4_POTASSIUM_IODIDE  # scripted group (container) (typed FeaturePython)
  Dunit = g/cm3
  Dvalue = 3.13
  Group = -> [K_element008,I_element006]
  conduct = 2
  density = 1
  expand = 3
  formula = G4_POTASSIUM_IODIDE
  name = G4_POTASSIUM_IODIDE
  specific = 4
FEATURE [App::DocumentObjectGroupPython] K_element009  label="K_element : 2"  # scripted group (container) (typed FeaturePython)
  n = 2
  ref = K_element
FEATURE [App::DocumentObjectGroupPython] O_element085  label="O_element : 046"  # scripted group (container) (typed FeaturePython)
  n = 1
  ref = O_element
FEATURE [App::DocumentObjectGroupPython] G4_POTASSIUM_OXIDE  # scripted group (container) (typed FeaturePython)
  Dunit = g/cm3
  Dvalue = 2.32
  Group = -> [K_element009,O_element085]
  conduct = 2
  density = 1
  expand = 3
  formula = G4_POTASSIUM_OXIDE
  name = G4_POTASSIUM_OXIDE
  specific = 4
FEATURE [App::DocumentObjectGroupPython] C_element096  label="C_element : 054"  # scripted group (container) (typed FeaturePython)
  n = 3
  ref = C_element
FEATURE [App::DocumentObjectGroupPython] H_element088  label="H_element : 049"  # scripted group (container) (typed FeaturePython)
  n = 8
  ref = H_element
FEATURE [App::DocumentObjectGroupPython] G4_PROPANE  # scripted group (container) (typed FeaturePython)
  Dunit = g/cm3
  Dvalue = 0.00187939
  Group = -> [C_element096,H_element088]
  conduct = 2
  density = 1
  expand = 3
  formula = G4_PROPANE
  name = G4_PROPANE
  specific = 4
FEATURE [App::DocumentObjectGroupPython] C_element097  label="C_element : 055"  # scripted group (container) (typed FeaturePython)
  n = 3
  ref = C_element
FEATURE [App::DocumentObjectGroupPython] H_element089  label="H_element : 050"  # scripted group (container) (typed FeaturePython)
  n = 8
  ref = H_element
FEATURE [App::DocumentObjectGroupPython] G4_lPROPANE  # scripted group (container) (typed FeaturePython)
  Dunit = g/cm3
  Dvalue = 0.43
  Group = -> [C_element097,H_element089]
  conduct = 2
  density = 1
  expand = 3
  formula = G4_lPROPANE
  name = G4_lPROPANE
  specific = 4
FEATURE [App::DocumentObjectGroupPython] C_element098  label="C_element : 056"  # scripted group (container) (typed FeaturePython)
  n = 3
  ref = C_element
FEATURE [App::DocumentObjectGroupPython] H_element090  label="H_element : 051"  # scripted group (container) (typed FeaturePython)
  n = 8
  ref = H_element
FEATURE [App::DocumentObjectGroupPython] O_element086  label="O_element : 047"  # scripted group (container) (typed FeaturePython)
  n = 1
  ref = O_element
FEATURE [App::DocumentObjectGroupPython] G4_N_PROPYL_ALCOHOL  label="G4_N-PROPYL_ALCOHOL"  # scripted group (container) (typed FeaturePython)
  Dunit = g/cm3
  Dvalue = 0.8035
  Group = -> [C_element098,H_element090,O_element086]
  conduct = 2
  density = 1
  expand = 3
  formula = G4_N-PROPYL_ALCOHOL
  name = G4_N-PROPYL_ALCOHOL
  specific = 4
FEATURE [App::DocumentObjectGroupPython] C_element099  label="C_element : 057"  # scripted group (container) (typed FeaturePython)
  n = 5
  ref = C_element
FEATURE [App::DocumentObjectGroupPython] H_element091  label="H_element : 052"  # scripted group (container) (typed FeaturePython)
  n = 5
  ref = H_element
FEATURE [App::DocumentObjectGroupPython] N_element038  label="N_element : 017"  # scripted group (container) (typed FeaturePython)
  n = 1
  ref = N_element
FEATURE [App::DocumentObjectGroupPython] G4_PYRIDINE  # scripted group (container) (typed FeaturePython)
  Dunit = g/cm3
  Dvalue = 0.9819
  Group = -> [C_element099,H_element091,N_element038]
  conduct = 2
  density = 1
  expand = 3
  formula = G4_PYRIDINE
  name = G4_PYRIDINE
  specific = 4
FEATURE [App::DocumentObjectGroupPython] H_element092  label="H_element : 0.144"  # scripted group (container) (typed FeaturePython)
  n = 0.143711
FEATURE [App::DocumentObjectGroupPython] C_element100  label="C_element : 0.856"  # scripted group (container) (typed FeaturePython)
  n = 0.856289
FEATURE [App::DocumentObjectGroupPython] G4_RUBBER_BUTYL  # scripted group (container) (typed FeaturePython)
  Dunit = g/cm3
  Dvalue = 0.92
  Group = -> [H_element092,C_element100]
  conduct = 2
  density = 1
  expand = 3
  formula = G4_RUBBER_BUTYL
  name = G4_RUBBER_BUTYL
  specific = 4
FEATURE [App::DocumentObjectGroupPython] H_element093  label="H_element : 0.118"  # scripted group (container) (typed FeaturePython)
  n = 0.118371
FEATURE [App::DocumentObjectGroupPython] C_element101  label="C_element : 0.882"  # scripted group (container) (typed FeaturePython)
  n = 0.881629
FEATURE [App::DocumentObjectGroupPython] G4_RUBBER_NATURAL  # scripted group (container) (typed FeaturePython)
  Dunit = g/cm3
  Dvalue = 0.92
  Group = -> [H_element093,C_element101]
  conduct = 2
  density = 1
  expand = 3
  formula = G4_RUBBER_NATURAL
  name = G4_RUBBER_NATURAL
  specific = 4
FEATURE [App::DocumentObjectGroupPython] H_element094  label="H_element : 0.145"  # scripted group (container) (typed FeaturePython)
  n = 0.05692
FEATURE [App::DocumentObjectGroupPython] C_element102  label="C_element : 0.543"  # scripted group (container) (typed FeaturePython)
  n = 0.542646
FEATURE [App::DocumentObjectGroupPython] Cl_element021  label="Cl_element : 0.400"  # scripted group (container) (typed FeaturePython)
  n = 0.400434
FEATURE [App::DocumentObjectGroupPython] G4_RUBBER_NEOPRENE  # scripted group (container) (typed FeaturePython)
  Dunit = g/cm3
  Dvalue = 1.23
  Group = -> [H_element094,C_element102,Cl_element021]
  conduct = 2
  density = 1
  expand = 3
  formula = G4_RUBBER_NEOPRENE
  name = G4_RUBBER_NEOPRENE
  specific = 4
FEATURE [App::DocumentObjectGroupPython] Si_element006  label="Si_element : 1"  # scripted group (container) (typed FeaturePython)
  n = 1
  ref = Si_element
FEATURE [App::DocumentObjectGroupPython] O_element087  label="O_element : 048"  # scripted group (container) (typed FeaturePython)
  n = 2
  ref = O_element
FEATURE [App::DocumentObjectGroupPython] G4_SILICON_DIOXIDE  # scripted group (container) (typed FeaturePython)
  Dunit = g/cm3
  Dvalue = 2.32
  Group = -> [Si_element006,O_element087]
  conduct = 2
  density = 1
  expand = 3
  formula = G4_SILICON_DIOXIDE
  name = G4_SILICON_DIOXIDE
  specific = 4
FEATURE [App::DocumentObjectGroupPython] Ag_element002  label="Ag_element : 1"  # scripted group (container) (typed FeaturePython)
  n = 1
  ref = Ag_element
FEATURE [App::DocumentObjectGroupPython] Br_element005  label="Br_element : 003"  # scripted group (container) (typed FeaturePython)
  n = 1
  ref = Br_element
FEATURE [App::DocumentObjectGroupPython] G4_SILVER_BROMIDE  # scripted group (container) (typed FeaturePython)
  Dunit = g/cm3
  Dvalue = 6.473
  Group = -> [Ag_element002,Br_element005]
  conduct = 2
  density = 1
  expand = 3
  formula = G4_SILVER_BROMIDE
  name = G4_SILVER_BROMIDE
  specific = 4
FEATURE [App::DocumentObjectGroupPython] Ag_element003  label="Ag_element : 002"  # scripted group (container) (typed FeaturePython)
  n = 1
  ref = Ag_element
FEATURE [App::DocumentObjectGroupPython] Cl_element022  label="Cl_element : 011"  # scripted group (container) (typed FeaturePython)
  n = 1
  ref = Cl_element
FEATURE [App::DocumentObjectGroupPython] G4_SILVER_CHLORIDE  # scripted group (container) (typed FeaturePython)
  Dunit = g/cm3
  Dvalue = 5.56
  Group = -> [Ag_element003,Cl_element022]
  conduct = 2
  density = 1
  expand = 3
  formula = G4_SILVER_CHLORIDE
  name = G4_SILVER_CHLORIDE
  specific = 4
FEATURE [App::DocumentObjectGroupPython] Br_element006  label="Br_element : 0.423"  # scripted group (container) (typed FeaturePython)
  n = 0.422895
FEATURE [App::DocumentObjectGroupPython] Ag_element004  label="Ag_element : 0.574"  # scripted group (container) (typed FeaturePython)
  n = 0.573748
FEATURE [App::DocumentObjectGroupPython] I_element007  label="I_element : 0.649"  # scripted group (container) (typed FeaturePython)
  n = 0.003357
FEATURE [App::DocumentObjectGroupPython] G4_SILVER_HALIDES  # scripted group (container) (typed FeaturePython)
  Dunit = g/cm3
  Dvalue = 6.47
  Group = -> [Br_element006,Ag_element004,I_element007]
  conduct = 2
  density = 1
  expand = 3
  formula = G4_SILVER_HALIDES
  name = G4_SILVER_HALIDES
  specific = 4
FEATURE [App::DocumentObjectGroupPython] Ag_element005  label="Ag_element : 003"  # scripted group (container) (typed FeaturePython)
  n = 1
  ref = Ag_element
FEATURE [App::DocumentObjectGroupPython] I_element008  label="I_element : 004"  # scripted group (container) (typed FeaturePython)
  n = 1
  ref = I_element
FEATURE [App::DocumentObjectGroupPython] G4_SILVER_IODIDE  # scripted group (container) (typed FeaturePython)
  Dunit = g/cm3
  Dvalue = 6.01
  Group = -> [Ag_element005,I_element008]
  conduct = 2
  density = 1
  expand = 3
  formula = G4_SILVER_IODIDE
  name = G4_SILVER_IODIDE
  specific = 4
FEATURE [App::DocumentObjectGroupPython] H_element095  label="H_element : 0.100"  # scripted group (container) (typed FeaturePython)
  n = 0.1
FEATURE [App::DocumentObjectGroupPython] C_element103  label="C_element : 0.204"  # scripted group (container) (typed FeaturePython)
  n = 0.204
FEATURE [App::DocumentObjectGroupPython] N_element039  label="N_element : 0.759"  # scripted group (container) (typed FeaturePython)
  n = 0.042
FEATURE [App::DocumentObjectGroupPython] O_element088  label="O_element : 0.645"  # scripted group (container) (typed FeaturePython)
  n = 0.645
FEATURE [App::DocumentObjectGroupPython] Na_element013  label="Na_element : 0.100"  # scripted group (container) (typed FeaturePython)
  n = 0.002
FEATURE [App::DocumentObjectGroupPython] P_element009  label="P_element : 0.107"  # scripted group (container) (typed FeaturePython)
  n = 0.001
FEATURE [App::DocumentObjectGroupPython] S_element020  label="S_element : 0.021"  # scripted group (container) (typed FeaturePython)
  n = 0.002
FEATURE [App::DocumentObjectGroupPython] Cl_element023  label="Cl_element : 0.590"  # scripted group (container) (typed FeaturePython)
  n = 0.003
FEATURE [App::DocumentObjectGroupPython] K_element010  label="K_element : 0.001"  # scripted group (container) (typed FeaturePython)
  n = 0.001
FEATURE [App::DocumentObjectGroupPython] G4_SKIN_ICRP  # scripted group (container) (typed FeaturePython)
  Dunit = g/cm3
  Dvalue = 1.09
  Group = -> [H_element095,C_element103,N_element039,O_element088,Na_element013,P_element009,S_element020,Cl_element023,K_element010]
  conduct = 2
  density = 1
  expand = 3
  formula = G4_SKIN_ICRP
  name = G4_SKIN_ICRP
  specific = 4
FEATURE [App::DocumentObjectGroupPython] Na_element014  label="Na_element : 2"  # scripted group (container) (typed FeaturePython)
  n = 2
  ref = Na_element
FEATURE [App::DocumentObjectGroupPython] C_element104  label="C_element : 058"  # scripted group (container) (typed FeaturePython)
  n = 1
  ref = C_element
FEATURE [App::DocumentObjectGroupPython] O_element089  label="O_element : 049"  # scripted group (container) (typed FeaturePython)
  n = 3
  ref = O_element
FEATURE [App::DocumentObjectGroupPython] G4_SODIUM_CARBONATE  # scripted group (container) (typed FeaturePython)
  Dunit = g/cm3
  Dvalue = 2.532
  Group = -> [Na_element014,C_element104,O_element089]
  conduct = 2
  density = 1
  expand = 3
  formula = G4_SODIUM_CARBONATE
  name = G4_SODIUM_CARBONATE
  specific = 4
FEATURE [App::DocumentObjectGroupPython] Na_element015  label="Na_element : 1"  # scripted group (container) (typed FeaturePython)
  n = 1
  ref = Na_element
FEATURE [App::DocumentObjectGroupPython] I_element009  label="I_element : 005"  # scripted group (container) (typed FeaturePython)
  n = 1
  ref = I_element
FEATURE [App::DocumentObjectGroupPython] G4_SODIUM_IODIDE  # scripted group (container) (typed FeaturePython)
  Dunit = g/cm3
  Dvalue = 3.667
  Group = -> [Na_element015,I_element009]
  conduct = 2
  density = 1
  expand = 3
  formula = G4_SODIUM_IODIDE
  name = G4_SODIUM_IODIDE
  specific = 4
FEATURE [App::DocumentObjectGroupPython] Na_element016  label="Na_element : 003"  # scripted group (container) (typed FeaturePython)
  n = 2
  ref = Na_element
FEATURE [App::DocumentObjectGroupPython] O_element090  label="O_element : 050"  # scripted group (container) (typed FeaturePython)
  n = 1
  ref = O_element
FEATURE [App::DocumentObjectGroupPython] G4_SODIUM_MONOXIDE  # scripted group (container) (typed FeaturePython)
  Dunit = g/cm3
  Dvalue = 2.27
  Group = -> [Na_element016,O_element090]
  conduct = 2
  density = 1
  expand = 3
  formula = G4_SODIUM_MONOXIDE
  name = G4_SODIUM_MONOXIDE
  specific = 4
FEATURE [App::DocumentObjectGroupPython] Na_element017  label="Na_element : 004"  # scripted group (container) (typed FeaturePython)
  n = 1
  ref = Na_element
FEATURE [App::DocumentObjectGroupPython] N_element040  label="N_element : 018"  # scripted group (container) (typed FeaturePython)
  n = 1
  ref = N_element
FEATURE [App::DocumentObjectGroupPython] O_element091  label="O_element : 051"  # scripted group (container) (typed FeaturePython)
  n = 3
  ref = O_element
FEATURE [App::DocumentObjectGroupPython] G4_SODIUM_NITRATE  # scripted group (container) (typed FeaturePython)
  Dunit = g/cm3
  Dvalue = 2.261
  Group = -> [Na_element017,N_element040,O_element091]
  conduct = 2
  density = 1
  expand = 3
  formula = G4_SODIUM_NITRATE
  name = G4_SODIUM_NITRATE
  specific = 4
FEATURE [App::DocumentObjectGroupPython] C_element105  label="C_element : 059"  # scripted group (container) (typed FeaturePython)
  n = 14
  ref = C_element
FEATURE [App::DocumentObjectGroupPython] H_element096  label="H_element : 053"  # scripted group (container) (typed FeaturePython)
  n = 12
  ref = H_element
FEATURE [App::DocumentObjectGroupPython] G4_STILBENE  # scripted group (container) (typed FeaturePython)
  Dunit = g/cm3
  Dvalue = 0.9707
  Group = -> [C_element105,H_element096]
  conduct = 2
  density = 1
  expand = 3
  formula = G4_STILBENE
  name = G4_STILBENE
  specific = 4
FEATURE [App::DocumentObjectGroupPython] C_element106  label="C_element : 12"  # scripted group (container) (typed FeaturePython)
  n = 12
  ref = C_element
FEATURE [App::DocumentObjectGroupPython] H_element097  label="H_element : 22"  # scripted group (container) (typed FeaturePython)
  n = 22
  ref = H_element
FEATURE [App::DocumentObjectGroupPython] O_element092  label="O_element : 11"  # scripted group (container) (typed FeaturePython)
  n = 11
  ref = O_element
FEATURE [App::DocumentObjectGroupPython] G4_SUCROSE  # scripted group (container) (typed FeaturePython)
  Dunit = g/cm3
  Dvalue = 1.5805
  Group = -> [C_element106,H_element097,O_element092]
  conduct = 2
  density = 1
  expand = 3
  formula = G4_SUCROSE
  name = G4_SUCROSE
  specific = 4
FEATURE [App::DocumentObjectGroupPython] C_element107  label="C_element : 18"  # scripted group (container) (typed FeaturePython)
  n = 18
  ref = C_element
FEATURE [App::DocumentObjectGroupPython] H_element098  label="H_element : 054"  # scripted group (container) (typed FeaturePython)
  n = 14
  ref = H_element
FEATURE [App::DocumentObjectGroupPython] G4_TERPHENYL  # scripted group (container) (typed FeaturePython)
  Dunit = g/cm3
  Dvalue = 1.24
  Group = -> [C_element107,H_element098]
  conduct = 2
  density = 1
  expand = 3
  formula = G4_TERPHENYL
  name = G4_TERPHENYL
  specific = 4
FEATURE [App::DocumentObjectGroupPython] H_element099  label="H_element : 0.146"  # scripted group (container) (typed FeaturePython)
  n = 0.106
FEATURE [App::DocumentObjectGroupPython] C_element108  label="C_element : 0.883"  # scripted group (container) (typed FeaturePython)
  n = 0.099
FEATURE [App::DocumentObjectGroupPython] N_element041  label="N_element : 0.020"  # scripted group (container) (typed FeaturePython)
  n = 0.02
FEATURE [App::DocumentObjectGroupPython] O_element093  label="O_element : 0.766"  # scripted group (container) (typed FeaturePython)
  n = 0.766
FEATURE [App::DocumentObjectGroupPython] Na_element018  label="Na_element : 0.101"  # scripted group (container) (typed FeaturePython)
  n = 0.002
FEATURE [App::DocumentObjectGroupPython] P_element010  label="P_element : 0.108"  # scripted group (container) (typed FeaturePython)
  n = 0.001
FEATURE [App::DocumentObjectGroupPython] S_element021  label="S_element : 0.022"  # scripted group (container) (typed FeaturePython)
  n = 0.002
FEATURE [App::DocumentObjectGroupPython] Cl_element024  label="Cl_element : 0.002"  # scripted group (container) (typed FeaturePython)
  n = 0.002
FEATURE [App::DocumentObjectGroupPython] K_element011  label="K_element : 0.017"  # scripted group (container) (typed FeaturePython)
  n = 0.002
FEATURE [App::DocumentObjectGroupPython] G4_TESTIS_ICRP  # scripted group (container) (typed FeaturePython)
  Dunit = g/cm3
  Dvalue = 1.04
  Group = -> [H_element099,C_element108,N_element041,O_element093,Na_element018,P_element010,S_element021,Cl_element024,K_element011]
  conduct = 2
  density = 1
  expand = 3
  formula = G4_TESTIS_ICRP
  name = G4_TESTIS_ICRP
  specific = 4
FEATURE [App::DocumentObjectGroupPython] C_element109  label="C_element : 060"  # scripted group (container) (typed FeaturePython)
  n = 2
  ref = C_element
FEATURE [App::DocumentObjectGroupPython] Cl_element025  label="Cl_element : 012"  # scripted group (container) (typed FeaturePython)
  n = 4
  ref = Cl_element
FEATURE [App::DocumentObjectGroupPython] G4_TETRACHLOROETHYLENE  # scripted group (container) (typed FeaturePython)
  Dunit = g/cm3
  Dvalue = 1.625
  Group = -> [C_element109,Cl_element025]
  conduct = 2
  density = 1
  expand = 3
  formula = G4_TETRACHLOROETHYLENE
  name = G4_TETRACHLOROETHYLENE
  specific = 4
FEATURE [App::DocumentObjectGroupPython] Tl_element001  label="Tl_element : 1"  # scripted group (container) (typed FeaturePython)
  n = 1
  ref = Tl_element
FEATURE [App::DocumentObjectGroupPython] Cl_element026  label="Cl_element : 013"  # scripted group (container) (typed FeaturePython)
  n = 1
  ref = Cl_element
FEATURE [App::DocumentObjectGroupPython] G4_THALLIUM_CHLORIDE  # scripted group (container) (typed FeaturePython)
  Dunit = g/cm3
  Dvalue = 7.004
  Group = -> [Tl_element001,Cl_element026]
  conduct = 2
  density = 1
  expand = 3
  formula = G4_THALLIUM_CHLORIDE
  name = G4_THALLIUM_CHLORIDE
  specific = 4
FEATURE [App::DocumentObjectGroupPython] H_element100  label="H_element : 0.147"  # scripted group (container) (typed FeaturePython)
  n = 0.105
FEATURE [App::DocumentObjectGroupPython] C_element110  label="C_element : 0.256"  # scripted group (container) (typed FeaturePython)
  n = 0.256
FEATURE [App::DocumentObjectGroupPython] N_element042  label="N_element : 0.760"  # scripted group (container) (typed FeaturePython)
  n = 0.027
FEATURE [App::DocumentObjectGroupPython] O_element094  label="O_element : 0.602"  # scripted group (container) (typed FeaturePython)
  n = 0.602
FEATURE [App::DocumentObjectGroupPython] Na_element019  label="Na_element : 0.102"  # scripted group (container) (typed FeaturePython)
  n = 0.001
FEATURE [App::DocumentObjectGroupPython] P_element011  label="P_element : 0.109"  # scripted group (container) (typed FeaturePython)
  n = 0.002
FEATURE [App::DocumentObjectGroupPython] S_element022  label="S_element : 0.023"  # scripted group (container) (typed FeaturePython)
  n = 0.003
FEATURE [App::DocumentObjectGroupPython] Cl_element027  label="Cl_element : 0.591"  # scripted group (container) (typed FeaturePython)
  n = 0.002
FEATURE [App::DocumentObjectGroupPython] K_element012  label="K_element : 0.018"  # scripted group (container) (typed FeaturePython)
  n = 0.002
FEATURE [App::DocumentObjectGroupPython] G4_TISSUE_SOFT_ICRP  # scripted group (container) (typed FeaturePython)
  Dunit = g/cm3
  Dvalue = 1.03
  Group = -> [H_element100,C_element110,N_element042,O_element094,Na_element019,P_element011,S_element022,Cl_element027,K_element012]
  conduct = 2
  density = 1
  expand = 3
  formula = G4_TISSUE_SOFT_ICRP
  name = G4_TISSUE_SOFT_ICRP
  specific = 4
FEATURE [App::DocumentObjectGroupPython] H_element101  label="H_element : 0.148"  # scripted group (container) (typed FeaturePython)
  n = 0.101
FEATURE [App::DocumentObjectGroupPython] C_element111  label="C_element : 0.111"  # scripted group (container) (typed FeaturePython)
  n = 0.111
FEATURE [App::DocumentObjectGroupPython] N_element043  label="N_element : 0.026"  # scripted group (container) (typed FeaturePython)
  n = 0.026
FEATURE [App::DocumentObjectGroupPython] O_element095  label="O_element : 0.762"  # scripted group (container) (typed FeaturePython)
  n = 0.762
FEATURE [App::DocumentObjectGroupPython] G4_TISSUE_SOFT_ICRU_4  label="G4_TISSUE_SOFT_ICRU-4"  # scripted group (container) (typed FeaturePython)
  Dunit = g/cm3
  Dvalue = 1
  Group = -> [H_element101,C_element111,N_element043,O_element095]
  conduct = 2
  density = 1
  expand = 3
  formula = G4_TISSUE_SOFT_ICRU-4
  name = G4_TISSUE_SOFT_ICRU-4
  specific = 4
FEATURE [App::DocumentObjectGroupPython] H_element102  label="H_element : 0.149"  # scripted group (container) (typed FeaturePython)
  n = 0.101869
FEATURE [App::DocumentObjectGroupPython] C_element112  label="C_element : 0.456"  # scripted group (container) (typed FeaturePython)
  n = 0.456179
FEATURE [App::DocumentObjectGroupPython] N_element044  label="N_element : 0.761"  # scripted group (container) (typed FeaturePython)
  n = 0.035172
FEATURE [App::DocumentObjectGroupPython] O_element096  label="O_element : 0.407"  # scripted group (container) (typed FeaturePython)
  n = 0.40678
FEATURE [App::DocumentObjectGroupPython] G4_TISSUE_METHANE  label="G4_TISSUE-METHANE"  # scripted group (container) (typed FeaturePython)
  Dunit = g/cm3
  Dvalue = 0.00106409
  Group = -> [H_element102,C_element112,N_element044,O_element096]
  conduct = 2
  density = 1
  expand = 3
  formula = G4_TISSUE-METHANE
  name = G4_TISSUE-METHANE
  specific = 4
FEATURE [App::DocumentObjectGroupPython] H_element103  label="H_element : 0.103"  # scripted group (container) (typed FeaturePython)
  n = 0.102672
FEATURE [App::DocumentObjectGroupPython] C_element113  label="C_element : 0.569"  # scripted group (container) (typed FeaturePython)
  n = 0.56894
FEATURE [App::DocumentObjectGroupPython] N_element045  label="N_element : 0.762"  # scripted group (container) (typed FeaturePython)
  n = 0.035022
FEATURE [App::DocumentObjectGroupPython] O_element097  label="O_element : 0.293"  # scripted group (container) (typed FeaturePython)
  n = 0.293366
FEATURE [App::DocumentObjectGroupPython] G4_TISSUE_PROPANE  label="G4_TISSUE-PROPANE"  # scripted group (container) (typed FeaturePython)
  Dunit = g/cm3
  Dvalue = 0.00182628
  Group = -> [H_element103,C_element113,N_element045,O_element097]
  conduct = 2
  density = 1
  expand = 3
  formula = G4_TISSUE-PROPANE
  name = G4_TISSUE-PROPANE
  specific = 4
FEATURE [App::DocumentObjectGroupPython] Ti_element003  label="Ti_element : 1"  # scripted group (container) (typed FeaturePython)
  n = 1
  ref = Ti_element
FEATURE [App::DocumentObjectGroupPython] O_element098  label="O_element : 052"  # scripted group (container) (typed FeaturePython)
  n = 2
  ref = O_element
FEATURE [App::DocumentObjectGroupPython] G4_TITANIUM_DIOXIDE  # scripted group (container) (typed FeaturePython)
  Dunit = g/cm3
  Dvalue = 4.26
  Group = -> [Ti_element003,O_element098]
  conduct = 2
  density = 1
  expand = 3
  formula = G4_TITANIUM_DIOXIDE
  name = G4_TITANIUM_DIOXIDE
  specific = 4
FEATURE [App::DocumentObjectGroupPython] C_element114  label="C_element : 061"  # scripted group (container) (typed FeaturePython)
  n = 7
  ref = C_element
FEATURE [App::DocumentObjectGroupPython] H_element104  label="H_element : 055"  # scripted group (container) (typed FeaturePython)
  n = 8
  ref = H_element
FEATURE [App::DocumentObjectGroupPython] G4_TOLUENE  # scripted group (container) (typed FeaturePython)
  Dunit = g/cm3
  Dvalue = 0.8669
  Group = -> [C_element114,H_element104]
  conduct = 2
  density = 1
  expand = 3
  formula = G4_TOLUENE
  name = G4_TOLUENE
  specific = 4
FEATURE [App::DocumentObjectGroupPython] C_element115  label="C_element : 062"  # scripted group (container) (typed FeaturePython)
  n = 2
  ref = C_element
FEATURE [App::DocumentObjectGroupPython] H_element105  label="H_element : 056"  # scripted group (container) (typed FeaturePython)
  n = 1
  ref = H_element
FEATURE [App::DocumentObjectGroupPython] Cl_element028  label="Cl_element : 014"  # scripted group (container) (typed FeaturePython)
  n = 3
  ref = Cl_element
FEATURE [App::DocumentObjectGroupPython] G4_TRICHLOROETHYLENE  # scripted group (container) (typed FeaturePython)
  Dunit = g/cm3
  Dvalue = 1.46
  Group = -> [C_element115,H_element105,Cl_element028]
  conduct = 2
  density = 1
  expand = 3
  formula = G4_TRICHLOROETHYLENE
  name = G4_TRICHLOROETHYLENE
  specific = 4
FEATURE [App::DocumentObjectGroupPython] C_element116  label="C_element : 063"  # scripted group (container) (typed FeaturePython)
  n = 6
  ref = C_element
FEATURE [App::DocumentObjectGroupPython] H_element106  label="H_element : 15"  # scripted group (container) (typed FeaturePython)
  n = 15
  ref = H_element
FEATURE [App::DocumentObjectGroupPython] O_element099  label="O_element : 053"  # scripted group (container) (typed FeaturePython)
  n = 4
  ref = O_element
FEATURE [App::DocumentObjectGroupPython] P_element012  label="P_element : 1"  # scripted group (container) (typed FeaturePython)
  n = 1
  ref = P_element
FEATURE [App::DocumentObjectGroupPython] G4_TRIETHYL_PHOSPHATE  # scripted group (container) (typed FeaturePython)
  Dunit = g/cm3
  Dvalue = 1.07
  Group = -> [C_element116,H_element106,O_element099,P_element012]
  conduct = 2
  density = 1
  expand = 3
  formula = G4_TRIETHYL_PHOSPHATE
  name = G4_TRIETHYL_PHOSPHATE
  specific = 4
FEATURE [App::DocumentObjectGroupPython] W_element003  label="W_element : 003"  # scripted group (container) (typed FeaturePython)
  n = 1
  ref = W_element
FEATURE [App::DocumentObjectGroupPython] F_element017  label="F_element : 6"  # scripted group (container) (typed FeaturePython)
  n = 6
  ref = F_element
FEATURE [App::DocumentObjectGroupPython] G4_TUNGSTEN_HEXAFLUORIDE  # scripted group (container) (typed FeaturePython)
  Dunit = g/cm3
  Dvalue = 2.4
  Group = -> [W_element003,F_element017]
  conduct = 2
  density = 1
  expand = 3
  formula = G4_TUNGSTEN_HEXAFLUORIDE
  name = G4_TUNGSTEN_HEXAFLUORIDE
  specific = 4
FEATURE [App::DocumentObjectGroupPython] U_element001  label="U_element : 1"  # scripted group (container) (typed FeaturePython)
  n = 1
  ref = U_element
FEATURE [App::DocumentObjectGroupPython] C_element117  label="C_element : 064"  # scripted group (container) (typed FeaturePython)
  n = 2
  ref = C_element
FEATURE [App::DocumentObjectGroupPython] G4_URANIUM_DICARBIDE  # scripted group (container) (typed FeaturePython)
  Dunit = g/cm3
  Dvalue = 11.28
  Group = -> [U_element001,C_element117]
  conduct = 2
  density = 1
  expand = 3
  formula = G4_URANIUM_DICARBIDE
  name = G4_URANIUM_DICARBIDE
  specific = 4
FEATURE [App::DocumentObjectGroupPython] U_element002  label="U_element : 002"  # scripted group (container) (typed FeaturePython)
  n = 1
  ref = U_element
FEATURE [App::DocumentObjectGroupPython] C_element118  label="C_element : 065"  # scripted group (container) (typed FeaturePython)
  n = 1
  ref = C_element
FEATURE [App::DocumentObjectGroupPython] G4_URANIUM_MONOCARBIDE  # scripted group (container) (typed FeaturePython)
  Dunit = g/cm3
  Dvalue = 13.63
  Group = -> [U_element002,C_element118]
  conduct = 2
  density = 1
  expand = 3
  formula = G4_URANIUM_MONOCARBIDE
  name = G4_URANIUM_MONOCARBIDE
  specific = 4
FEATURE [App::DocumentObjectGroupPython] U_element003  label="U_element : 003"  # scripted group (container) (typed FeaturePython)
  n = 1
  ref = U_element
FEATURE [App::DocumentObjectGroupPython] O_element100  label="O_element : 054"  # scripted group (container) (typed FeaturePython)
  n = 2
  ref = O_element
FEATURE [App::DocumentObjectGroupPython] G4_URANIUM_OXIDE  # scripted group (container) (typed FeaturePython)
  Dunit = g/cm3
  Dvalue = 10.96
  Group = -> [U_element003,O_element100]
  conduct = 2
  density = 1
  expand = 3
  formula = G4_URANIUM_OXIDE
  name = G4_URANIUM_OXIDE
  specific = 4
FEATURE [App::DocumentObjectGroupPython] C_element119  label="C_element : 066"  # scripted group (container) (typed FeaturePython)
  n = 1
  ref = C_element
FEATURE [App::DocumentObjectGroupPython] H_element107  label="H_element : 057"  # scripted group (container) (typed FeaturePython)
  n = 4
  ref = H_element
FEATURE [App::DocumentObjectGroupPython] N_element046  label="N_element : 019"  # scripted group (container) (typed FeaturePython)
  n = 2
  ref = N_element
FEATURE [App::DocumentObjectGroupPython] O_element101  label="O_element : 055"  # scripted group (container) (typed FeaturePython)
  n = 1
  ref = O_element
FEATURE [App::DocumentObjectGroupPython] G4_UREA  # scripted group (container) (typed FeaturePython)
  Dunit = g/cm3
  Dvalue = 1.323
  Group = -> [C_element119,H_element107,N_element046,O_element101]
  conduct = 2
  density = 1
  expand = 3
  formula = G4_UREA
  name = G4_UREA
  specific = 4
FEATURE [App::DocumentObjectGroupPython] C_element120  label="C_element : 067"  # scripted group (container) (typed FeaturePython)
  n = 5
  ref = C_element
FEATURE [App::DocumentObjectGroupPython] H_element108  label="H_element : 058"  # scripted group (container) (typed FeaturePython)
  n = 11
  ref = H_element
FEATURE [App::DocumentObjectGroupPython] N_element047  label="N_element : 020"  # scripted group (container) (typed FeaturePython)
  n = 1
  ref = N_element
FEATURE [App::DocumentObjectGroupPython] O_element102  label="O_element : 056"  # scripted group (container) (typed FeaturePython)
  n = 2
  ref = O_element
FEATURE [App::DocumentObjectGroupPython] G4_VALINE  # scripted group (container) (typed FeaturePython)
  Dunit = g/cm3
  Dvalue = 1.23
  Group = -> [C_element120,H_element108,N_element047,O_element102]
  conduct = 2
  density = 1
  expand = 3
  formula = G4_VALINE
  name = G4_VALINE
  specific = 4
FEATURE [App::DocumentObjectGroupPython] H_element109  label="H_element : 0.009"  # scripted group (container) (typed FeaturePython)
  n = 0.009417
FEATURE [App::DocumentObjectGroupPython] C_element121  label="C_element : 0.281"  # scripted group (container) (typed FeaturePython)
  n = 0.280555
FEATURE [App::DocumentObjectGroupPython] F_element018  label="F_element : 0.710"  # scripted group (container) (typed FeaturePython)
  n = 0.710028
FEATURE [App::DocumentObjectGroupPython] G4_VITON  # scripted group (container) (typed FeaturePython)
  Dunit = g/cm3
  Dvalue = 1.8
  Group = -> [H_element109,C_element121,F_element018]
  conduct = 2
  density = 1
  expand = 3
  formula = G4_VITON
  name = G4_VITON
  specific = 4
FEATURE [App::DocumentObjectGroupPython] H_element110  label="H_element : 059"  # scripted group (container) (typed FeaturePython)
  n = 2
  ref = H_element
FEATURE [App::DocumentObjectGroupPython] O_element103  label="O_element : 057"  # scripted group (container) (typed FeaturePython)
  n = 1
  ref = O_element
FEATURE [App::DocumentObjectGroupPython] G4_WATER  # scripted group (container) (typed FeaturePython)
  Dunit = g/cm3
  Dvalue = 1
  Group = -> [H_element110,O_element103]
  conduct = 2
  density = 1
  expand = 3
  formula = G4_WATER
  name = G4_WATER
  specific = 4
FEATURE [App::DocumentObjectGroupPython] H_element111  label="H_element : 060"  # scripted group (container) (typed FeaturePython)
  n = 2
  ref = H_element
FEATURE [App::DocumentObjectGroupPython] O_element104  label="O_element : 058"  # scripted group (container) (typed FeaturePython)
  n = 1
  ref = O_element
FEATURE [App::DocumentObjectGroupPython] G4_WATER_VAPOR  # scripted group (container) (typed FeaturePython)
  Dunit = g/cm3
  Dvalue = 0.000756182
  Group = -> [H_element111,O_element104]
  conduct = 2
  density = 1
  expand = 3
  formula = G4_WATER_VAPOR
  name = G4_WATER_VAPOR
  specific = 4
FEATURE [App::DocumentObjectGroupPython] C_element122  label="C_element : 068"  # scripted group (container) (typed FeaturePython)
  n = 8
  ref = C_element
FEATURE [App::DocumentObjectGroupPython] H_element112  label="H_element : 061"  # scripted group (container) (typed FeaturePython)
  n = 10
  ref = H_element
FEATURE [App::DocumentObjectGroupPython] G4_XYLENE  # scripted group (container) (typed FeaturePython)
  Dunit = g/cm3
  Dvalue = 0.87
  Group = -> [C_element122,H_element112]
  conduct = 2
  density = 1
  expand = 3
  formula = G4_XYLENE
  name = G4_XYLENE
  specific = 4
FEATURE [App::DocumentObjectGroupPython] C_element123  label="C_element : 069"  # scripted group (container) (typed FeaturePython)
  n = 1
  ref = C_element
FEATURE [App::DocumentObjectGroupPython] G4_GRAPHITE  # scripted group (container) (typed FeaturePython)
  Dunit = g/cm3
  Dvalue = 2.21
  Group = -> [C_element123]
  conduct = 2
  density = 1
  expand = 3
  formula = G4_GRAPHITE
  name = G4_GRAPHITE
  specific = 4
FEATURE [App::DocumentObjectGroupPython] NIST  # scripted group (container) (typed FeaturePython)
  Group = -> [G4_A_150_TISSUE,G4_ACETONE,G4_ACETYLENE,G4_ADENINE,G4_ADIPOSE_TISSUE_ICRP,G4_AIR,G4_ALANINE,G4_ALUMINUM_OXIDE,G4_AMBER,G4_AMMONIA,G4_ANILINE,G4_ANTHRACENE,G4_B_100_BONE,G4_BAKELITE,G4_BARIUM_FLUORIDE,G4_BARIUM_SULFATE,G4_BENZENE,G4_BERYLLIUM_OXIDE,G4_BGO,G4_BLOOD_ICRP,G4_BONE_COMPACT_ICRU,G4_BONE_CORTICAL_ICRP,G4_BORON_CARBIDE,G4_BORON_OXIDE,G4_BRAIN_ICRP,G4_BUTANE,G4_N_BUTYL_ALCOHOL,G4_C_552,+152 more]
FEATURE [App::DocumentObjectGroupPython] H_element113  label="H_element : 062"  # scripted group (container) (typed FeaturePython)
  n = 1
  ref = H_element
FEATURE [App::DocumentObjectGroupPython] G4_H  # scripted group (container) (typed FeaturePython)
  Dunit = g/cm3
  Dvalue = 8.3748e-05
  Group = -> [H_element113]
  conduct = 2
  density = 1
  expand = 3
  formula = H
  name = G4_H
  specific = 4
FEATURE [App::DocumentObjectGroupPython] He_element001  label="He_element : 1"  # scripted group (container) (typed FeaturePython)
  n = 1
  ref = He_element
FEATURE [App::DocumentObjectGroupPython] G4_He  # scripted group (container) (typed FeaturePython)
  Dunit = g/cm3
  Dvalue = 0.000166322
  Group = -> [He_element001]
  conduct = 2
  density = 1
  expand = 3
  formula = He
  name = G4_He
  specific = 4
FEATURE [App::DocumentObjectGroupPython] Li_element008  label="Li_element : 008"  # scripted group (container) (typed FeaturePython)
  n = 1
  ref = Li_element
FEATURE [App::DocumentObjectGroupPython] G4_Li  # scripted group (container) (typed FeaturePython)
  Dunit = g/cm3
  Dvalue = 0.534
  Group = -> [Li_element008]
  conduct = 2
  density = 1
  expand = 3
  formula = Li
  name = G4_Li
  specific = 4
FEATURE [App::DocumentObjectGroupPython] Be_element002  label="Be_element : 002"  # scripted group (container) (typed FeaturePython)
  n = 1
  ref = Be_element
FEATURE [App::DocumentObjectGroupPython] G4_Be  # scripted group (container) (typed FeaturePython)
  Dunit = g/cm3
  Dvalue = 1.848
  Group = -> [Be_element002]
  conduct = 2
  density = 1
  expand = 3
  formula = Be
  name = G4_Be
  specific = 4
FEATURE [App::DocumentObjectGroupPython] B_element007  label="B_element : 007"  # scripted group (container) (typed FeaturePython)
  n = 1
  ref = B_element
FEATURE [App::DocumentObjectGroupPython] G4_B  # scripted group (container) (typed FeaturePython)
  Dunit = g/cm3
  Dvalue = 2.37
  Group = -> [B_element007]
  conduct = 2
  density = 1
  expand = 3
  formula = B
  name = G4_B
  specific = 4
FEATURE [App::DocumentObjectGroupPython] C_element124  label="C_element : 070"  # scripted group (container) (typed FeaturePython)
  n = 1
  ref = C_element
FEATURE [App::DocumentObjectGroupPython] G4_C  # scripted group (container) (typed FeaturePython)
  Dunit = g/cm3
  Dvalue = 2
  Group = -> [C_element124]
  conduct = 2
  density = 1
  expand = 3
  formula = C
  name = G4_C
  specific = 4
FEATURE [App::DocumentObjectGroupPython] N_element048  label="N_element : 021"  # scripted group (container) (typed FeaturePython)
  n = 1
  ref = N_element
FEATURE [App::DocumentObjectGroupPython] G4_N  # scripted group (container) (typed FeaturePython)
  Dunit = g/cm3
  Dvalue = 0.0011652
  Group = -> [N_element048]
  conduct = 2
  density = 1
  expand = 3
  formula = N
  name = G4_N
  specific = 4
FEATURE [App::DocumentObjectGroupPython] O_element105  label="O_element : 059"  # scripted group (container) (typed FeaturePython)
  n = 1
  ref = O_element
FEATURE [App::DocumentObjectGroupPython] G4_O  # scripted group (container) (typed FeaturePython)
  Dunit = g/cm3
  Dvalue = 0.00133151
  Group = -> [O_element105]
  conduct = 2
  density = 1
  expand = 3
  formula = O
  name = G4_O
  specific = 4
FEATURE [App::DocumentObjectGroupPython] F_element019  label="F_element : 008"  # scripted group (container) (typed FeaturePython)
  n = 1
  ref = F_element
FEATURE [App::DocumentObjectGroupPython] G4_F  # scripted group (container) (typed FeaturePython)
  Dunit = g/cm3
  Dvalue = 0.00158029
  Group = -> [F_element019]
  conduct = 2
  density = 1
  expand = 3
  formula = F
  name = G4_F
  specific = 4
FEATURE [App::DocumentObjectGroupPython] Ne_element001  label="Ne_element : 1"  # scripted group (container) (typed FeaturePython)
  n = 1
  ref = Ne_element
FEATURE [App::DocumentObjectGroupPython] G4_Ne  # scripted group (container) (typed FeaturePython)
  Dunit = g/cm3
  Dvalue = 0.000838505
  Group = -> [Ne_element001]
  conduct = 2
  density = 1
  expand = 3
  formula = Ne
  name = G4_Ne
  specific = 4
FEATURE [App::DocumentObjectGroupPython] Na_element020  label="Na_element : 005"  # scripted group (container) (typed FeaturePython)
  n = 1
  ref = Na_element
FEATURE [App::DocumentObjectGroupPython] G4_Na  # scripted group (container) (typed FeaturePython)
  Dunit = g/cm3
  Dvalue = 0.971
  Group = -> [Na_element020]
  conduct = 2
  density = 1
  expand = 3
  formula = Na
  name = G4_Na
  specific = 4
FEATURE [App::DocumentObjectGroupPython] Mg_element011  label="Mg_element : 005"  # scripted group (container) (typed FeaturePython)
  n = 1
  ref = Mg_element
FEATURE [App::DocumentObjectGroupPython] G4_Mg  # scripted group (container) (typed FeaturePython)
  Dunit = g/cm3
  Dvalue = 1.74
  Group = -> [Mg_element011]
  conduct = 2
  density = 1
  expand = 3
  formula = Mg
  name = G4_Mg
  specific = 4
FEATURE [App::DocumentObjectGroupPython] Al_element004  label="Al_element : 1"  # scripted group (container) (typed FeaturePython)
  n = 1
  ref = Al_element
FEATURE [App::DocumentObjectGroupPython] G4_Al  # scripted group (container) (typed FeaturePython)
  Dunit = g/cm3
  Dvalue = 2.699
  Group = -> [Al_element004]
  conduct = 2
  density = 1
  expand = 3
  formula = Al
  name = G4_Al
  specific = 4
FEATURE [App::DocumentObjectGroupPython] Si_element007  label="Si_element : 002"  # scripted group (container) (typed FeaturePython)
  n = 1
  ref = Si_element
FEATURE [App::DocumentObjectGroupPython] G4_Si  # scripted group (container) (typed FeaturePython)
  Dunit = g/cm3
  Dvalue = 2.33
  Group = -> [Si_element007]
  conduct = 2
  density = 1
  expand = 3
  formula = Si
  name = G4_Si
  specific = 4
FEATURE [App::DocumentObjectGroupPython] P_element013  label="P_element : 002"  # scripted group (container) (typed FeaturePython)
  n = 1
  ref = P_element
FEATURE [App::DocumentObjectGroupPython] G4_P  # scripted group (container) (typed FeaturePython)
  Dunit = g/cm3
  Dvalue = 2.2
  Group = -> [P_element013]
  conduct = 2
  density = 1
  expand = 3
  formula = P
  name = G4_P
  specific = 4
FEATURE [App::DocumentObjectGroupPython] S_element023  label="S_element : 007"  # scripted group (container) (typed FeaturePython)
  n = 1
  ref = S_element
FEATURE [App::DocumentObjectGroupPython] G4_S  # scripted group (container) (typed FeaturePython)
  Dunit = g/cm3
  Dvalue = 2
  Group = -> [S_element023]
  conduct = 2
  density = 1
  expand = 3
  formula = S
  name = G4_S
  specific = 4
FEATURE [App::DocumentObjectGroupPython] Cl_element029  label="Cl_element : 015"  # scripted group (container) (typed FeaturePython)
  n = 1
  ref = Cl_element
FEATURE [App::DocumentObjectGroupPython] G4_Cl  # scripted group (container) (typed FeaturePython)
  Dunit = g/cm3
  Dvalue = 0.00299473
  Group = -> [Cl_element029]
  conduct = 2
  density = 1
  expand = 3
  formula = Cl
  name = G4_Cl
  specific = 4
FEATURE [App::DocumentObjectGroupPython] Ar_element002  label="Ar_element : 1"  # scripted group (container) (typed FeaturePython)
  n = 1
  ref = Ar_element
FEATURE [App::DocumentObjectGroupPython] G4_Ar  # scripted group (container) (typed FeaturePython)
  Dunit = g/cm3
  Dvalue = 0.00166201
  Group = -> [Ar_element002]
  conduct = 2
  density = 1
  expand = 3
  formula = Ar
  name = G4_Ar
  specific = 4
FEATURE [App::DocumentObjectGroupPython] K_element013  label="K_element : 003"  # scripted group (container) (typed FeaturePython)
  n = 1
  ref = K_element
FEATURE [App::DocumentObjectGroupPython] G4_K  # scripted group (container) (typed FeaturePython)
  Dunit = g/cm3
  Dvalue = 0.862
  Group = -> [K_element013]
  conduct = 2
  density = 1
  expand = 3
  formula = K
  name = G4_K
  specific = 4
FEATURE [App::DocumentObjectGroupPython] Ca_element014  label="Ca_element : 007"  # scripted group (container) (typed FeaturePython)
  n = 1
  ref = Ca_element
FEATURE [App::DocumentObjectGroupPython] G4_Ca  # scripted group (container) (typed FeaturePython)
  Dunit = g/cm3
  Dvalue = 1.55
  Group = -> [Ca_element014]
  conduct = 2
  density = 1
  expand = 3
  formula = Ca
  name = G4_Ca
  specific = 4
FEATURE [App::DocumentObjectGroupPython] Sc_element001  label="Sc_element : 1"  # scripted group (container) (typed FeaturePython)
  n = 1
  ref = Sc_element
FEATURE [App::DocumentObjectGroupPython] G4_Sc  # scripted group (container) (typed FeaturePython)
  Dunit = g/cm3
  Dvalue = 2.989
  Group = -> [Sc_element001]
  conduct = 2
  density = 1
  expand = 3
  formula = Sc
  name = G4_Sc
  specific = 4
FEATURE [App::DocumentObjectGroupPython] Ti_element004  label="Ti_element : 002"  # scripted group (container) (typed FeaturePython)
  n = 1
  ref = Ti_element
FEATURE [App::DocumentObjectGroupPython] G4_Ti  # scripted group (container) (typed FeaturePython)
  Dunit = g/cm3
  Dvalue = 4.54
  Group = -> [Ti_element004]
  conduct = 2
  density = 1
  expand = 3
  formula = Ti
  name = G4_Ti
  specific = 4
FEATURE [App::DocumentObjectGroupPython] V_element001  label="V_element : 1"  # scripted group (container) (typed FeaturePython)
  n = 1
  ref = V_element
FEATURE [App::DocumentObjectGroupPython] G4_V  # scripted group (container) (typed FeaturePython)
  Dunit = g/cm3
  Dvalue = 6.11
  Group = -> [V_element001]
  conduct = 2
  density = 1
  expand = 3
  formula = V
  name = G4_V
  specific = 4
FEATURE [App::DocumentObjectGroupPython] Cr_element001  label="Cr_element : 1"  # scripted group (container) (typed FeaturePython)
  n = 1
  ref = Cr_element
FEATURE [App::DocumentObjectGroupPython] G4_Cr  # scripted group (container) (typed FeaturePython)
  Dunit = g/cm3
  Dvalue = 7.18
  Group = -> [Cr_element001]
  conduct = 2
  density = 1
  expand = 3
  formula = Cr
  name = G4_Cr
  specific = 4
FEATURE [App::DocumentObjectGroupPython] Mn_element001  label="Mn_element : 1"  # scripted group (container) (typed FeaturePython)
  n = 1
  ref = Mn_element
FEATURE [App::DocumentObjectGroupPython] G4_Mn  # scripted group (container) (typed FeaturePython)
  Dunit = g/cm3
  Dvalue = 7.44
  Group = -> [Mn_element001]
  conduct = 2
  density = 1
  expand = 3
  formula = Mn
  name = G4_Mn
  specific = 4
FEATURE [App::DocumentObjectGroupPython] Fe_element007  label="Fe_element : 004"  # scripted group (container) (typed FeaturePython)
  n = 1
  ref = Fe_element
FEATURE [App::DocumentObjectGroupPython] G4_Fe  # scripted group (container) (typed FeaturePython)
  Dunit = g/cm3
  Dvalue = 7.874
  Group = -> [Fe_element007]
  conduct = 2
  density = 1
  expand = 3
  formula = Fe
  name = G4_Fe
  specific = 4
FEATURE [App::DocumentObjectGroupPython] Co_element001  label="Co_element : 1"  # scripted group (container) (typed FeaturePython)
  n = 1
  ref = Co_element
FEATURE [App::DocumentObjectGroupPython] G4_Co  # scripted group (container) (typed FeaturePython)
  Dunit = g/cm3
  Dvalue = 8.9
  Group = -> [Co_element001]
  conduct = 2
  density = 1
  expand = 3
  formula = Co
  name = G4_Co
  specific = 4
FEATURE [App::DocumentObjectGroupPython] Ni_element001  label="Ni_element : 1"  # scripted group (container) (typed FeaturePython)
  n = 1
  ref = Ni_element
FEATURE [App::DocumentObjectGroupPython] G4_Ni  # scripted group (container) (typed FeaturePython)
  Dunit = g/cm3
  Dvalue = 8.902
  Group = -> [Ni_element001]
  conduct = 2
  density = 1
  expand = 3
  formula = Ni
  name = G4_Ni
  specific = 4
FEATURE [App::DocumentObjectGroupPython] Cu_element001  label="Cu_element : 1"  # scripted group (container) (typed FeaturePython)
  n = 1
  ref = Cu_element
FEATURE [App::DocumentObjectGroupPython] G4_Cu  # scripted group (container) (typed FeaturePython)
  Dunit = g/cm3
  Dvalue = 8.96
  Group = -> [Cu_element001]
  conduct = 2
  density = 1
  expand = 3
  formula = Cu
  name = G4_Cu
  specific = 4
FEATURE [App::DocumentObjectGroupPython] Zn_element001  label="Zn_element : 1"  # scripted group (container) (typed FeaturePython)
  n = 1
  ref = Zn_element
FEATURE [App::DocumentObjectGroupPython] G4_Zn  # scripted group (container) (typed FeaturePython)
  Dunit = g/cm3
  Dvalue = 7.133
  Group = -> [Zn_element001]
  conduct = 2
  density = 1
  expand = 3
  formula = Zn
  name = G4_Zn
  specific = 4
FEATURE [App::DocumentObjectGroupPython] Ga_element002  label="Ga_element : 002"  # scripted group (container) (typed FeaturePython)
  n = 1
  ref = Ga_element
FEATURE [App::DocumentObjectGroupPython] G4_Ga  # scripted group (container) (typed FeaturePython)
  Dunit = g/cm3
  Dvalue = 5.904
  Group = -> [Ga_element002]
  conduct = 2
  density = 1
  expand = 3
  formula = Ga
  name = G4_Ga
  specific = 4
FEATURE [App::DocumentObjectGroupPython] Ge_element002  label="Ge_element : 1"  # scripted group (container) (typed FeaturePython)
  n = 1
  ref = Ge_element
FEATURE [App::DocumentObjectGroupPython] G4_Ge  # scripted group (container) (typed FeaturePython)
  Dunit = g/cm3
  Dvalue = 5.323
  Group = -> [Ge_element002]
  conduct = 2
  density = 1
  expand = 3
  formula = Ge
  name = G4_Ge
  specific = 4
FEATURE [App::DocumentObjectGroupPython] As_element003  label="As_element : 002"  # scripted group (container) (typed FeaturePython)
  n = 1
  ref = As_element
FEATURE [App::DocumentObjectGroupPython] G4_As  # scripted group (container) (typed FeaturePython)
  Dunit = g/cm3
  Dvalue = 5.73
  Group = -> [As_element003]
  conduct = 2
  density = 1
  expand = 3
  formula = As
  name = G4_As
  specific = 4
FEATURE [App::DocumentObjectGroupPython] Se_element001  label="Se_element : 1"  # scripted group (container) (typed FeaturePython)
  n = 1
  ref = Se_element
FEATURE [App::DocumentObjectGroupPython] G4_Se  # scripted group (container) (typed FeaturePython)
  Dunit = g/cm3
  Dvalue = 4.5
  Group = -> [Se_element001]
  conduct = 2
  density = 1
  expand = 3
  formula = Se
  name = G4_Se
  specific = 4
FEATURE [App::DocumentObjectGroupPython] Br_element007  label="Br_element : 004"  # scripted group (container) (typed FeaturePython)
  n = 1
  ref = Br_element
FEATURE [App::DocumentObjectGroupPython] G4_Br  # scripted group (container) (typed FeaturePython)
  Dunit = g/cm3
  Dvalue = 0.0070721
  Group = -> [Br_element007]
  conduct = 2
  density = 1
  expand = 3
  formula = Br
  name = G4_Br
  specific = 4
FEATURE [App::DocumentObjectGroupPython] Kr_element001  label="Kr_element : 1"  # scripted group (container) (typed FeaturePython)
  n = 1
  ref = Kr_element
FEATURE [App::DocumentObjectGroupPython] G4_Kr  # scripted group (container) (typed FeaturePython)
  Dunit = g/cm3
  Dvalue = 0.00347832
  Group = -> [Kr_element001]
  conduct = 2
  density = 1
  expand = 3
  formula = Kr
  name = G4_Kr
  specific = 4
FEATURE [App::DocumentObjectGroupPython] Rb_element001  label="Rb_element : 1"  # scripted group (container) (typed FeaturePython)
  n = 1
  ref = Rb_element
FEATURE [App::DocumentObjectGroupPython] G4_Rb  # scripted group (container) (typed FeaturePython)
  Dunit = g/cm3
  Dvalue = 1.532
  Group = -> [Rb_element001]
  conduct = 2
  density = 1
  expand = 3
  formula = Rb
  name = G4_Rb
  specific = 4
FEATURE [App::DocumentObjectGroupPython] Sr_element001  label="Sr_element : 1"  # scripted group (container) (typed FeaturePython)
  n = 1
  ref = Sr_element
FEATURE [App::DocumentObjectGroupPython] G4_Sr  # scripted group (container) (typed FeaturePython)
  Dunit = g/cm3
  Dvalue = 2.54
  Group = -> [Sr_element001]
  conduct = 2
  density = 1
  expand = 3
  formula = Sr
  name = G4_Sr
  specific = 4
FEATURE [App::DocumentObjectGroupPython] Y_element001  label="Y_element : 1"  # scripted group (container) (typed FeaturePython)
  n = 1
  ref = Y_element
FEATURE [App::DocumentObjectGroupPython] G4_Y  # scripted group (container) (typed FeaturePython)
  Dunit = g/cm3
  Dvalue = 4.469
  Group = -> [Y_element001]
  conduct = 2
  density = 1
  expand = 3
  formula = Y
  name = G4_Y
  specific = 4
FEATURE [App::DocumentObjectGroupPython] Zr_element001  label="Zr_element : 1"  # scripted group (container) (typed FeaturePython)
  n = 1
  ref = Zr_element
FEATURE [App::DocumentObjectGroupPython] G4_Zr  # scripted group (container) (typed FeaturePython)
  Dunit = g/cm3
  Dvalue = 6.506
  Group = -> [Zr_element001]
  conduct = 2
  density = 1
  expand = 3
  formula = Zr
  name = G4_Zr
  specific = 4
FEATURE [App::DocumentObjectGroupPython] Nb_element001  label="Nb_element : 1"  # scripted group (container) (typed FeaturePython)
  n = 1
  ref = Nb_element
FEATURE [App::DocumentObjectGroupPython] G4_Nb  # scripted group (container) (typed FeaturePython)
  Dunit = g/cm3
  Dvalue = 8.57
  Group = -> [Nb_element001]
  conduct = 2
  density = 1
  expand = 3
  formula = Nb
  name = G4_Nb
  specific = 4
FEATURE [App::DocumentObjectGroupPython] Mo_element001  label="Mo_element : 1"  # scripted group (container) (typed FeaturePython)
  n = 1
  ref = Mo_element
FEATURE [App::DocumentObjectGroupPython] G4_Mo  # scripted group (container) (typed FeaturePython)
  Dunit = g/cm3
  Dvalue = 10.22
  Group = -> [Mo_element001]
  conduct = 2
  density = 1
  expand = 3
  formula = Mo
  name = G4_Mo
  specific = 4
FEATURE [App::DocumentObjectGroupPython] Tc_element001  label="Tc_element : 1"  # scripted group (container) (typed FeaturePython)
  n = 1
  ref = Tc_element
FEATURE [App::DocumentObjectGroupPython] G4_Tc  # scripted group (container) (typed FeaturePython)
  Dunit = g/cm3
  Dvalue = 11.5
  Group = -> [Tc_element001]
  conduct = 2
  density = 1
  expand = 3
  formula = Tc
  name = G4_Tc
  specific = 4
FEATURE [App::DocumentObjectGroupPython] Ru_element001  label="Ru_element : 1"  # scripted group (container) (typed FeaturePython)
  n = 1
  ref = Ru_element
FEATURE [App::DocumentObjectGroupPython] G4_Ru  # scripted group (container) (typed FeaturePython)
  Dunit = g/cm3
  Dvalue = 12.41
  Group = -> [Ru_element001]
  conduct = 2
  density = 1
  expand = 3
  formula = Ru
  name = G4_Ru
  specific = 4
FEATURE [App::DocumentObjectGroupPython] Rh_element001  label="Rh_element : 1"  # scripted group (container) (typed FeaturePython)
  n = 1
  ref = Rh_element
FEATURE [App::DocumentObjectGroupPython] G4_Rh  # scripted group (container) (typed FeaturePython)
  Dunit = g/cm3
  Dvalue = 12.41
  Group = -> [Rh_element001]
  conduct = 2
  density = 1
  expand = 3
  formula = Rh
  name = G4_Rh
  specific = 4
FEATURE [App::DocumentObjectGroupPython] Pd_element001  label="Pd_element : 1"  # scripted group (container) (typed FeaturePython)
  n = 1
  ref = Pd_element
FEATURE [App::DocumentObjectGroupPython] G4_Pd  # scripted group (container) (typed FeaturePython)
  Dunit = g/cm3
  Dvalue = 12.02
  Group = -> [Pd_element001]
  conduct = 2
  density = 1
  expand = 3
  formula = Pd
  name = G4_Pd
  specific = 4
FEATURE [App::DocumentObjectGroupPython] Ag_element006  label="Ag_element : 004"  # scripted group (container) (typed FeaturePython)
  n = 1
  ref = Ag_element
FEATURE [App::DocumentObjectGroupPython] G4_Ag  # scripted group (container) (typed FeaturePython)
  Dunit = g/cm3
  Dvalue = 10.5
  Group = -> [Ag_element006]
  conduct = 2
  density = 1
  expand = 3
  formula = Ag
  name = G4_Ag
  specific = 4
FEATURE [App::DocumentObjectGroupPython] Cd_element003  label="Cd_element : 003"  # scripted group (container) (typed FeaturePython)
  n = 1
  ref = Cd_element
FEATURE [App::DocumentObjectGroupPython] G4_Cd  # scripted group (container) (typed FeaturePython)
  Dunit = g/cm3
  Dvalue = 8.65
  Group = -> [Cd_element003]
  conduct = 2
  density = 1
  expand = 3
  formula = Cd
  name = G4_Cd
  specific = 4
FEATURE [App::DocumentObjectGroupPython] In_element001  label="In_element : 1"  # scripted group (container) (typed FeaturePython)
  n = 1
  ref = In_element
FEATURE [App::DocumentObjectGroupPython] G4_In  # scripted group (container) (typed FeaturePython)
  Dunit = g/cm3
  Dvalue = 7.31
  Group = -> [In_element001]
  conduct = 2
  density = 1
  expand = 3
  formula = In
  name = G4_In
  specific = 4
FEATURE [App::DocumentObjectGroupPython] Sn_element001  label="Sn_element : 1"  # scripted group (container) (typed FeaturePython)
  n = 1
  ref = Sn_element
FEATURE [App::DocumentObjectGroupPython] G4_Sn  # scripted group (container) (typed FeaturePython)
  Dunit = g/cm3
  Dvalue = 7.31
  Group = -> [Sn_element001]
  conduct = 2
  density = 1
  expand = 3
  formula = Sn
  name = G4_Sn
  specific = 4
FEATURE [App::DocumentObjectGroupPython] Sb_element001  label="Sb_element : 1"  # scripted group (container) (typed FeaturePython)
  n = 1
  ref = Sb_element
FEATURE [App::DocumentObjectGroupPython] G4_Sb  # scripted group (container) (typed FeaturePython)
  Dunit = g/cm3
  Dvalue = 6.691
  Group = -> [Sb_element001]
  conduct = 2
  density = 1
  expand = 3
  formula = Sb
  name = G4_Sb
  specific = 4
FEATURE [App::DocumentObjectGroupPython] Te_element002  label="Te_element : 002"  # scripted group (container) (typed FeaturePython)
  n = 1
  ref = Te_element
FEATURE [App::DocumentObjectGroupPython] G4_Te  # scripted group (container) (typed FeaturePython)
  Dunit = g/cm3
  Dvalue = 6.24
  Group = -> [Te_element002]
  conduct = 2
  density = 1
  expand = 3
  formula = Te
  name = G4_Te
  specific = 4
FEATURE [App::DocumentObjectGroupPython] I_element010  label="I_element : 006"  # scripted group (container) (typed FeaturePython)
  n = 1
  ref = I_element
FEATURE [App::DocumentObjectGroupPython] G4_I  # scripted group (container) (typed FeaturePython)
  Dunit = g/cm3
  Dvalue = 4.93
  Group = -> [I_element010]
  conduct = 2
  density = 1
  expand = 3
  formula = I
  name = G4_I
  specific = 4
FEATURE [App::DocumentObjectGroupPython] Xe_element001  label="Xe_element : 1"  # scripted group (container) (typed FeaturePython)
  n = 1
  ref = Xe_element
FEATURE [App::DocumentObjectGroupPython] G4_Xe  # scripted group (container) (typed FeaturePython)
  Dunit = g/cm3
  Dvalue = 0.00548536
  Group = -> [Xe_element001]
  conduct = 2
  density = 1
  expand = 3
  formula = Xe
  name = G4_Xe
  specific = 4
FEATURE [App::DocumentObjectGroupPython] Cs_element003  label="Cs_element : 003"  # scripted group (container) (typed FeaturePython)
  n = 1
  ref = Cs_element
FEATURE [App::DocumentObjectGroupPython] G4_Cs  # scripted group (container) (typed FeaturePython)
  Dunit = g/cm3
  Dvalue = 1.873
  Group = -> [Cs_element003]
  conduct = 2
  density = 1
  expand = 3
  formula = Cs
  name = G4_Cs
  specific = 4
FEATURE [App::DocumentObjectGroupPython] Ba_element003  label="Ba_element : 003"  # scripted group (container) (typed FeaturePython)
  n = 1
  ref = Ba_element
FEATURE [App::DocumentObjectGroupPython] G4_Ba  # scripted group (container) (typed FeaturePython)
  Dunit = g/cm3
  Dvalue = 3.5
  Group = -> [Ba_element003]
  conduct = 2
  density = 1
  expand = 3
  formula = Ba
  name = G4_Ba
  specific = 4
FEATURE [App::DocumentObjectGroupPython] La_element003  label="La_element : 003"  # scripted group (container) (typed FeaturePython)
  n = 1
  ref = La_element
FEATURE [App::DocumentObjectGroupPython] G4_La  # scripted group (container) (typed FeaturePython)
  Dunit = g/cm3
  Dvalue = 6.154
  Group = -> [La_element003]
  conduct = 2
  density = 1
  expand = 3
  formula = La
  name = G4_La
  specific = 4
FEATURE [App::DocumentObjectGroupPython] Ce_element002  label="Ce_element : 1"  # scripted group (container) (typed FeaturePython)
  n = 1
  ref = Ce_element
FEATURE [App::DocumentObjectGroupPython] G4_Ce  # scripted group (container) (typed FeaturePython)
  Dunit = g/cm3
  Dvalue = 6.657
  Group = -> [Ce_element002]
  conduct = 2
  density = 1
  expand = 3
  formula = Ce
  name = G4_Ce
  specific = 4
FEATURE [App::DocumentObjectGroupPython] Pr_element001  label="Pr_element : 1"  # scripted group (container) (typed FeaturePython)
  n = 1
  ref = Pr_element
FEATURE [App::DocumentObjectGroupPython] G4_Pr  # scripted group (container) (typed FeaturePython)
  Dunit = g/cm3
  Dvalue = 6.71
  Group = -> [Pr_element001]
  conduct = 2
  density = 1
  expand = 3
  formula = Pr
  name = G4_Pr
  specific = 4
FEATURE [App::DocumentObjectGroupPython] Nd_element001  label="Nd_element : 1"  # scripted group (container) (typed FeaturePython)
  n = 1
  ref = Nd_element
FEATURE [App::DocumentObjectGroupPython] G4_Nd  # scripted group (container) (typed FeaturePython)
  Dunit = g/cm3
  Dvalue = 6.9
  Group = -> [Nd_element001]
  conduct = 2
  density = 1
  expand = 3
  formula = Nd
  name = G4_Nd
  specific = 4
FEATURE [App::DocumentObjectGroupPython] Pm_element001  label="Pm_element : 1"  # scripted group (container) (typed FeaturePython)
  n = 1
  ref = Pm_element
FEATURE [App::DocumentObjectGroupPython] G4_Pm  # scripted group (container) (typed FeaturePython)
  Dunit = g/cm3
  Dvalue = 7.22
  Group = -> [Pm_element001]
  conduct = 2
  density = 1
  expand = 3
  formula = Pm
  name = G4_Pm
  specific = 4
FEATURE [App::DocumentObjectGroupPython] Sm_element001  label="Sm_element : 1"  # scripted group (container) (typed FeaturePython)
  n = 1
  ref = Sm_element
FEATURE [App::DocumentObjectGroupPython] G4_Sm  # scripted group (container) (typed FeaturePython)
  Dunit = g/cm3
  Dvalue = 7.46
  Group = -> [Sm_element001]
  conduct = 2
  density = 1
  expand = 3
  formula = Sm
  name = G4_Sm
  specific = 4
FEATURE [App::DocumentObjectGroupPython] Eu_element001  label="Eu_element : 1"  # scripted group (container) (typed FeaturePython)
  n = 1
  ref = Eu_element
FEATURE [App::DocumentObjectGroupPython] G4_Eu  # scripted group (container) (typed FeaturePython)
  Dunit = g/cm3
  Dvalue = 5.243
  Group = -> [Eu_element001]
  conduct = 2
  density = 1
  expand = 3
  formula = Eu
  name = G4_Eu
  specific = 4
FEATURE [App::DocumentObjectGroupPython] Gd_element002  label="Gd_element : 1"  # scripted group (container) (typed FeaturePython)
  n = 1
  ref = Gd_element
FEATURE [App::DocumentObjectGroupPython] G4_Gd  # scripted group (container) (typed FeaturePython)
  Dunit = g/cm3
  Dvalue = 7.9004
  Group = -> [Gd_element002]
  conduct = 2
  density = 1
  expand = 3
  formula = Gd
  name = G4_Gd
  specific = 4
FEATURE [App::DocumentObjectGroupPython] Tb_element001  label="Tb_element : 1"  # scripted group (container) (typed FeaturePython)
  n = 1
  ref = Tb_element
FEATURE [App::DocumentObjectGroupPython] G4_Tb  # scripted group (container) (typed FeaturePython)
  Dunit = g/cm3
  Dvalue = 8.229
  Group = -> [Tb_element001]
  conduct = 2
  density = 1
  expand = 3
  formula = Tb
  name = G4_Tb
  specific = 4
FEATURE [App::DocumentObjectGroupPython] Dy_element001  label="Dy_element : 1"  # scripted group (container) (typed FeaturePython)
  n = 1
  ref = Dy_element
FEATURE [App::DocumentObjectGroupPython] G4_Dy  # scripted group (container) (typed FeaturePython)
  Dunit = g/cm3
  Dvalue = 8.55
  Group = -> [Dy_element001]
  conduct = 2
  density = 1
  expand = 3
  formula = Dy
  name = G4_Dy
  specific = 4
FEATURE [App::DocumentObjectGroupPython] Ho_element001  label="Ho_element : 1"  # scripted group (container) (typed FeaturePython)
  n = 1
  ref = Ho_element
FEATURE [App::DocumentObjectGroupPython] G4_Ho  # scripted group (container) (typed FeaturePython)
  Dunit = g/cm3
  Dvalue = 8.795
  Group = -> [Ho_element001]
  conduct = 2
  density = 1
  expand = 3
  formula = Ho
  name = G4_Ho
  specific = 4
FEATURE [App::DocumentObjectGroupPython] Er_element001  label="Er_element : 1"  # scripted group (container) (typed FeaturePython)
  n = 1
  ref = Er_element
FEATURE [App::DocumentObjectGroupPython] G4_Er  # scripted group (container) (typed FeaturePython)
  Dunit = g/cm3
  Dvalue = 9.066
  Group = -> [Er_element001]
  conduct = 2
  density = 1
  expand = 3
  formula = Er
  name = G4_Er
  specific = 4
FEATURE [App::DocumentObjectGroupPython] Tm_element001  label="Tm_element : 1"  # scripted group (container) (typed FeaturePython)
  n = 1
  ref = Tm_element
FEATURE [App::DocumentObjectGroupPython] G4_Tm  # scripted group (container) (typed FeaturePython)
  Dunit = g/cm3
  Dvalue = 9.321
  Group = -> [Tm_element001]
  conduct = 2
  density = 1
  expand = 3
  formula = Tm
  name = G4_Tm
  specific = 4
FEATURE [App::DocumentObjectGroupPython] Yb_element001  label="Yb_element : 1"  # scripted group (container) (typed FeaturePython)
  n = 1
  ref = Yb_element
FEATURE [App::DocumentObjectGroupPython] G4_Yb  # scripted group (container) (typed FeaturePython)
  Dunit = g/cm3
  Dvalue = 6.73
  Group = -> [Yb_element001]
  conduct = 2
  density = 1
  expand = 3
  formula = Yb
  name = G4_Yb
  specific = 4
FEATURE [App::DocumentObjectGroupPython] Lu_element001  label="Lu_element : 1"  # scripted group (container) (typed FeaturePython)
  n = 1
  ref = Lu_element
FEATURE [App::DocumentObjectGroupPython] G4_Lu  # scripted group (container) (typed FeaturePython)
  Dunit = g/cm3
  Dvalue = 9.84
  Group = -> [Lu_element001]
  conduct = 2
  density = 1
  expand = 3
  formula = Lu
  name = G4_Lu
  specific = 4
FEATURE [App::DocumentObjectGroupPython] Hf_element001  label="Hf_element : 1"  # scripted group (container) (typed FeaturePython)
  n = 1
  ref = Hf_element
FEATURE [App::DocumentObjectGroupPython] G4_Hf  # scripted group (container) (typed FeaturePython)
  Dunit = g/cm3
  Dvalue = 13.31
  Group = -> [Hf_element001]
  conduct = 2
  density = 1
  expand = 3
  formula = Hf
  name = G4_Hf
  specific = 4
FEATURE [App::DocumentObjectGroupPython] Ta_element001  label="Ta_element : 1"  # scripted group (container) (typed FeaturePython)
  n = 1
  ref = Ta_element
FEATURE [App::DocumentObjectGroupPython] G4_Ta  # scripted group (container) (typed FeaturePython)
  Dunit = g/cm3
  Dvalue = 16.654
  Group = -> [Ta_element001]
  conduct = 2
  density = 1
  expand = 3
  formula = Ta
  name = G4_Ta
  specific = 4
FEATURE [App::DocumentObjectGroupPython] W_element004  label="W_element : 004"  # scripted group (container) (typed FeaturePython)
  n = 1
  ref = W_element
FEATURE [App::DocumentObjectGroupPython] G4_W  # scripted group (container) (typed FeaturePython)
  Dunit = g/cm3
  Dvalue = 19.3
  Group = -> [W_element004]
  conduct = 2
  density = 1
  expand = 3
  formula = W
  name = G4_W
  specific = 4
FEATURE [App::DocumentObjectGroupPython] Re_element001  label="Re_element : 1"  # scripted group (container) (typed FeaturePython)
  n = 1
  ref = Re_element
FEATURE [App::DocumentObjectGroupPython] G4_Re  # scripted group (container) (typed FeaturePython)
  Dunit = g/cm3
  Dvalue = 21.02
  Group = -> [Re_element001]
  conduct = 2
  density = 1
  expand = 3
  formula = Re
  name = G4_Re
  specific = 4
FEATURE [App::DocumentObjectGroupPython] Os_element001  label="Os_element : 1"  # scripted group (container) (typed FeaturePython)
  n = 1
  ref = Os_element
FEATURE [App::DocumentObjectGroupPython] G4_Os  # scripted group (container) (typed FeaturePython)
  Dunit = g/cm3
  Dvalue = 22.57
  Group = -> [Os_element001]
  conduct = 2
  density = 1
  expand = 3
  formula = Os
  name = G4_Os
  specific = 4
FEATURE [App::DocumentObjectGroupPython] Ir_element001  label="Ir_element : 1"  # scripted group (container) (typed FeaturePython)
  n = 1
  ref = Ir_element
FEATURE [App::DocumentObjectGroupPython] G4_Ir  # scripted group (container) (typed FeaturePython)
  Dunit = g/cm3
  Dvalue = 22.42
  Group = -> [Ir_element001]
  conduct = 2
  density = 1
  expand = 3
  formula = Ir
  name = G4_Ir
  specific = 4
FEATURE [App::DocumentObjectGroupPython] Pt_element001  label="Pt_element : 1"  # scripted group (container) (typed FeaturePython)
  n = 1
  ref = Pt_element
FEATURE [App::DocumentObjectGroupPython] G4_Pt  # scripted group (container) (typed FeaturePython)
  Dunit = g/cm3
  Dvalue = 21.45
  Group = -> [Pt_element001]
  conduct = 2
  density = 1
  expand = 3
  formula = Pt
  name = G4_Pt
  specific = 4
FEATURE [App::DocumentObjectGroupPython] Au_element001  label="Au_element : 1"  # scripted group (container) (typed FeaturePython)
  n = 1
  ref = Au_element
FEATURE [App::DocumentObjectGroupPython] G4_Au  # scripted group (container) (typed FeaturePython)
  Dunit = g/cm3
  Dvalue = 19.32
  Group = -> [Au_element001]
  conduct = 2
  density = 1
  expand = 3
  formula = Au
  name = G4_Au
  specific = 4
FEATURE [App::DocumentObjectGroupPython] Hg_element002  label="Hg_element : 002"  # scripted group (container) (typed FeaturePython)
  n = 1
  ref = Hg_element
FEATURE [App::DocumentObjectGroupPython] G4_Hg  # scripted group (container) (typed FeaturePython)
  Dunit = g/cm3
  Dvalue = 13.546
  Group = -> [Hg_element002]
  conduct = 2
  density = 1
  expand = 3
  formula = Hg
  name = G4_Hg
  specific = 4
FEATURE [App::DocumentObjectGroupPython] Tl_element002  label="Tl_element : 002"  # scripted group (container) (typed FeaturePython)
  n = 1
  ref = Tl_element
FEATURE [App::DocumentObjectGroupPython] G4_Tl  # scripted group (container) (typed FeaturePython)
  Dunit = g/cm3
  Dvalue = 11.72
  Group = -> [Tl_element002]
  conduct = 2
  density = 1
  expand = 3
  formula = Tl
  name = G4_Tl
  specific = 4
FEATURE [App::DocumentObjectGroupPython] Pb_element003  label="Pb_element : 1"  # scripted group (container) (typed FeaturePython)
  n = 1
  ref = Pb_element
FEATURE [App::DocumentObjectGroupPython] G4_Pb  # scripted group (container) (typed FeaturePython)
  Dunit = g/cm3
  Dvalue = 11.35
  Group = -> [Pb_element003]
  conduct = 2
  density = 1
  expand = 3
  formula = Pb
  name = G4_Pb
  specific = 4
FEATURE [App::DocumentObjectGroupPython] Bi_element002  label="Bi_element : 1"  # scripted group (container) (typed FeaturePython)
  n = 1
  ref = Bi_element
FEATURE [App::DocumentObjectGroupPython] G4_Bi  # scripted group (container) (typed FeaturePython)
  Dunit = g/cm3
  Dvalue = 9.747
  Group = -> [Bi_element002]
  conduct = 2
  density = 1
  expand = 3
  formula = Bi
  name = G4_Bi
  specific = 4
FEATURE [App::DocumentObjectGroupPython] Po_element001  label="Po_element : 1"  # scripted group (container) (typed FeaturePython)
  n = 1
  ref = Po_element
FEATURE [App::DocumentObjectGroupPython] G4_Po  # scripted group (container) (typed FeaturePython)
  Dunit = g/cm3
  Dvalue = 9.32
  Group = -> [Po_element001]
  conduct = 2
  density = 1
  expand = 3
  formula = Po
  name = G4_Po
  specific = 4
FEATURE [App::DocumentObjectGroupPython] At_element001  label="At_element : 1"  # scripted group (container) (typed FeaturePython)
  n = 1
  ref = At_element
FEATURE [App::DocumentObjectGroupPython] G4_At  # scripted group (container) (typed FeaturePython)
  Dunit = g/cm3
  Dvalue = 9.32
  Group = -> [At_element001]
  conduct = 2
  density = 1
  expand = 3
  formula = At
  name = G4_At
  specific = 4
FEATURE [App::DocumentObjectGroupPython] Rn_element001  label="Rn_element : 1"  # scripted group (container) (typed FeaturePython)
  n = 1
  ref = Rn_element
FEATURE [App::DocumentObjectGroupPython] G4_Rn  # scripted group (container) (typed FeaturePython)
  Dunit = g/cm3
  Dvalue = 0.00900662
  Group = -> [Rn_element001]
  conduct = 2
  density = 1
  expand = 3
  formula = Rn
  name = G4_Rn
  specific = 4
FEATURE [App::DocumentObjectGroupPython] Fr_element001  label="Fr_element : 1"  # scripted group (container) (typed FeaturePython)
  n = 1
  ref = Fr_element
FEATURE [App::DocumentObjectGroupPython] G4_Fr  # scripted group (container) (typed FeaturePython)
  Dunit = g/cm3
  Dvalue = 1
  Group = -> [Fr_element001]
  conduct = 2
  density = 1
  expand = 3
  formula = Fr
  name = G4_Fr
  specific = 4
FEATURE [App::DocumentObjectGroupPython] Ra_element001  label="Ra_element : 1"  # scripted group (container) (typed FeaturePython)
  n = 1
  ref = Ra_element
FEATURE [App::DocumentObjectGroupPython] G4_Ra  # scripted group (container) (typed FeaturePython)
  Dunit = g/cm3
  Dvalue = 5
  Group = -> [Ra_element001]
  conduct = 2
  density = 1
  expand = 3
  formula = Ra
  name = G4_Ra
  specific = 4
FEATURE [App::DocumentObjectGroupPython] Ac_element001  label="Ac_element : 1"  # scripted group (container) (typed FeaturePython)
  n = 1
  ref = Ac_element
FEATURE [App::DocumentObjectGroupPython] G4_Ac  # scripted group (container) (typed FeaturePython)
  Dunit = g/cm3
  Dvalue = 10.07
  Group = -> [Ac_element001]
  conduct = 2
  density = 1
  expand = 3
  formula = Ac
  name = G4_Ac
  specific = 4
FEATURE [App::DocumentObjectGroupPython] Th_element001  label="Th_element : 1"  # scripted group (container) (typed FeaturePython)
  n = 1
  ref = Th_element
FEATURE [App::DocumentObjectGroupPython] G4_Th  # scripted group (container) (typed FeaturePython)
  Dunit = g/cm3
  Dvalue = 11.72
  Group = -> [Th_element001]
  conduct = 2
  density = 1
  expand = 3
  formula = Th
  name = G4_Th
  specific = 4
FEATURE [App::DocumentObjectGroupPython] Pa_element001  label="Pa_element : 1"  # scripted group (container) (typed FeaturePython)
  n = 1
  ref = Pa_element
FEATURE [App::DocumentObjectGroupPython] G4_Pa  # scripted group (container) (typed FeaturePython)
  Dunit = g/cm3
  Dvalue = 15.37
  Group = -> [Pa_element001]
  conduct = 2
  density = 1
  expand = 3
  formula = Pa
  name = G4_Pa
  specific = 4
FEATURE [App::DocumentObjectGroupPython] U_element004  label="U_element : 004"  # scripted group (container) (typed FeaturePython)
  n = 1
  ref = U_element
FEATURE [App::DocumentObjectGroupPython] G4_U  # scripted group (container) (typed FeaturePython)
  Dunit = g/cm3
  Dvalue = 18.95
  Group = -> [U_element004]
  conduct = 2
  density = 1
  expand = 3
  formula = U
  name = G4_U
  specific = 4
FEATURE [App::DocumentObjectGroupPython] Np_element001  label="Np_element : 1"  # scripted group (container) (typed FeaturePython)
  n = 1
  ref = Np_element
FEATURE [App::DocumentObjectGroupPython] G4_Np  # scripted group (container) (typed FeaturePython)
  Dunit = g/cm3
  Dvalue = 20.25
  Group = -> [Np_element001]
  conduct = 2
  density = 1
  expand = 3
  formula = Np
  name = G4_Np
  specific = 4
FEATURE [App::DocumentObjectGroupPython] Pu_element002  label="Pu_element : 002"  # scripted group (container) (typed FeaturePython)
  n = 1
  ref = Pu_element
FEATURE [App::DocumentObjectGroupPython] G4_Pu  # scripted group (container) (typed FeaturePython)
  Dunit = g/cm3
  Dvalue = 19.84
  Group = -> [Pu_element002]
  conduct = 2
  density = 1
  expand = 3
  formula = Pu
  name = G4_Pu
  specific = 4
FEATURE [App::DocumentObjectGroupPython] Am_element001  label="Am_element : 1"  # scripted group (container) (typed FeaturePython)
  n = 1
  ref = Am_element
FEATURE [App::DocumentObjectGroupPython] G4_Am  # scripted group (container) (typed FeaturePython)
  Dunit = g/cm3
  Dvalue = 13.67
  Group = -> [Am_element001]
  conduct = 2
  density = 1
  expand = 3
  formula = Am
  name = G4_Am
  specific = 4
FEATURE [App::DocumentObjectGroupPython] Cm_element001  label="Cm_element : 1"  # scripted group (container) (typed FeaturePython)
  n = 1
  ref = Cm_element
FEATURE [App::DocumentObjectGroupPython] G4_Cm  # scripted group (container) (typed FeaturePython)
  Dunit = g/cm3
  Dvalue = 13.51
  Group = -> [Cm_element001]
  conduct = 2
  density = 1
  expand = 3
  formula = Cm
  name = G4_Cm
  specific = 4
FEATURE [App::DocumentObjectGroupPython] Bk_element001  label="Bk_element : 1"  # scripted group (container) (typed FeaturePython)
  n = 1
  ref = Bk_element
FEATURE [App::DocumentObjectGroupPython] G4_Bk  # scripted group (container) (typed FeaturePython)
  Dunit = g/cm3
  Dvalue = 14
  Group = -> [Bk_element001]
  conduct = 2
  density = 1
  expand = 3
  formula = Bk
  name = G4_Bk
  specific = 4
FEATURE [App::DocumentObjectGroupPython] Cf_element001  label="Cf_element : 1"  # scripted group (container) (typed FeaturePython)
  n = 1
  ref = Cf_element
FEATURE [App::DocumentObjectGroupPython] G4_Cf  # scripted group (container) (typed FeaturePython)
  Dunit = g/cm3
  Dvalue = 10
  Group = -> [Cf_element001]
  conduct = 2
  density = 1
  expand = 3
  formula = Cf
  name = G4_Cf
  specific = 4
FEATURE [App::DocumentObjectGroupPython] Element  # scripted group (container) (typed FeaturePython)
  Group = -> [G4_H,G4_He,G4_Li,G4_Be,G4_B,G4_C,G4_N,G4_O,G4_F,G4_Ne,G4_Na,G4_Mg,G4_Al,G4_Si,G4_P,G4_S,G4_Cl,G4_Ar,G4_K,G4_Ca,G4_Sc,G4_Ti,G4_V,G4_Cr,G4_Mn,G4_Fe,G4_Co,G4_Ni,G4_Cu,G4_Zn,G4_Ga,G4_Ge,G4_As,G4_Se,G4_Br,G4_Kr,G4_Rb,G4_Sr,G4_Y,G4_Zr,G4_Nb,G4_Mo,G4_Tc,G4_Ru,G4_Rh,G4_Pd,G4_Ag,G4_Cd,G4_In,G4_Sn,G4_Sb,G4_Te,G4_I,G4_Xe,G4_Cs,G4_Ba,G4_La,G4_Ce,G4_Pr,G4_Nd,G4_Pm,G4_Sm,G4_Eu,G4_Gd,G4_Tb,G4_Dy,G4_Ho,G4_Er,+30 more]
FEATURE [App::DocumentObjectGroupPython] H_element114  label="H_element : 063"  # scripted group (container) (typed FeaturePython)
  n = 2
  ref = H_element
FEATURE [App::DocumentObjectGroupPython] G4_lH2  # scripted group (container) (typed FeaturePython)
  Dunit = g/cm3
  Dvalue = 0.0708
  Group = -> [H_element114]
  conduct = 2
  density = 1
  expand = 3
  formula = G4_lH2
  name = G4_lH2
  specific = 4
FEATURE [App::DocumentObjectGroupPython] N_element049  label="N_element : 022"  # scripted group (container) (typed FeaturePython)
  n = 2
  ref = N_element
FEATURE [App::DocumentObjectGroupPython] G4_lN2  # scripted group (container) (typed FeaturePython)
  Dunit = g/cm3
  Dvalue = 0.807
  Group = -> [N_element049]
  conduct = 2
  density = 1
  expand = 3
  formula = G4_lN2
  name = G4_lN2
  specific = 4
FEATURE [App::DocumentObjectGroupPython] O_element106  label="O_element : 060"  # scripted group (container) (typed FeaturePython)
  n = 2
  ref = O_element
FEATURE [App::DocumentObjectGroupPython] G4_lO2  # scripted group (container) (typed FeaturePython)
  Dunit = g/cm3
  Dvalue = 1.141
  Group = -> [O_element106]
  conduct = 2
  density = 1
  expand = 3
  formula = G4_lO2
  name = G4_lO2
  specific = 4
FEATURE [App::DocumentObjectGroupPython] Ar  label="Ar : 1"  # scripted group (container) (typed FeaturePython)
  n = 1
  ref = Ar
FEATURE [App::DocumentObjectGroupPython] G4_lAr  # scripted group (container) (typed FeaturePython)
  Dunit = g/cm3
  Dvalue = 1.396
  Group = -> [Ar]
  conduct = 2
  density = 1
  expand = 3
  formula = G4_lAr
  name = G4_lAr
  specific = 4
FEATURE [App::DocumentObjectGroupPython] Br  label="Br : 1"  # scripted group (container) (typed FeaturePython)
  n = 1
  ref = Br
FEATURE [App::DocumentObjectGroupPython] G4_lBr  # scripted group (container) (typed FeaturePython)
  Dunit = g/cm3
  Dvalue = 3.1028
  Group = -> [Br]
  conduct = 2
  density = 1
  expand = 3
  formula = G4_lBr
  name = G4_lBr
  specific = 4
FEATURE [App::DocumentObjectGroupPython] Kr  label="Kr : 1"  # scripted group (container) (typed FeaturePython)
  n = 1
  ref = Kr
FEATURE [App::DocumentObjectGroupPython] G4_lKr  # scripted group (container) (typed FeaturePython)
  Dunit = g/cm3
  Dvalue = 2.418
  Group = -> [Kr]
  conduct = 2
  density = 1
  expand = 3
  formula = G4_lKr
  name = G4_lKr
  specific = 4
FEATURE [App::DocumentObjectGroupPython] Xe  label="Xe : 1"  # scripted group (container) (typed FeaturePython)
  n = 1
  ref = Xe
FEATURE [App::DocumentObjectGroupPython] G4_lXe  # scripted group (container) (typed FeaturePython)
  Dunit = g/cm3
  Dvalue = 2.953
  Group = -> [Xe]
  conduct = 2
  density = 1
  expand = 3
  formula = G4_lXe
  name = G4_lXe
  specific = 4
FEATURE [App::DocumentObjectGroupPython] O_element107  label="O_element : 061"  # scripted group (container) (typed FeaturePython)
  n = 4
  ref = O_element
FEATURE [App::DocumentObjectGroupPython] Pb_element004  label="Pb_element : 002"  # scripted group (container) (typed FeaturePython)
  n = 1
  ref = Pb_element
FEATURE [App::DocumentObjectGroupPython] W_element005  label="W_element : 005"  # scripted group (container) (typed FeaturePython)
  n = 1
  ref = W_element
FEATURE [App::DocumentObjectGroupPython] G4_PbWO4  # scripted group (container) (typed FeaturePython)
  Dunit = g/cm3
  Dvalue = 8.28
  Group = -> [O_element107,Pb_element004,W_element005]
  conduct = 2
  density = 1
  expand = 3
  formula = G4_PbWO4
  name = G4_PbWO4
  specific = 4
FEATURE [App::DocumentObjectGroupPython] alactic  label="alactic : 1"  # scripted group (container) (typed FeaturePython)
  n = 1
  ref = alactic
FEATURE [App::DocumentObjectGroupPython] G4_Galactic  # scripted group (container) (typed FeaturePython)
  Dunit = g/cm3
  Dvalue = 0
  Group = -> [alactic]
  conduct = 2
  density = 1
  expand = 3
  formula = G4_Galactic
  name = G4_Galactic
  specific = 4
FEATURE [App::DocumentObjectGroupPython] RAPHITE_POROUS  label="RAPHITE_POROUS : 1"  # scripted group (container) (typed FeaturePython)
  n = 1
  ref = RAPHITE_POROUS
FEATURE [App::DocumentObjectGroupPython] G4_GRAPHITE_POROUS  # scripted group (container) (typed FeaturePython)
  Dunit = g/cm3
  Dvalue = 1.7
  Group = -> [RAPHITE_POROUS]
  conduct = 2
  density = 1
  expand = 3
  formula = G4_GRAPHITE_POROUS
  name = G4_GRAPHITE_POROUS
  specific = 4
FEATURE [App::DocumentObjectGroupPython] H_element115  label="H_element : 0.150"  # scripted group (container) (typed FeaturePython)
  n = 0.080538
FEATURE [App::DocumentObjectGroupPython] C_element125  label="C_element : 0.600"  # scripted group (container) (typed FeaturePython)
  n = 0.599848
FEATURE [App::DocumentObjectGroupPython] O_element108  label="O_element : 0.320"  # scripted group (container) (typed FeaturePython)
  n = 0.319614
FEATURE [App::DocumentObjectGroupPython] G4_LUCITE  # scripted group (container) (typed FeaturePython)
  Dunit = g/cm3
  Dvalue = 1.19
  Group = -> [H_element115,C_element125,O_element108]
  conduct = 2
  density = 1
  expand = 3
  formula = G4_LUCITE
  name = G4_LUCITE
  specific = 4
FEATURE [App::DocumentObjectGroupPython] Cu_element002  label="Cu_element : 62"  # scripted group (container) (typed FeaturePython)
  n = 62
  ref = Cu_element
FEATURE [App::DocumentObjectGroupPython] Zn_element002  label="Zn_element : 35"  # scripted group (container) (typed FeaturePython)
  n = 35
  ref = Zn_element
FEATURE [App::DocumentObjectGroupPython] Pb_element005  label="Pb_element : 3"  # scripted group (container) (typed FeaturePython)
  n = 3
  ref = Pb_element
FEATURE [App::DocumentObjectGroupPython] G4_BRASS  # scripted group (container) (typed FeaturePython)
  Dunit = g/cm3
  Dvalue = 8.52
  Group = -> [Cu_element002,Zn_element002,Pb_element005]
  conduct = 2
  density = 1
  expand = 3
  formula = G4_BRASS
  name = G4_BRASS
  specific = 4
FEATURE [App::DocumentObjectGroupPython] Cu_element003  label="Cu_element : 89"  # scripted group (container) (typed FeaturePython)
  n = 89
  ref = Cu_element
FEATURE [App::DocumentObjectGroupPython] Zn_element003  label="Zn_element : 9"  # scripted group (container) (typed FeaturePython)
  n = 9
  ref = Zn_element
FEATURE [App::DocumentObjectGroupPython] Pb_element006  label="Pb_element : 2"  # scripted group (container) (typed FeaturePython)
  n = 2
  ref = Pb_element
FEATURE [App::DocumentObjectGroupPython] G4_BRONZE  # scripted group (container) (typed FeaturePython)
  Dunit = g/cm3
  Dvalue = 8.82
  Group = -> [Cu_element003,Zn_element003,Pb_element006]
  conduct = 2
  density = 1
  expand = 3
  formula = G4_BRONZE
  name = G4_BRONZE
  specific = 4
FEATURE [App::DocumentObjectGroupPython] Fe_element008  label="Fe_element : 74"  # scripted group (container) (typed FeaturePython)
  n = 74
  ref = Fe_element
FEATURE [App::DocumentObjectGroupPython] Cr_element002  label="Cr_element : 18"  # scripted group (container) (typed FeaturePython)
  n = 18
  ref = Cr_element
FEATURE [App::DocumentObjectGroupPython] Ni_element002  label="Ni_element : 8"  # scripted group (container) (typed FeaturePython)
  n = 8
  ref = Ni_element
FEATURE [App::DocumentObjectGroupPython] G4_STAINLESS_STEEL  label="G4_STAINLESS-STEEL"  # scripted group (container) (typed FeaturePython)
  Dunit = g/cm3
  Dvalue = 8
  Group = -> [Fe_element008,Cr_element002,Ni_element002]
  conduct = 2
  density = 1
  expand = 3
  formula = G4_STAINLESS-STEEL
  name = G4_STAINLESS-STEEL
  specific = 4
FEATURE [App::DocumentObjectGroupPython] H_element116  label="H_element : 064"  # scripted group (container) (typed FeaturePython)
  n = 18
  ref = H_element
FEATURE [App::DocumentObjectGroupPython] C_element126  label="C_element : 071"  # scripted group (container) (typed FeaturePython)
  n = 12
  ref = C_element
FEATURE [App::DocumentObjectGroupPython] O_element109  label="O_element : 062"  # scripted group (container) (typed FeaturePython)
  n = 7
  ref = O_element
FEATURE [App::DocumentObjectGroupPython] G4_CR39  # scripted group (container) (typed FeaturePython)
  Dunit = g/cm3
  Dvalue = 1.32
  Group = -> [H_element116,C_element126,O_element109]
  conduct = 2
  density = 1
  expand = 3
  formula = G4_CR39
  name = G4_CR39
  specific = 4
FEATURE [App::DocumentObjectGroupPython] H_element117  label="H_element : 38"  # scripted group (container) (typed FeaturePython)
  n = 38
  ref = H_element
FEATURE [App::DocumentObjectGroupPython] C_element127  label="C_element : 072"  # scripted group (container) (typed FeaturePython)
  n = 18
  ref = C_element
FEATURE [App::DocumentObjectGroupPython] O_element110  label="O_element : 063"  # scripted group (container) (typed FeaturePython)
  n = 1
  ref = O_element
FEATURE [App::DocumentObjectGroupPython] G4_OCTADECANOL  # scripted group (container) (typed FeaturePython)
  Dunit = g/cm3
  Dvalue = 0.812
  Group = -> [H_element117,C_element127,O_element110]
  conduct = 2
  density = 1
  expand = 3
  formula = G4_OCTADECANOL
  name = G4_OCTADECANOL
  specific = 4
FEATURE [App::DocumentObjectGroupPython] HEP  # scripted group (container) (typed FeaturePython)
  Group = -> [G4_lH2,G4_lN2,G4_lO2,G4_lAr,G4_lBr,G4_lKr,G4_lXe,G4_PbWO4,G4_Galactic,G4_GRAPHITE_POROUS,G4_LUCITE,G4_BRASS,G4_BRONZE,G4_STAINLESS_STEEL,G4_CR39,G4_OCTADECANOL]
FEATURE [App::DocumentObjectGroupPython] C_element128  label="C_element : 073"  # scripted group (container) (typed FeaturePython)
  n = 14
  ref = C_element
FEATURE [App::DocumentObjectGroupPython] H_element118  label="H_element : 065"  # scripted group (container) (typed FeaturePython)
  n = 10
  ref = H_element
FEATURE [App::DocumentObjectGroupPython] O_element111  label="O_element : 064"  # scripted group (container) (typed FeaturePython)
  n = 2
  ref = O_element
FEATURE [App::DocumentObjectGroupPython] N_element050  label="N_element : 023"  # scripted group (container) (typed FeaturePython)
  n = 2
  ref = N_element
FEATURE [App::DocumentObjectGroupPython] G4_KEVLAR  # scripted group (container) (typed FeaturePython)
  Dunit = g/cm3
  Dvalue = 1.44
  Group = -> [C_element128,H_element118,O_element111,N_element050]
  conduct = 2
  density = 1
  expand = 3
  formula = G4_KEVLAR
  name = G4_KEVLAR
  specific = 4
FEATURE [App::DocumentObjectGroupPython] C_element129  label="C_element : 074"  # scripted group (container) (typed FeaturePython)
  n = 10
  ref = C_element
FEATURE [App::DocumentObjectGroupPython] H_element119  label="H_element : 066"  # scripted group (container) (typed FeaturePython)
  n = 8
  ref = H_element
FEATURE [App::DocumentObjectGroupPython] O_element112  label="O_element : 065"  # scripted group (container) (typed FeaturePython)
  n = 4
  ref = O_element
FEATURE [App::DocumentObjectGroupPython] G4_DACRON  # scripted group (container) (typed FeaturePython)
  Dunit = g/cm3
  Dvalue = 1.4
  Group = -> [C_element129,H_element119,O_element112]
  conduct = 2
  density = 1
  expand = 3
  formula = G4_DACRON
  name = G4_DACRON
  specific = 4
FEATURE [App::DocumentObjectGroupPython] C_element130  label="C_element : 075"  # scripted group (container) (typed FeaturePython)
  n = 4
  ref = C_element
FEATURE [App::DocumentObjectGroupPython] H_element120  label="H_element : 067"  # scripted group (container) (typed FeaturePython)
  n = 5
  ref = H_element
FEATURE [App::DocumentObjectGroupPython] Cl_element030  label="Cl_element : 016"  # scripted group (container) (typed FeaturePython)
  n = 1
  ref = Cl_element
FEATURE [App::DocumentObjectGroupPython] G4_NEOPRENE  # scripted group (container) (typed FeaturePython)
  Dunit = g/cm3
  Dvalue = 1.23
  Group = -> [C_element130,H_element120,Cl_element030]
  conduct = 2
  density = 1
  expand = 3
  formula = G4_NEOPRENE
  name = G4_NEOPRENE
  specific = 4
FEATURE [App::DocumentObjectGroupPython] Space  # scripted group (container) (typed FeaturePython)
  Group = -> [G4_KEVLAR,G4_DACRON,G4_NEOPRENE]
FEATURE [App::DocumentObjectGroupPython] H_element121  label="H_element : 068"  # scripted group (container) (typed FeaturePython)
  n = 5
  ref = H_element
FEATURE [App::DocumentObjectGroupPython] C_element131  label="C_element : 076"  # scripted group (container) (typed FeaturePython)
  n = 4
  ref = C_element
FEATURE [App::DocumentObjectGroupPython] N_element051  label="N_element : 3"  # scripted group (container) (typed FeaturePython)
  n = 3
  ref = N_element
FEATURE [App::DocumentObjectGroupPython] O_element113  label="O_element : 066"  # scripted group (container) (typed FeaturePython)
  n = 1
  ref = O_element
FEATURE [App::DocumentObjectGroupPython] G4_CYTOSINE  # scripted group (container) (typed FeaturePython)
  Dunit = g/cm3
  Dvalue = 1.55
  Group = -> [H_element121,C_element131,N_element051,O_element113]
  conduct = 2
  density = 1
  expand = 3
  formula = G4_CYTOSINE
  name = G4_CYTOSINE
  specific = 4
FEATURE [App::DocumentObjectGroupPython] H_element122  label="H_element : 069"  # scripted group (container) (typed FeaturePython)
  n = 6
  ref = H_element
FEATURE [App::DocumentObjectGroupPython] C_element132  label="C_element : 077"  # scripted group (container) (typed FeaturePython)
  n = 5
  ref = C_element
FEATURE [App::DocumentObjectGroupPython] N_element052  label="N_element : 024"  # scripted group (container) (typed FeaturePython)
  n = 2
  ref = N_element
FEATURE [App::DocumentObjectGroupPython] O_element114  label="O_element : 067"  # scripted group (container) (typed FeaturePython)
  n = 2
  ref = O_element
FEATURE [App::DocumentObjectGroupPython] G4_THYMINE  # scripted group (container) (typed FeaturePython)
  Dunit = g/cm3
  Dvalue = 1.23
  Group = -> [H_element122,C_element132,N_element052,O_element114]
  conduct = 2
  density = 1
  expand = 3
  formula = G4_THYMINE
  name = G4_THYMINE
  specific = 4
FEATURE [App::DocumentObjectGroupPython] H_element123  label="H_element : 070"  # scripted group (container) (typed FeaturePython)
  n = 4
  ref = H_element
FEATURE [App::DocumentObjectGroupPython] C_element133  label="C_element : 078"  # scripted group (container) (typed FeaturePython)
  n = 4
  ref = C_element
FEATURE [App::DocumentObjectGroupPython] N_element053  label="N_element : 025"  # scripted group (container) (typed FeaturePython)
  n = 2
  ref = N_element
FEATURE [App::DocumentObjectGroupPython] O_element115  label="O_element : 068"  # scripted group (container) (typed FeaturePython)
  n = 2
  ref = O_element
FEATURE [App::DocumentObjectGroupPython] G4_URACIL  # scripted group (container) (typed FeaturePython)
  Dunit = g/cm3
  Dvalue = 1.32
  Group = -> [H_element123,C_element133,N_element053,O_element115]
  conduct = 2
  density = 1
  expand = 3
  formula = G4_URACIL
  name = G4_URACIL
  specific = 4
FEATURE [App::DocumentObjectGroupPython] H_element124  label="H_element : 071"  # scripted group (container) (typed FeaturePython)
  n = 4
  ref = H_element
FEATURE [App::DocumentObjectGroupPython] C_element134  label="C_element : 079"  # scripted group (container) (typed FeaturePython)
  n = 5
  ref = C_element
FEATURE [App::DocumentObjectGroupPython] N_element054  label="N_element : 026"  # scripted group (container) (typed FeaturePython)
  n = 5
  ref = N_element
FEATURE [App::DocumentObjectGroupPython] G4_DNA_ADENINE  # scripted group (container) (typed FeaturePython)
  Dunit = g/cm3
  Dvalue = 1
  Group = -> [H_element124,C_element134,N_element054]
  conduct = 2
  density = 1
  expand = 3
  formula = G4_DNA_ADENINE
  name = G4_DNA_ADENINE
  specific = 4
FEATURE [App::DocumentObjectGroupPython] H_element125  label="H_element : 072"  # scripted group (container) (typed FeaturePython)
  n = 4
  ref = H_element
FEATURE [App::DocumentObjectGroupPython] C_element135  label="C_element : 080"  # scripted group (container) (typed FeaturePython)
  n = 5
  ref = C_element
FEATURE [App::DocumentObjectGroupPython] N_element055  label="N_element : 027"  # scripted group (container) (typed FeaturePython)
  n = 5
  ref = N_element
FEATURE [App::DocumentObjectGroupPython] O_element116  label="O_element : 069"  # scripted group (container) (typed FeaturePython)
  n = 1
  ref = O_element
FEATURE [App::DocumentObjectGroupPython] G4_DNA_GUANINE  # scripted group (container) (typed FeaturePython)
  Dunit = g/cm3
  Dvalue = 1
  Group = -> [H_element125,C_element135,N_element055,O_element116]
  conduct = 2
  density = 1
  expand = 3
  formula = G4_DNA_GUANINE
  name = G4_DNA_GUANINE
  specific = 4
FEATURE [App::DocumentObjectGroupPython] H_element126  label="H_element : 073"  # scripted group (container) (typed FeaturePython)
  n = 4
  ref = H_element
FEATURE [App::DocumentObjectGroupPython] C_element136  label="C_element : 081"  # scripted group (container) (typed FeaturePython)
  n = 4
  ref = C_element
FEATURE [App::DocumentObjectGroupPython] N_element056  label="N_element : 028"  # scripted group (container) (typed FeaturePython)
  n = 3
  ref = N_element
FEATURE [App::DocumentObjectGroupPython] O_element117  label="O_element : 070"  # scripted group (container) (typed FeaturePython)
  n = 1
  ref = O_element
FEATURE [App::DocumentObjectGroupPython] G4_DNA_CYTOSINE  # scripted group (container) (typed FeaturePython)
  Dunit = g/cm3
  Dvalue = 1
  Group = -> [H_element126,C_element136,N_element056,O_element117]
  conduct = 2
  density = 1
  expand = 3
  formula = G4_DNA_CYTOSINE
  name = G4_DNA_CYTOSINE
  specific = 4
FEATURE [App::DocumentObjectGroupPython] H_element127  label="H_element : 074"  # scripted group (container) (typed FeaturePython)
  n = 5
  ref = H_element
FEATURE [App::DocumentObjectGroupPython] C_element137  label="C_element : 082"  # scripted group (container) (typed FeaturePython)
  n = 5
  ref = C_element
FEATURE [App::DocumentObjectGroupPython] N_element057  label="N_element : 029"  # scripted group (container) (typed FeaturePython)
  n = 2
  ref = N_element
FEATURE [App::DocumentObjectGroupPython] O_element118  label="O_element : 071"  # scripted group (container) (typed FeaturePython)
  n = 2
  ref = O_element
FEATURE [App::DocumentObjectGroupPython] G4_DNA_THYMINE  # scripted group (container) (typed FeaturePython)
  Dunit = g/cm3
  Dvalue = 1
  Group = -> [H_element127,C_element137,N_element057,O_element118]
  conduct = 2
  density = 1
  expand = 3
  formula = G4_DNA_THYMINE
  name = G4_DNA_THYMINE
  specific = 4
FEATURE [App::DocumentObjectGroupPython] H_element128  label="H_element : 075"  # scripted group (container) (typed FeaturePython)
  n = 3
  ref = H_element
FEATURE [App::DocumentObjectGroupPython] C_element138  label="C_element : 083"  # scripted group (container) (typed FeaturePython)
  n = 4
  ref = C_element
FEATURE [App::DocumentObjectGroupPython] N_element058  label="N_element : 030"  # scripted group (container) (typed FeaturePython)
  n = 2
  ref = N_element
FEATURE [App::DocumentObjectGroupPython] O_element119  label="O_element : 072"  # scripted group (container) (typed FeaturePython)
  n = 2
  ref = O_element
FEATURE [App::DocumentObjectGroupPython] G4_DNA_URACIL  # scripted group (container) (typed FeaturePython)
  Dunit = g/cm3
  Dvalue = 1
  Group = -> [H_element128,C_element138,N_element058,O_element119]
  conduct = 2
  density = 1
  expand = 3
  formula = G4_DNA_URACIL
  name = G4_DNA_URACIL
  specific = 4
FEATURE [App::DocumentObjectGroupPython] H_element129  label="H_element : 076"  # scripted group (container) (typed FeaturePython)
  n = 10
  ref = H_element
FEATURE [App::DocumentObjectGroupPython] C_element139  label="C_element : 084"  # scripted group (container) (typed FeaturePython)
  n = 10
  ref = C_element
FEATURE [App::DocumentObjectGroupPython] N_element059  label="N_element : 031"  # scripted group (container) (typed FeaturePython)
  n = 5
  ref = N_element
FEATURE [App::DocumentObjectGroupPython] O_element120  label="O_element : 073"  # scripted group (container) (typed FeaturePython)
  n = 4
  ref = O_element
FEATURE [App::DocumentObjectGroupPython] G4_DNA_ADENOSINE  # scripted group (container) (typed FeaturePython)
  Dunit = g/cm3
  Dvalue = 1
  Group = -> [H_element129,C_element139,N_element059,O_element120]
  conduct = 2
  density = 1
  expand = 3
  formula = G4_DNA_ADENOSINE
  name = G4_DNA_ADENOSINE
  specific = 4
FEATURE [App::DocumentObjectGroupPython] H_element130  label="H_element : 077"  # scripted group (container) (typed FeaturePython)
  n = 10
  ref = H_element
FEATURE [App::DocumentObjectGroupPython] C_element140  label="C_element : 085"  # scripted group (container) (typed FeaturePython)
  n = 10
  ref = C_element
FEATURE [App::DocumentObjectGroupPython] N_element060  label="N_element : 032"  # scripted group (container) (typed FeaturePython)
  n = 5
  ref = N_element
FEATURE [App::DocumentObjectGroupPython] O_element121  label="O_element : 074"  # scripted group (container) (typed FeaturePython)
  n = 5
  ref = O_element
FEATURE [App::DocumentObjectGroupPython] G4_DNA_GUANOSINE  # scripted group (container) (typed FeaturePython)
  Dunit = g/cm3
  Dvalue = 1
  Group = -> [H_element130,C_element140,N_element060,O_element121]
  conduct = 2
  density = 1
  expand = 3
  formula = G4_DNA_GUANOSINE
  name = G4_DNA_GUANOSINE
  specific = 4
FEATURE [App::DocumentObjectGroupPython] H_element131  label="H_element : 078"  # scripted group (container) (typed FeaturePython)
  n = 10
  ref = H_element
FEATURE [App::DocumentObjectGroupPython] C_element141  label="C_element : 086"  # scripted group (container) (typed FeaturePython)
  n = 9
  ref = C_element
FEATURE [App::DocumentObjectGroupPython] N_element061  label="N_element : 033"  # scripted group (container) (typed FeaturePython)
  n = 3
  ref = N_element
FEATURE [App::DocumentObjectGroupPython] O_element122  label="O_element : 075"  # scripted group (container) (typed FeaturePython)
  n = 5
  ref = O_element
FEATURE [App::DocumentObjectGroupPython] G4_DNA_CYTIDINE  # scripted group (container) (typed FeaturePython)
  Dunit = g/cm3
  Dvalue = 1
  Group = -> [H_element131,C_element141,N_element061,O_element122]
  conduct = 2
  density = 1
  expand = 3
  formula = G4_DNA_CYTIDINE
  name = G4_DNA_CYTIDINE
  specific = 4
FEATURE [App::DocumentObjectGroupPython] H_element132  label="H_element : 079"  # scripted group (container) (typed FeaturePython)
  n = 9
  ref = H_element
FEATURE [App::DocumentObjectGroupPython] C_element142  label="C_element : 087"  # scripted group (container) (typed FeaturePython)
  n = 9
  ref = C_element
FEATURE [App::DocumentObjectGroupPython] N_element062  label="N_element : 034"  # scripted group (container) (typed FeaturePython)
  n = 2
  ref = N_element
FEATURE [App::DocumentObjectGroupPython] O_element123  label="O_element : 076"  # scripted group (container) (typed FeaturePython)
  n = 6
  ref = O_element
FEATURE [App::DocumentObjectGroupPython] G4_DNA_URIDINE  # scripted group (container) (typed FeaturePython)
  Dunit = g/cm3
  Dvalue = 1
  Group = -> [H_element132,C_element142,N_element062,O_element123]
  conduct = 2
  density = 1
  expand = 3
  formula = G4_DNA_URIDINE
  name = G4_DNA_URIDINE
  specific = 4
FEATURE [App::DocumentObjectGroupPython] H_element133  label="H_element : 080"  # scripted group (container) (typed FeaturePython)
  n = 11
  ref = H_element
FEATURE [App::DocumentObjectGroupPython] C_element143  label="C_element : 088"  # scripted group (container) (typed FeaturePython)
  n = 10
  ref = C_element
FEATURE [App::DocumentObjectGroupPython] N_element063  label="N_element : 035"  # scripted group (container) (typed FeaturePython)
  n = 2
  ref = N_element
FEATURE [App::DocumentObjectGroupPython] O_element124  label="O_element : 077"  # scripted group (container) (typed FeaturePython)
  n = 6
  ref = O_element
FEATURE [App::DocumentObjectGroupPython] G4_DNA_METHYLURIDINE  # scripted group (container) (typed FeaturePython)
  Dunit = g/cm3
  Dvalue = 1
  Group = -> [H_element133,C_element143,N_element063,O_element124]
  conduct = 2
  density = 1
  expand = 3
  formula = G4_DNA_METHYLURIDINE
  name = G4_DNA_METHYLURIDINE
  specific = 4
FEATURE [App::DocumentObjectGroupPython] P_element014  label="P_element : 003"  # scripted group (container) (typed FeaturePython)
  n = 1
  ref = P_element
FEATURE [App::DocumentObjectGroupPython] O_element125  label="O_element : 078"  # scripted group (container) (typed FeaturePython)
  n = 3
  ref = O_element
FEATURE [App::DocumentObjectGroupPython] G4_DNA_MONOPHOSPHATE  # scripted group (container) (typed FeaturePython)
  Dunit = g/cm3
  Dvalue = 1
  Group = -> [P_element014,O_element125]
  conduct = 2
  density = 1
  expand = 3
  formula = G4_DNA_MONOPHOSPHATE
  name = G4_DNA_MONOPHOSPHATE
  specific = 4
FEATURE [App::DocumentObjectGroupPython] H_element134  label="H_element : 081"  # scripted group (container) (typed FeaturePython)
  n = 10
  ref = H_element
FEATURE [App::DocumentObjectGroupPython] C_element144  label="C_element : 089"  # scripted group (container) (typed FeaturePython)
  n = 10
  ref = C_element
FEATURE [App::DocumentObjectGroupPython] N_element064  label="N_element : 036"  # scripted group (container) (typed FeaturePython)
  n = 5
  ref = N_element
FEATURE [App::DocumentObjectGroupPython] O_element126  label="O_element : 079"  # scripted group (container) (typed FeaturePython)
  n = 7
  ref = O_element
FEATURE [App::DocumentObjectGroupPython] P_element015  label="P_element : 004"  # scripted group (container) (typed FeaturePython)
  n = 1
  ref = P_element
FEATURE [App::DocumentObjectGroupPython] G4_DNA_A  # scripted group (container) (typed FeaturePython)
  Dunit = g/cm3
  Dvalue = 1
  Group = -> [H_element134,C_element144,N_element064,O_element126,P_element015]
  conduct = 2
  density = 1
  expand = 3
  formula = G4_DNA_A
  name = G4_DNA_A
  specific = 4
FEATURE [App::DocumentObjectGroupPython] H_element135  label="H_element : 082"  # scripted group (container) (typed FeaturePython)
  n = 10
  ref = H_element
FEATURE [App::DocumentObjectGroupPython] C_element145  label="C_element : 090"  # scripted group (container) (typed FeaturePython)
  n = 10
  ref = C_element
FEATURE [App::DocumentObjectGroupPython] N_element065  label="N_element : 037"  # scripted group (container) (typed FeaturePython)
  n = 5
  ref = N_element
FEATURE [App::DocumentObjectGroupPython] O_element127  label="O_element : 8"  # scripted group (container) (typed FeaturePython)
  n = 8
  ref = O_element
FEATURE [App::DocumentObjectGroupPython] P_element016  label="P_element : 005"  # scripted group (container) (typed FeaturePython)
  n = 1
  ref = P_element
FEATURE [App::DocumentObjectGroupPython] G4_DNA_G  # scripted group (container) (typed FeaturePython)
  Dunit = g/cm3
  Dvalue = 1
  Group = -> [H_element135,C_element145,N_element065,O_element127,P_element016]
  conduct = 2
  density = 1
  expand = 3
  formula = G4_DNA_G
  name = G4_DNA_G
  specific = 4
FEATURE [App::DocumentObjectGroupPython] H_element136  label="H_element : 083"  # scripted group (container) (typed FeaturePython)
  n = 10
  ref = H_element
FEATURE [App::DocumentObjectGroupPython] C_element146  label="C_element : 091"  # scripted group (container) (typed FeaturePython)
  n = 9
  ref = C_element
FEATURE [App::DocumentObjectGroupPython] N_element066  label="N_element : 038"  # scripted group (container) (typed FeaturePython)
  n = 3
  ref = N_element
FEATURE [App::DocumentObjectGroupPython] O_element128  label="O_element : 080"  # scripted group (container) (typed FeaturePython)
  n = 8
  ref = O_element
FEATURE [App::DocumentObjectGroupPython] P_element017  label="P_element : 006"  # scripted group (container) (typed FeaturePython)
  n = 1
  ref = P_element
FEATURE [App::DocumentObjectGroupPython] G4_DNA_C  # scripted group (container) (typed FeaturePython)
  Dunit = g/cm3
  Dvalue = 1
  Group = -> [H_element136,C_element146,N_element066,O_element128,P_element017]
  conduct = 2
  density = 1
  expand = 3
  formula = G4_DNA_C
  name = G4_DNA_C
  specific = 4
FEATURE [App::DocumentObjectGroupPython] H_element137  label="H_element : 084"  # scripted group (container) (typed FeaturePython)
  n = 9
  ref = H_element
FEATURE [App::DocumentObjectGroupPython] C_element147  label="C_element : 092"  # scripted group (container) (typed FeaturePython)
  n = 9
  ref = C_element
FEATURE [App::DocumentObjectGroupPython] N_element067  label="N_element : 039"  # scripted group (container) (typed FeaturePython)
  n = 2
  ref = N_element
FEATURE [App::DocumentObjectGroupPython] O_element129  label="O_element : 9"  # scripted group (container) (typed FeaturePython)
  n = 9
  ref = O_element
FEATURE [App::DocumentObjectGroupPython] P_element018  label="P_element : 007"  # scripted group (container) (typed FeaturePython)
  n = 1
  ref = P_element
FEATURE [App::DocumentObjectGroupPython] G4_DNA_U  # scripted group (container) (typed FeaturePython)
  Dunit = g/cm3
  Dvalue = 1
  Group = -> [H_element137,C_element147,N_element067,O_element129,P_element018]
  conduct = 2
  density = 1
  expand = 3
  formula = G4_DNA_U
  name = G4_DNA_U
  specific = 4
FEATURE [App::DocumentObjectGroupPython] H_element138  label="H_element : 085"  # scripted group (container) (typed FeaturePython)
  n = 11
  ref = H_element
FEATURE [App::DocumentObjectGroupPython] C_element148  label="C_element : 093"  # scripted group (container) (typed FeaturePython)
  n = 10
  ref = C_element
FEATURE [App::DocumentObjectGroupPython] N_element068  label="N_element : 040"  # scripted group (container) (typed FeaturePython)
  n = 2
  ref = N_element
FEATURE [App::DocumentObjectGroupPython] O_element130  label="O_element : 081"  # scripted group (container) (typed FeaturePython)
  n = 9
  ref = O_element
FEATURE [App::DocumentObjectGroupPython] P_element019  label="P_element : 008"  # scripted group (container) (typed FeaturePython)
  n = 1
  ref = P_element
FEATURE [App::DocumentObjectGroupPython] G4_DNA_MU  # scripted group (container) (typed FeaturePython)
  Dunit = g/cm3
  Dvalue = 1
  Group = -> [H_element138,C_element148,N_element068,O_element130,P_element019]
  conduct = 2
  density = 1
  expand = 3
  formula = G4_DNA_MU
  name = G4_DNA_MU
  specific = 4
FEATURE [App::DocumentObjectGroupPython] BioChemical  # scripted group (container) (typed FeaturePython)
  Group = -> [G4_CYTOSINE,G4_THYMINE,G4_URACIL,G4_DNA_ADENINE,G4_DNA_GUANINE,G4_DNA_CYTOSINE,G4_DNA_THYMINE,G4_DNA_URACIL,G4_DNA_ADENOSINE,G4_DNA_GUANOSINE,G4_DNA_CYTIDINE,G4_DNA_URIDINE,G4_DNA_METHYLURIDINE,G4_DNA_MONOPHOSPHATE,G4_DNA_A,G4_DNA_G,G4_DNA_C,G4_DNA_U,G4_DNA_MU]
FEATURE [App::DocumentObjectGroupPython] G4Materials  # scripted group (container) (typed FeaturePython)
  Group = -> [NIST,Element,HEP,Space,BioChemical]
  version = 1
FEATURE [App::DocumentObjectGroupPython] Geant4  # scripted group (container) (typed FeaturePython)
  Group = -> [G4Isotopes,G4Elements,G4Materials]
FEATURE [App::DocumentObjectGroupPython] Materials  # scripted group (container) (typed FeaturePython)
  Group = -> [Geant4]
FEATURE [Part::FeaturePython] GDMLBox_WorldBox  # WARN: FeaturePython — macro-defined, semantics opaque (R4)
  lunit = 2
  material = 5
  x = 100
  y = 100
  z = 100
FEATURE [Sketcher::SketchObject] Sketch001
  ArcFitTolerance = 0
  FullyConstrained = false
  MakeInternals = false
  Placement = pos=(0,0,0) rot=(1,0,0;1.5708rad)
  sketch-geometry (15):
    g0-g7: Circle [constr] x8 (B-spline internal-alignment scaffolding for g8; pole/knot coordinates omitted)
    g8: BSplineCurve PolesCount=8 KnotsCount=6 Degree=3 IsPeriodic=0
    g9-g14: GeomPoint [constr] x6 (B-spline internal-alignment scaffolding for g8; pole/knot coordinates omitted)
  constraints (5):
    c: Weight(g0) = 1
    c: Equal(g0, g1-g7) x7
    c: Coincident(g7,g0)
    c: InternalAlignment(g0-g7 -> g8) x8
    c: InternalAlignment(g9-g14 -> g8) x6
FEATURE [Part::Revolution] Revolve
  Angle = 360
  Axis = (0,0,1)
  Base = (0,0,0)
  FaceMakerClass = Part::FaceMakerBullseye
  Solid = true
  Source = -> Sketch001
  Symmetric = false
  material = 5
FEATURE [App::Part] Part
  Group = -> [Sketch001,Revolve]
  Origin = -> Origin001
FEATURE [App::Part] worldVOL
  Group = -> [GDMLBox_WorldBox,Part]
  Origin = -> Origin
